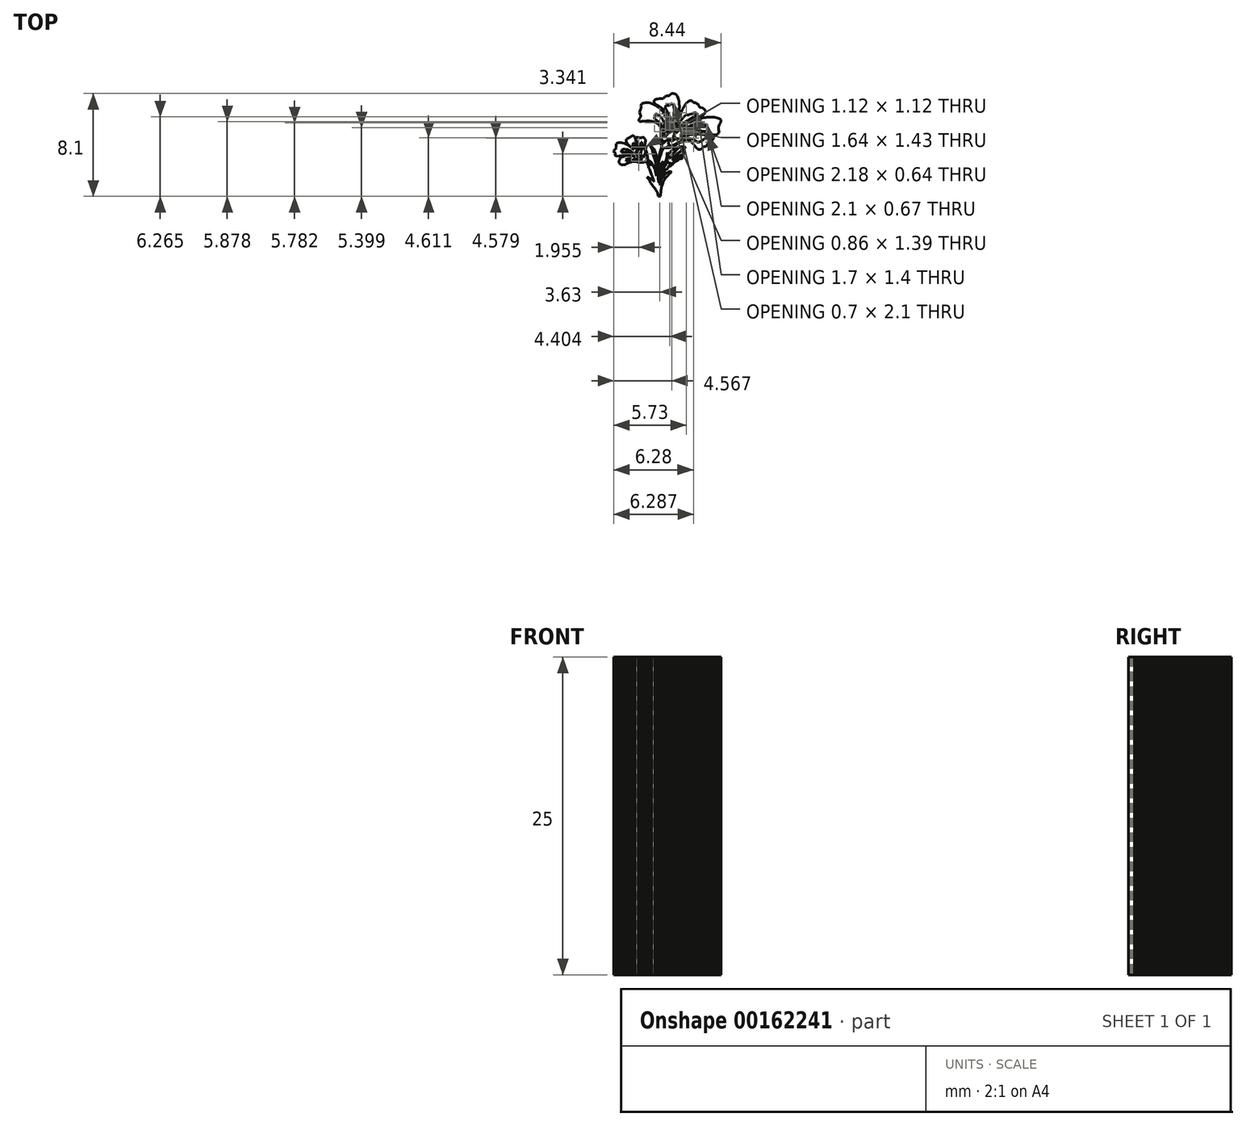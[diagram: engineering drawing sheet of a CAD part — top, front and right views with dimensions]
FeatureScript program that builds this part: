
annotation { "Feature Type Name" : "Feature", "Feature Type Description" : "" }
export const myFeature = defineFeature(function(context is Context, id is Id, definition is map)
    precondition{}
    {
        {
            var Q0;
            Q0=qCreatedBy(makeId("Top.planeOp"),FACE);
            var sketch = newSketch(context, id + "F0", { "sketchPlane" : qUnion([Q0])});
            skLineSegment(sketch, "E0", {"start": v(-2.53, -5.1) * mm, "end": v(-2.55, -5) * mm});
            skLineSegment(sketch, "E1", {"start": v(-2.55, -5) * mm, "end": v(-2.57, -4.93) * mm});
            skLineSegment(sketch, "E2", {"start": v(-2.57, -4.93) * mm, "end": v(-2.6, -4.87) * mm});
            skLineSegment(sketch, "E3", {"start": v(-2.6, -4.87) * mm, "end": v(-2.62, -4.82) * mm});
            skLineSegment(sketch, "E4", {"start": v(-2.62, -4.82) * mm, "end": v(-2.65, -4.76) * mm});
            skLineSegment(sketch, "E5", {"start": v(-2.65, -4.76) * mm, "end": v(-2.7, -4.67) * mm});
            skLineSegment(sketch, "E6", {"start": v(-2.7, -4.67) * mm, "end": v(-2.79, -4.56) * mm});
            skLineSegment(sketch, "E7", {"start": v(-2.79, -4.56) * mm, "end": v(-2.9, -4.42) * mm});
            skLineSegment(sketch, "E8", {"start": v(-2.9, -4.42) * mm, "end": v(-2.98, -4.32) * mm});
            skLineSegment(sketch, "E9", {"start": v(-2.98, -4.32) * mm, "end": v(-3.03, -4.24) * mm});
            skLineSegment(sketch, "E10", {"start": v(-3.03, -4.24) * mm, "end": v(-3.08, -4.18) * mm});
            skLineSegment(sketch, "E11", {"start": v(-3.08, -4.18) * mm, "end": v(-3.12, -4.13) * mm});
            skLineSegment(sketch, "E12", {"start": v(-3.12, -4.13) * mm, "end": v(-3.14, -4.1) * mm});
            skLineSegment(sketch, "E13", {"start": v(-3.14, -4.1) * mm, "end": v(-3.16, -4.06) * mm});
            skLineSegment(sketch, "E14", {"start": v(-3.16, -4.06) * mm, "end": v(-3.16, -4.04) * mm});
            skLineSegment(sketch, "E15", {"start": v(-3.16, -4.04) * mm, "end": v(-3.17, -4.02) * mm});
            skLineSegment(sketch, "E16", {"start": v(-3.17, -4.02) * mm, "end": v(-3.17, -4.01) * mm});
            skLineSegment(sketch, "E17", {"start": v(-3.17, -4.01) * mm, "end": v(-3.18, -4) * mm});
            skLineSegment(sketch, "E18", {"start": v(-3.18, -4) * mm, "end": v(-3.19, -3.97) * mm});
            skLineSegment(sketch, "E19", {"start": v(-3.19, -3.97) * mm, "end": v(-3.2, -3.95) * mm});
            skLineSegment(sketch, "E20", {"start": v(-3.2, -3.95) * mm, "end": v(-3.26, -3.85) * mm});
            skLineSegment(sketch, "E21", {"start": v(-3.26, -3.85) * mm, "end": v(-3.35, -3.76) * mm});
            skLineSegment(sketch, "E22", {"start": v(-3.35, -3.76) * mm, "end": v(-3.4, -3.73) * mm});
            skLineSegment(sketch, "E23", {"start": v(-3.4, -3.73) * mm, "end": v(-3.4, -3.7) * mm});
            skLineSegment(sketch, "E24", {"start": v(-3.4, -3.7) * mm, "end": v(-3.39, -3.69) * mm});
            skLineSegment(sketch, "E25", {"start": v(-3.39, -3.69) * mm, "end": v(-3.37, -3.68) * mm});
            skLineSegment(sketch, "E26", {"start": v(-3.37, -3.68) * mm, "end": v(-3.34, -3.69) * mm});
            skLineSegment(sketch, "E27", {"start": v(-3.34, -3.69) * mm, "end": v(-3.3, -3.7) * mm});
            skLineSegment(sketch, "E28", {"start": v(-3.3, -3.7) * mm, "end": v(-3.26, -3.74) * mm});
            skLineSegment(sketch, "E29", {"start": v(-3.26, -3.74) * mm, "end": v(-3.21, -3.76) * mm});
            skLineSegment(sketch, "E30", {"start": v(-3.21, -3.76) * mm, "end": v(-3.19, -3.77) * mm});
            skLineSegment(sketch, "E31", {"start": v(-3.19, -3.77) * mm, "end": v(-3.16, -3.79) * mm});
            skLineSegment(sketch, "E32", {"start": v(-3.16, -3.79) * mm, "end": v(-3.12, -3.8) * mm});
            skLineSegment(sketch, "E33", {"start": v(-3.12, -3.8) * mm, "end": v(-3.1, -3.82) * mm});
            skLineSegment(sketch, "E34", {"start": v(-3.1, -3.82) * mm, "end": v(-3.06, -3.84) * mm});
            skLineSegment(sketch, "E35", {"start": v(-3.06, -3.84) * mm, "end": v(-3.03, -3.86) * mm});
            skLineSegment(sketch, "E36", {"start": v(-3.03, -3.86) * mm, "end": v(-3.01, -3.88) * mm});
            skLineSegment(sketch, "E37", {"start": v(-3.01, -3.88) * mm, "end": v(-3, -3.9) * mm});
            skLineSegment(sketch, "E38", {"start": v(-3, -3.9) * mm, "end": v(-2.98, -3.91) * mm});
            skLineSegment(sketch, "E39", {"start": v(-2.98, -3.91) * mm, "end": v(-2.96, -3.92) * mm});
            skLineSegment(sketch, "E40", {"start": v(-2.96, -3.92) * mm, "end": v(-2.95, -3.92) * mm});
            skLineSegment(sketch, "E41", {"start": v(-2.95, -3.92) * mm, "end": v(-2.94, -3.93) * mm});
            skLineSegment(sketch, "E42", {"start": v(-2.94, -3.93) * mm, "end": v(-2.92, -3.95) * mm});
            skLineSegment(sketch, "E43", {"start": v(-2.92, -3.95) * mm, "end": v(-2.9, -3.97) * mm});
            skLineSegment(sketch, "E44", {"start": v(-2.9, -3.97) * mm, "end": v(-2.88, -3.98) * mm});
            skLineSegment(sketch, "E45", {"start": v(-2.88, -3.98) * mm, "end": v(-2.87, -4) * mm});
            skLineSegment(sketch, "E46", {"start": v(-2.87, -4) * mm, "end": v(-2.86, -4) * mm});
            skLineSegment(sketch, "E47", {"start": v(-2.86, -4) * mm, "end": v(-2.85, -4) * mm});
            skLineSegment(sketch, "E48", {"start": v(-2.85, -4) * mm, "end": v(-2.85, -3.99) * mm});
            skLineSegment(sketch, "E49", {"start": v(-2.85, -3.99) * mm, "end": v(-2.87, -3.96) * mm});
            skLineSegment(sketch, "E50", {"start": v(-2.87, -3.96) * mm, "end": v(-2.9, -3.85) * mm});
            skLineSegment(sketch, "E51", {"start": v(-2.9, -3.85) * mm, "end": v(-2.96, -3.68) * mm});
            skLineSegment(sketch, "E52", {"start": v(-2.96, -3.68) * mm, "end": v(-2.98, -3.63) * mm});
            skLineSegment(sketch, "E53", {"start": v(-2.98, -3.63) * mm, "end": v(-3, -3.58) * mm});
            skLineSegment(sketch, "E54", {"start": v(-3, -3.58) * mm, "end": v(-3, -3.54) * mm});
            skLineSegment(sketch, "E55", {"start": v(-3, -3.54) * mm, "end": v(-3.02, -3.5) * mm});
            skLineSegment(sketch, "E56", {"start": v(-3.02, -3.5) * mm, "end": v(-3.05, -3.43) * mm});
            skLineSegment(sketch, "E57", {"start": v(-3.05, -3.43) * mm, "end": v(-3.09, -3.35) * mm});
            skLineSegment(sketch, "E58", {"start": v(-3.09, -3.35) * mm, "end": v(-3.13, -3.26) * mm});
            skLineSegment(sketch, "E59", {"start": v(-3.13, -3.26) * mm, "end": v(-3.16, -3.16) * mm});
            skLineSegment(sketch, "E60", {"start": v(-3.16, -3.16) * mm, "end": v(-3.2, -3.06) * mm});
            skLineSegment(sketch, "E61", {"start": v(-3.2, -3.06) * mm, "end": v(-3.24, -2.96) * mm});
            skLineSegment(sketch, "E62", {"start": v(-3.24, -2.96) * mm, "end": v(-3.28, -2.87) * mm});
            skLineSegment(sketch, "E63", {"start": v(-3.28, -2.87) * mm, "end": v(-3.3, -2.79) * mm});
            skLineSegment(sketch, "E64", {"start": v(-3.3, -2.79) * mm, "end": v(-3.34, -2.7) * mm});
            skLineSegment(sketch, "E65", {"start": v(-3.34, -2.7) * mm, "end": v(-3.36, -2.62) * mm});
            skLineSegment(sketch, "E66", {"start": v(-3.36, -2.62) * mm, "end": v(-3.38, -2.57) * mm});
            skLineSegment(sketch, "E67", {"start": v(-3.38, -2.57) * mm, "end": v(-3.4, -2.53) * mm});
            skLineSegment(sketch, "E68", {"start": v(-3.4, -2.53) * mm, "end": v(-3.42, -2.5) * mm});
            skLineSegment(sketch, "E69", {"start": v(-3.42, -2.5) * mm, "end": v(-3.44, -2.5) * mm});
            skLineSegment(sketch, "E70", {"start": v(-3.44, -2.5) * mm, "end": v(-3.46, -2.49) * mm});
            skLineSegment(sketch, "E71", {"start": v(-3.46, -2.49) * mm, "end": v(-3.48, -2.49) * mm});
            skLineSegment(sketch, "E72", {"start": v(-3.48, -2.49) * mm, "end": v(-3.52, -2.48) * mm});
            skLineSegment(sketch, "E73", {"start": v(-3.52, -2.48) * mm, "end": v(-3.56, -2.47) * mm});
            skLineSegment(sketch, "E74", {"start": v(-3.56, -2.47) * mm, "end": v(-3.57, -2.47) * mm});
            skLineSegment(sketch, "E75", {"start": v(-3.57, -2.47) * mm, "end": v(-3.6, -2.47) * mm});
            skLineSegment(sketch, "E76", {"start": v(-3.6, -2.47) * mm, "end": v(-3.62, -2.47) * mm});
            skLineSegment(sketch, "E77", {"start": v(-3.62, -2.47) * mm, "end": v(-3.66, -2.5) * mm});
            skLineSegment(sketch, "E78", {"start": v(-3.66, -2.5) * mm, "end": v(-3.68, -2.5) * mm});
            skLineSegment(sketch, "E79", {"start": v(-3.68, -2.5) * mm, "end": v(-3.7, -2.51) * mm});
            skLineSegment(sketch, "E80", {"start": v(-3.7, -2.51) * mm, "end": v(-3.72, -2.52) * mm});
            skLineSegment(sketch, "E81", {"start": v(-3.72, -2.52) * mm, "end": v(-3.74, -2.52) * mm});
            skLineSegment(sketch, "E82", {"start": v(-3.74, -2.52) * mm, "end": v(-3.76, -2.52) * mm});
            skLineSegment(sketch, "E83", {"start": v(-3.76, -2.52) * mm, "end": v(-3.8, -2.52) * mm});
            skLineSegment(sketch, "E84", {"start": v(-3.8, -2.52) * mm, "end": v(-3.83, -2.53) * mm});
            skLineSegment(sketch, "E85", {"start": v(-3.83, -2.53) * mm, "end": v(-3.87, -2.53) * mm});
            skLineSegment(sketch, "E86", {"start": v(-3.87, -2.53) * mm, "end": v(-3.95, -2.52) * mm});
            skLineSegment(sketch, "E87", {"start": v(-3.95, -2.52) * mm, "end": v(-4.02, -2.52) * mm});
            skLineSegment(sketch, "E88", {"start": v(-4.02, -2.52) * mm, "end": v(-4.1, -2.5) * mm});
            skLineSegment(sketch, "E89", {"start": v(-4.1, -2.5) * mm, "end": v(-4.19, -2.5) * mm});
            skLineSegment(sketch, "E90", {"start": v(-4.19, -2.5) * mm, "end": v(-4.33, -2.46) * mm});
            skLineSegment(sketch, "E91", {"start": v(-4.33, -2.46) * mm, "end": v(-4.43, -2.45) * mm});
            skLineSegment(sketch, "E92", {"start": v(-4.43, -2.45) * mm, "end": v(-4.5, -2.45) * mm});
            skLineSegment(sketch, "E93", {"start": v(-4.5, -2.45) * mm, "end": v(-4.57, -2.46) * mm});
            skLineSegment(sketch, "E94", {"start": v(-4.57, -2.46) * mm, "end": v(-4.62, -2.47) * mm});
            skLineSegment(sketch, "E95", {"start": v(-4.62, -2.47) * mm, "end": v(-4.64, -2.49) * mm});
            skLineSegment(sketch, "E96", {"start": v(-4.64, -2.49) * mm, "end": v(-4.65, -2.5) * mm});
            skLineSegment(sketch, "E97", {"start": v(-4.65, -2.5) * mm, "end": v(-4.67, -2.5) * mm});
            skLineSegment(sketch, "E98", {"start": v(-4.67, -2.5) * mm, "end": v(-4.7, -2.51) * mm});
            skLineSegment(sketch, "E99", {"start": v(-4.7, -2.51) * mm, "end": v(-4.74, -2.53) * mm});
            skLineSegment(sketch, "E100", {"start": v(-4.74, -2.53) * mm, "end": v(-4.92, -2.59) * mm});
            skLineSegment(sketch, "E101", {"start": v(-4.92, -2.59) * mm, "end": v(-5.1, -2.67) * mm});
            skLineSegment(sketch, "E102", {"start": v(-5.1, -2.67) * mm, "end": v(-5.15, -2.7) * mm});
            skLineSegment(sketch, "E103", {"start": v(-5.15, -2.7) * mm, "end": v(-5.2, -2.7) * mm});
            skLineSegment(sketch, "E104", {"start": v(-5.2, -2.7) * mm, "end": v(-5.24, -2.71) * mm});
            skLineSegment(sketch, "E105", {"start": v(-5.24, -2.71) * mm, "end": v(-5.3, -2.71) * mm});
            skLineSegment(sketch, "E106", {"start": v(-5.3, -2.71) * mm, "end": v(-5.38, -2.71) * mm});
            skLineSegment(sketch, "E107", {"start": v(-5.38, -2.71) * mm, "end": v(-5.44, -2.7) * mm});
            skLineSegment(sketch, "E108", {"start": v(-5.44, -2.7) * mm, "end": v(-5.49, -2.67) * mm});
            skLineSegment(sketch, "E109", {"start": v(-5.49, -2.67) * mm, "end": v(-5.55, -2.62) * mm});
            skLineSegment(sketch, "E110", {"start": v(-5.55, -2.62) * mm, "end": v(-5.62, -2.56) * mm});
            skLineSegment(sketch, "E111", {"start": v(-5.62, -2.56) * mm, "end": v(-5.62, -2.5) * mm});
            skLineSegment(sketch, "E112", {"start": v(-5.62, -2.5) * mm, "end": v(-5.6, -2.44) * mm});
            skLineSegment(sketch, "E113", {"start": v(-5.6, -2.44) * mm, "end": v(-5.58, -2.37) * mm});
            skLineSegment(sketch, "E114", {"start": v(-5.58, -2.37) * mm, "end": v(-5.57, -2.35) * mm});
            skLineSegment(sketch, "E115", {"start": v(-5.57, -2.35) * mm, "end": v(-5.56, -2.32) * mm});
            skLineSegment(sketch, "E116", {"start": v(-5.56, -2.32) * mm, "end": v(-5.55, -2.3) * mm});
            skLineSegment(sketch, "E117", {"start": v(-5.55, -2.3) * mm, "end": v(-5.55, -2.28) * mm});
            skLineSegment(sketch, "E118", {"start": v(-5.55, -2.28) * mm, "end": v(-5.54, -2.25) * mm});
            skLineSegment(sketch, "E119", {"start": v(-5.54, -2.25) * mm, "end": v(-5.53, -2.22) * mm});
            skLineSegment(sketch, "E120", {"start": v(-5.53, -2.22) * mm, "end": v(-5.48, -2.17) * mm});
            skLineSegment(sketch, "E121", {"start": v(-5.48, -2.17) * mm, "end": v(-5.38, -2.11) * mm});
            skLineSegment(sketch, "E122", {"start": v(-5.38, -2.11) * mm, "end": v(-5.26, -2.06) * mm});
            skLineSegment(sketch, "E123", {"start": v(-5.26, -2.06) * mm, "end": v(-5.12, -2.02) * mm});
            skLineSegment(sketch, "E124", {"start": v(-5.12, -2.02) * mm, "end": v(-4.83, -2) * mm});
            skLineSegment(sketch, "E125", {"start": v(-4.83, -2) * mm, "end": v(-4.54, -2.02) * mm});
            skLineSegment(sketch, "E126", {"start": v(-4.54, -2.02) * mm, "end": v(-4.49, -2.04) * mm});
            skLineSegment(sketch, "E127", {"start": v(-4.49, -2.04) * mm, "end": v(-4.44, -2.05) * mm});
            skLineSegment(sketch, "E128", {"start": v(-4.44, -2.05) * mm, "end": v(-4.4, -2.06) * mm});
            skLineSegment(sketch, "E129", {"start": v(-4.4, -2.06) * mm, "end": v(-4.4, -2.06) * mm});
            skLineSegment(sketch, "E130", {"start": v(-4.4, -2.06) * mm, "end": v(-4.37, -2.07) * mm});
            skLineSegment(sketch, "E131", {"start": v(-4.37, -2.07) * mm, "end": v(-4.35, -2.08) * mm});
            skLineSegment(sketch, "E132", {"start": v(-4.35, -2.08) * mm, "end": v(-4.34, -2.07) * mm});
            skLineSegment(sketch, "E133", {"start": v(-4.34, -2.07) * mm, "end": v(-4.33, -2.07) * mm});
            skLineSegment(sketch, "E134", {"start": v(-4.33, -2.07) * mm, "end": v(-4.35, -2.06) * mm});
            skLineSegment(sketch, "E135", {"start": v(-4.35, -2.06) * mm, "end": v(-4.38, -2.04) * mm});
            skLineSegment(sketch, "E136", {"start": v(-4.38, -2.04) * mm, "end": v(-4.44, -2.03) * mm});
            skLineSegment(sketch, "E137", {"start": v(-4.44, -2.03) * mm, "end": v(-4.5, -2.01) * mm});
            skLineSegment(sketch, "E138", {"start": v(-4.5, -2.01) * mm, "end": v(-4.58, -2) * mm});
            skLineSegment(sketch, "E139", {"start": v(-4.58, -2) * mm, "end": v(-4.67, -1.98) * mm});
            skLineSegment(sketch, "E140", {"start": v(-4.67, -1.98) * mm, "end": v(-4.75, -1.97) * mm});
            skLineSegment(sketch, "E141", {"start": v(-4.75, -1.97) * mm, "end": v(-4.83, -1.96) * mm});
            skLineSegment(sketch, "E142", {"start": v(-4.83, -1.96) * mm, "end": v(-5.14, -1.96) * mm});
            skLineSegment(sketch, "E143", {"start": v(-5.14, -1.96) * mm, "end": v(-5.42, -2) * mm});
            skLineSegment(sketch, "E144", {"start": v(-5.42, -2) * mm, "end": v(-5.58, -2.02) * mm});
            skLineSegment(sketch, "E145", {"start": v(-5.58, -2.02) * mm, "end": v(-5.71, -2.03) * mm});
            skLineSegment(sketch, "E146", {"start": v(-5.71, -2.03) * mm, "end": v(-5.82, -2.01) * mm});
            skLineSegment(sketch, "E147", {"start": v(-5.82, -2.01) * mm, "end": v(-5.9, -1.97) * mm});
            skLineSegment(sketch, "E148", {"start": v(-5.9, -1.97) * mm, "end": v(-5.92, -1.94) * mm});
            skLineSegment(sketch, "E149", {"start": v(-5.92, -1.94) * mm, "end": v(-5.92, -1.9) * mm});
            skLineSegment(sketch, "E150", {"start": v(-5.92, -1.9) * mm, "end": v(-5.9, -1.86) * mm});
            skLineSegment(sketch, "E151", {"start": v(-5.9, -1.86) * mm, "end": v(-5.87, -1.82) * mm});
            skLineSegment(sketch, "E152", {"start": v(-5.87, -1.82) * mm, "end": v(-5.83, -1.8) * mm});
            skLineSegment(sketch, "E153", {"start": v(-5.83, -1.8) * mm, "end": v(-5.88, -1.78) * mm});
            skLineSegment(sketch, "E154", {"start": v(-5.88, -1.78) * mm, "end": v(-5.98, -1.71) * mm});
            skLineSegment(sketch, "E155", {"start": v(-5.98, -1.71) * mm, "end": v(-6.02, -1.64) * mm});
            skLineSegment(sketch, "E156", {"start": v(-6.02, -1.64) * mm, "end": v(-6, -1.56) * mm});
            skLineSegment(sketch, "E157", {"start": v(-6, -1.56) * mm, "end": v(-5.93, -1.5) * mm});
            skLineSegment(sketch, "E158", {"start": v(-5.93, -1.5) * mm, "end": v(-5.89, -1.46) * mm});
            skLineSegment(sketch, "E159", {"start": v(-5.89, -1.46) * mm, "end": v(-5.85, -1.44) * mm});
            skLineSegment(sketch, "E160", {"start": v(-5.85, -1.44) * mm, "end": v(-5.83, -1.42) * mm});
            skLineSegment(sketch, "E161", {"start": v(-5.83, -1.42) * mm, "end": v(-5.82, -1.4) * mm});
            skLineSegment(sketch, "E162", {"start": v(-5.82, -1.4) * mm, "end": v(-5.81, -1.38) * mm});
            skLineSegment(sketch, "E163", {"start": v(-5.81, -1.38) * mm, "end": v(-5.81, -1.36) * mm});
            skLineSegment(sketch, "E164", {"start": v(-5.81, -1.36) * mm, "end": v(-5.82, -1.33) * mm});
            skLineSegment(sketch, "E165", {"start": v(-5.82, -1.33) * mm, "end": v(-5.83, -1.3) * mm});
            skLineSegment(sketch, "E166", {"start": v(-5.83, -1.3) * mm, "end": v(-5.84, -1.24) * mm});
            skLineSegment(sketch, "E167", {"start": v(-5.84, -1.24) * mm, "end": v(-5.84, -1.18) * mm});
            skLineSegment(sketch, "E168", {"start": v(-5.84, -1.18) * mm, "end": v(-5.84, -1.12) * mm});
            skLineSegment(sketch, "E169", {"start": v(-5.84, -1.12) * mm, "end": v(-5.82, -1.07) * mm});
            skLineSegment(sketch, "E170", {"start": v(-5.82, -1.07) * mm, "end": v(-5.78, -1.02) * mm});
            skLineSegment(sketch, "E171", {"start": v(-5.78, -1.02) * mm, "end": v(-5.72, -0.98) * mm});
            skLineSegment(sketch, "E172", {"start": v(-5.72, -0.98) * mm, "end": v(-5.64, -0.96) * mm});
            skLineSegment(sketch, "E173", {"start": v(-5.64, -0.96) * mm, "end": v(-5.55, -0.95) * mm});
            skLineSegment(sketch, "E174", {"start": v(-5.55, -0.95) * mm, "end": v(-5.43, -0.96) * mm});
            skLineSegment(sketch, "E175", {"start": v(-5.43, -0.96) * mm, "end": v(-5.3, -1) * mm});
            skLineSegment(sketch, "E176", {"start": v(-5.3, -1) * mm, "end": v(-5.18, -1.04) * mm});
            skLineSegment(sketch, "E177", {"start": v(-5.18, -1.04) * mm, "end": v(-5.04, -1.1) * mm});
            skLineSegment(sketch, "E178", {"start": v(-5.04, -1.1) * mm, "end": v(-4.9, -1.16) * mm});
            skLineSegment(sketch, "E179", {"start": v(-4.9, -1.16) * mm, "end": v(-4.78, -1.24) * mm});
            skLineSegment(sketch, "E180", {"start": v(-4.78, -1.24) * mm, "end": v(-4.65, -1.33) * mm});
            skLineSegment(sketch, "E181", {"start": v(-4.65, -1.33) * mm, "end": v(-4.55, -1.42) * mm});
            skLineSegment(sketch, "E182", {"start": v(-4.55, -1.42) * mm, "end": v(-4.5, -1.46) * mm});
            skLineSegment(sketch, "E183", {"start": v(-4.5, -1.46) * mm, "end": v(-4.47, -1.5) * mm});
            skLineSegment(sketch, "E184", {"start": v(-4.47, -1.5) * mm, "end": v(-4.45, -1.5) * mm});
            skLineSegment(sketch, "E185", {"start": v(-4.45, -1.5) * mm, "end": v(-4.45, -1.5) * mm});
            skLineSegment(sketch, "E186", {"start": v(-4.45, -1.5) * mm, "end": v(-4.48, -1.46) * mm});
            skLineSegment(sketch, "E187", {"start": v(-4.48, -1.46) * mm, "end": v(-4.51, -1.43) * mm});
            skLineSegment(sketch, "E188", {"start": v(-4.51, -1.43) * mm, "end": v(-4.56, -1.39) * mm});
            skLineSegment(sketch, "E189", {"start": v(-4.56, -1.39) * mm, "end": v(-4.6, -1.34) * mm});
            skLineSegment(sketch, "E190", {"start": v(-4.6, -1.34) * mm, "end": v(-4.65, -1.3) * mm});
            skLineSegment(sketch, "E191", {"start": v(-4.65, -1.3) * mm, "end": v(-4.7, -1.26) * mm});
            skLineSegment(sketch, "E192", {"start": v(-4.7, -1.26) * mm, "end": v(-4.73, -1.24) * mm});
            skLineSegment(sketch, "E193", {"start": v(-4.73, -1.24) * mm, "end": v(-4.77, -1.21) * mm});
            skLineSegment(sketch, "E194", {"start": v(-4.77, -1.21) * mm, "end": v(-4.8, -1.18) * mm});
            skLineSegment(sketch, "E195", {"start": v(-4.8, -1.18) * mm, "end": v(-4.85, -1.14) * mm});
            skLineSegment(sketch, "E196", {"start": v(-4.85, -1.14) * mm, "end": v(-4.88, -1.1) * mm});
            skLineSegment(sketch, "E197", {"start": v(-4.88, -1.1) * mm, "end": v(-4.98, -0.98) * mm});
            skLineSegment(sketch, "E198", {"start": v(-4.98, -0.98) * mm, "end": v(-5.03, -0.87) * mm});
            skLineSegment(sketch, "E199", {"start": v(-5.03, -0.87) * mm, "end": v(-5.03, -0.77) * mm});
            skLineSegment(sketch, "E200", {"start": v(-5.03, -0.77) * mm, "end": v(-4.99, -0.68) * mm});
            skLineSegment(sketch, "E201", {"start": v(-4.99, -0.68) * mm, "end": v(-4.95, -0.65) * mm});
            skLineSegment(sketch, "E202", {"start": v(-4.95, -0.65) * mm, "end": v(-4.9, -0.61) * mm});
            skLineSegment(sketch, "E203", {"start": v(-4.9, -0.61) * mm, "end": v(-4.82, -0.58) * mm});
            skLineSegment(sketch, "E204", {"start": v(-4.82, -0.58) * mm, "end": v(-4.76, -0.55) * mm});
            skLineSegment(sketch, "E205", {"start": v(-4.76, -0.55) * mm, "end": v(-4.72, -0.53) * mm});
            skLineSegment(sketch, "E206", {"start": v(-4.72, -0.53) * mm, "end": v(-4.7, -0.5) * mm});
            skLineSegment(sketch, "E207", {"start": v(-4.7, -0.5) * mm, "end": v(-4.67, -0.47) * mm});
            skLineSegment(sketch, "E208", {"start": v(-4.67, -0.47) * mm, "end": v(-4.63, -0.45) * mm});
            skLineSegment(sketch, "E209", {"start": v(-4.63, -0.45) * mm, "end": v(-4.6, -0.43) * mm});
            skLineSegment(sketch, "E210", {"start": v(-4.6, -0.43) * mm, "end": v(-4.55, -0.43) * mm});
            skLineSegment(sketch, "E211", {"start": v(-4.55, -0.43) * mm, "end": v(-4.49, -0.44) * mm});
            skLineSegment(sketch, "E212", {"start": v(-4.49, -0.44) * mm, "end": v(-4.43, -0.47) * mm});
            skLineSegment(sketch, "E213", {"start": v(-4.43, -0.47) * mm, "end": v(-4.38, -0.51) * mm});
            skLineSegment(sketch, "E214", {"start": v(-4.38, -0.51) * mm, "end": v(-4.34, -0.58) * mm});
            skLineSegment(sketch, "E215", {"start": v(-4.34, -0.58) * mm, "end": v(-4.3, -0.66) * mm});
            skLineSegment(sketch, "E216", {"start": v(-4.3, -0.66) * mm, "end": v(-4.26, -0.8) * mm});
            skLineSegment(sketch, "E217", {"start": v(-4.26, -0.8) * mm, "end": v(-4.22, -0.97) * mm});
            skLineSegment(sketch, "E218", {"start": v(-4.22, -0.97) * mm, "end": v(-4.18, -1.14) * mm});
            skLineSegment(sketch, "E219", {"start": v(-4.18, -1.14) * mm, "end": v(-4.15, -1.26) * mm});
            skLineSegment(sketch, "E220", {"start": v(-4.15, -1.26) * mm, "end": v(-4.13, -1.34) * mm});
            skLineSegment(sketch, "E221", {"start": v(-4.13, -1.34) * mm, "end": v(-4.11, -1.4) * mm});
            skLineSegment(sketch, "E222", {"start": v(-4.11, -1.4) * mm, "end": v(-4.1, -1.4) * mm});
            skLineSegment(sketch, "E223", {"start": v(-4.1, -1.4) * mm, "end": v(-4.1, -1.4) * mm});
            skLineSegment(sketch, "E224", {"start": v(-4.1, -1.4) * mm, "end": v(-4.1, -1.39) * mm});
            skLineSegment(sketch, "E225", {"start": v(-4.1, -1.39) * mm, "end": v(-4.1, -1.36) * mm});
            skLineSegment(sketch, "E226", {"start": v(-4.1, -1.36) * mm, "end": v(-4.11, -1.32) * mm});
            skLineSegment(sketch, "E227", {"start": v(-4.11, -1.32) * mm, "end": v(-4.13, -1.27) * mm});
            skLineSegment(sketch, "E228", {"start": v(-4.13, -1.27) * mm, "end": v(-4.14, -1.2) * mm});
            skLineSegment(sketch, "E229", {"start": v(-4.14, -1.2) * mm, "end": v(-4.16, -1.14) * mm});
            skLineSegment(sketch, "E230", {"start": v(-4.16, -1.14) * mm, "end": v(-4.17, -1.06) * mm});
            skLineSegment(sketch, "E231", {"start": v(-4.17, -1.06) * mm, "end": v(-4.2, -0.97) * mm});
            skLineSegment(sketch, "E232", {"start": v(-4.2, -0.97) * mm, "end": v(-4.22, -0.87) * mm});
            skLineSegment(sketch, "E233", {"start": v(-4.22, -0.87) * mm, "end": v(-4.24, -0.8) * mm});
            skLineSegment(sketch, "E234", {"start": v(-4.24, -0.8) * mm, "end": v(-4.26, -0.72) * mm});
            skLineSegment(sketch, "E235", {"start": v(-4.26, -0.72) * mm, "end": v(-4.28, -0.66) * mm});
            skLineSegment(sketch, "E236", {"start": v(-4.28, -0.66) * mm, "end": v(-4.29, -0.61) * mm});
            skLineSegment(sketch, "E237", {"start": v(-4.29, -0.61) * mm, "end": v(-4.3, -0.59) * mm});
            skLineSegment(sketch, "E238", {"start": v(-4.3, -0.59) * mm, "end": v(-4.3, -0.57) * mm});
            skLineSegment(sketch, "E239", {"start": v(-4.3, -0.57) * mm, "end": v(-4.28, -0.56) * mm});
            skLineSegment(sketch, "E240", {"start": v(-4.28, -0.56) * mm, "end": v(-4.26, -0.56) * mm});
            skLineSegment(sketch, "E241", {"start": v(-4.26, -0.56) * mm, "end": v(-4.2, -0.56) * mm});
            skLineSegment(sketch, "E242", {"start": v(-4.2, -0.56) * mm, "end": v(-4.1, -0.56) * mm});
            skLineSegment(sketch, "E243", {"start": v(-4.1, -0.56) * mm, "end": v(-4, -0.58) * mm});
            skLineSegment(sketch, "E244", {"start": v(-4, -0.58) * mm, "end": v(-3.95, -0.58) * mm});
            skLineSegment(sketch, "E245", {"start": v(-3.95, -0.58) * mm, "end": v(-3.91, -0.6) * mm});
            skLineSegment(sketch, "E246", {"start": v(-3.91, -0.6) * mm, "end": v(-3.89, -0.6) * mm});
            skLineSegment(sketch, "E247", {"start": v(-3.89, -0.6) * mm, "end": v(-3.86, -0.6) * mm});
            skLineSegment(sketch, "E248", {"start": v(-3.86, -0.6) * mm, "end": v(-3.85, -0.6) * mm});
            skLineSegment(sketch, "E249", {"start": v(-3.85, -0.6) * mm, "end": v(-3.84, -0.6) * mm});
            skLineSegment(sketch, "E250", {"start": v(-3.84, -0.6) * mm, "end": v(-3.82, -0.59) * mm});
            skLineSegment(sketch, "E251", {"start": v(-3.82, -0.59) * mm, "end": v(-3.81, -0.58) * mm});
            skLineSegment(sketch, "E252", {"start": v(-3.81, -0.58) * mm, "end": v(-3.76, -0.56) * mm});
            skLineSegment(sketch, "E253", {"start": v(-3.76, -0.56) * mm, "end": v(-3.7, -0.56) * mm});
            skLineSegment(sketch, "E254", {"start": v(-3.7, -0.56) * mm, "end": v(-3.65, -0.58) * mm});
            skLineSegment(sketch, "E255", {"start": v(-3.65, -0.58) * mm, "end": v(-3.6, -0.63) * mm});
            skLineSegment(sketch, "E256", {"start": v(-3.6, -0.63) * mm, "end": v(-3.56, -0.67) * mm});
            skLineSegment(sketch, "E257", {"start": v(-3.56, -0.67) * mm, "end": v(-3.54, -0.71) * mm});
            skLineSegment(sketch, "E258", {"start": v(-3.54, -0.71) * mm, "end": v(-3.53, -0.77) * mm});
            skLineSegment(sketch, "E259", {"start": v(-3.53, -0.77) * mm, "end": v(-3.52, -0.84) * mm});
            skLineSegment(sketch, "E260", {"start": v(-3.52, -0.84) * mm, "end": v(-3.53, -0.93) * mm});
            skLineSegment(sketch, "E261", {"start": v(-3.53, -0.93) * mm, "end": v(-3.55, -1.02) * mm});
            skLineSegment(sketch, "E262", {"start": v(-3.55, -1.02) * mm, "end": v(-3.58, -1.12) * mm});
            skLineSegment(sketch, "E263", {"start": v(-3.58, -1.12) * mm, "end": v(-3.63, -1.23) * mm});
            skLineSegment(sketch, "E264", {"start": v(-3.63, -1.23) * mm, "end": v(-3.66, -1.3) * mm});
            skLineSegment(sketch, "E265", {"start": v(-3.66, -1.3) * mm, "end": v(-3.6, -1.27) * mm});
            skLineSegment(sketch, "E266", {"start": v(-3.6, -1.27) * mm, "end": v(-3.57, -1.25) * mm});
            skLineSegment(sketch, "E267", {"start": v(-3.57, -1.25) * mm, "end": v(-3.53, -1.24) * mm});
            skLineSegment(sketch, "E268", {"start": v(-3.53, -1.24) * mm, "end": v(-3.5, -1.25) * mm});
            skLineSegment(sketch, "E269", {"start": v(-3.5, -1.25) * mm, "end": v(-3.48, -1.26) * mm});
            skLineSegment(sketch, "E270", {"start": v(-3.48, -1.26) * mm, "end": v(-3.46, -1.27) * mm});
            skLineSegment(sketch, "E271", {"start": v(-3.46, -1.27) * mm, "end": v(-3.45, -1.29) * mm});
            skLineSegment(sketch, "E272", {"start": v(-3.45, -1.29) * mm, "end": v(-3.45, -1.31) * mm});
            skLineSegment(sketch, "E273", {"start": v(-3.45, -1.31) * mm, "end": v(-3.47, -1.34) * mm});
            skLineSegment(sketch, "E274", {"start": v(-3.47, -1.34) * mm, "end": v(-3.5, -1.4) * mm});
            skLineSegment(sketch, "E275", {"start": v(-3.5, -1.4) * mm, "end": v(-3.5, -1.48) * mm});
            skLineSegment(sketch, "E276", {"start": v(-3.5, -1.48) * mm, "end": v(-3.48, -1.6) * mm});
            skLineSegment(sketch, "E277", {"start": v(-3.48, -1.6) * mm, "end": v(-3.43, -1.73) * mm});
            skLineSegment(sketch, "E278", {"start": v(-3.43, -1.73) * mm, "end": v(-3.37, -1.92) * mm});
            skLineSegment(sketch, "E279", {"start": v(-3.37, -1.92) * mm, "end": v(-3.36, -2.1) * mm});
            skLineSegment(sketch, "E280", {"start": v(-3.36, -2.1) * mm, "end": v(-3.36, -2.14) * mm});
            skLineSegment(sketch, "E281", {"start": v(-3.36, -2.14) * mm, "end": v(-3.36, -2.17) * mm});
            skLineSegment(sketch, "E282", {"start": v(-3.36, -2.17) * mm, "end": v(-3.35, -2.2) * mm});
            skLineSegment(sketch, "E283", {"start": v(-3.35, -2.2) * mm, "end": v(-3.35, -2.21) * mm});
            skLineSegment(sketch, "E284", {"start": v(-3.35, -2.21) * mm, "end": v(-3.34, -2.25) * mm});
            skLineSegment(sketch, "E285", {"start": v(-3.34, -2.25) * mm, "end": v(-3.33, -2.29) * mm});
            skLineSegment(sketch, "E286", {"start": v(-3.33, -2.29) * mm, "end": v(-3.33, -2.33) * mm});
            skLineSegment(sketch, "E287", {"start": v(-3.33, -2.33) * mm, "end": v(-3.33, -2.36) * mm});
            skLineSegment(sketch, "E288", {"start": v(-3.33, -2.36) * mm, "end": v(-3.34, -2.38) * mm});
            skLineSegment(sketch, "E289", {"start": v(-3.34, -2.38) * mm, "end": v(-3.33, -2.4) * mm});
            skLineSegment(sketch, "E290", {"start": v(-3.33, -2.4) * mm, "end": v(-3.32, -2.43) * mm});
            skLineSegment(sketch, "E291", {"start": v(-3.32, -2.43) * mm, "end": v(-3.29, -2.48) * mm});
            skLineSegment(sketch, "E292", {"start": v(-3.29, -2.48) * mm, "end": v(-3.27, -2.52) * mm});
            skLineSegment(sketch, "E293", {"start": v(-3.27, -2.52) * mm, "end": v(-3.24, -2.56) * mm});
            skLineSegment(sketch, "E294", {"start": v(-3.24, -2.56) * mm, "end": v(-3.23, -2.6) * mm});
            skLineSegment(sketch, "E295", {"start": v(-3.23, -2.6) * mm, "end": v(-3.21, -2.63) * mm});
            skLineSegment(sketch, "E296", {"start": v(-3.21, -2.63) * mm, "end": v(-3.2, -2.65) * mm});
            skLineSegment(sketch, "E297", {"start": v(-3.2, -2.65) * mm, "end": v(-3.19, -2.69) * mm});
            skLineSegment(sketch, "E298", {"start": v(-3.19, -2.69) * mm, "end": v(-3.17, -2.72) * mm});
            skLineSegment(sketch, "E299", {"start": v(-3.17, -2.72) * mm, "end": v(-3.16, -2.75) * mm});
            skLineSegment(sketch, "E300", {"start": v(-3.16, -2.75) * mm, "end": v(-3.14, -2.8) * mm});
            skLineSegment(sketch, "E301", {"start": v(-3.14, -2.8) * mm, "end": v(-3.13, -2.8) * mm});
            skLineSegment(sketch, "E302", {"start": v(-3.13, -2.8) * mm, "end": v(-3.12, -2.8) * mm});
            skLineSegment(sketch, "E303", {"start": v(-3.12, -2.8) * mm, "end": v(-3.12, -2.79) * mm});
            skLineSegment(sketch, "E304", {"start": v(-3.12, -2.79) * mm, "end": v(-3.13, -2.72) * mm});
            skLineSegment(sketch, "E305", {"start": v(-3.13, -2.72) * mm, "end": v(-3.15, -2.65) * mm});
            skLineSegment(sketch, "E306", {"start": v(-3.15, -2.65) * mm, "end": v(-3.17, -2.58) * mm});
            skLineSegment(sketch, "E307", {"start": v(-3.17, -2.58) * mm, "end": v(-3.2, -2.52) * mm});
            skLineSegment(sketch, "E308", {"start": v(-3.2, -2.52) * mm, "end": v(-3.22, -2.47) * mm});
            skLineSegment(sketch, "E309", {"start": v(-3.22, -2.47) * mm, "end": v(-3.23, -2.44) * mm});
            skLineSegment(sketch, "E310", {"start": v(-3.23, -2.44) * mm, "end": v(-3.23, -2.41) * mm});
            skLineSegment(sketch, "E311", {"start": v(-3.23, -2.41) * mm, "end": v(-3.23, -2.4) * mm});
            skLineSegment(sketch, "E312", {"start": v(-3.23, -2.4) * mm, "end": v(-3.21, -2.39) * mm});
            skLineSegment(sketch, "E313", {"start": v(-3.21, -2.39) * mm, "end": v(-3.2, -2.4) * mm});
            skLineSegment(sketch, "E314", {"start": v(-3.2, -2.4) * mm, "end": v(-3.16, -2.41) * mm});
            skLineSegment(sketch, "E315", {"start": v(-3.16, -2.41) * mm, "end": v(-3.13, -2.44) * mm});
            skLineSegment(sketch, "E316", {"start": v(-3.13, -2.44) * mm, "end": v(-3.04, -2.54) * mm});
            skLineSegment(sketch, "E317", {"start": v(-3.04, -2.54) * mm, "end": v(-2.94, -2.68) * mm});
            skLineSegment(sketch, "E318", {"start": v(-2.94, -2.68) * mm, "end": v(-2.87, -2.83) * mm});
            skLineSegment(sketch, "E319", {"start": v(-2.87, -2.83) * mm, "end": v(-2.8, -2.99) * mm});
            skLineSegment(sketch, "E320", {"start": v(-2.8, -2.99) * mm, "end": v(-2.8, -3.03) * mm});
            skLineSegment(sketch, "E321", {"start": v(-2.8, -3.03) * mm, "end": v(-2.78, -3.07) * mm});
            skLineSegment(sketch, "E322", {"start": v(-2.78, -3.07) * mm, "end": v(-2.77, -3.1) * mm});
            skLineSegment(sketch, "E323", {"start": v(-2.77, -3.1) * mm, "end": v(-2.76, -3.13) * mm});
            skLineSegment(sketch, "E324", {"start": v(-2.76, -3.13) * mm, "end": v(-2.74, -3.2) * mm});
            skLineSegment(sketch, "E325", {"start": v(-2.74, -3.2) * mm, "end": v(-2.7, -3.3) * mm});
            skLineSegment(sketch, "E326", {"start": v(-2.7, -3.3) * mm, "end": v(-2.68, -3.45) * mm});
            skLineSegment(sketch, "E327", {"start": v(-2.68, -3.45) * mm, "end": v(-2.65, -3.6) * mm});
            skLineSegment(sketch, "E328", {"start": v(-2.65, -3.6) * mm, "end": v(-2.64, -3.6) * mm});
            skLineSegment(sketch, "E329", {"start": v(-2.64, -3.6) * mm, "end": v(-2.64, -3.54) * mm});
            skLineSegment(sketch, "E330", {"start": v(-2.64, -3.54) * mm, "end": v(-2.64, -3.43) * mm});
            skLineSegment(sketch, "E331", {"start": v(-2.64, -3.43) * mm, "end": v(-2.64, -3.26) * mm});
            skLineSegment(sketch, "E332", {"start": v(-2.64, -3.26) * mm, "end": v(-2.64, -3.05) * mm});
            skLineSegment(sketch, "E333", {"start": v(-2.64, -3.05) * mm, "end": v(-2.64, -2.92) * mm});
            skLineSegment(sketch, "E334", {"start": v(-2.64, -2.92) * mm, "end": v(-2.65, -2.83) * mm});
            skLineSegment(sketch, "E335", {"start": v(-2.65, -2.83) * mm, "end": v(-2.66, -2.77) * mm});
            skLineSegment(sketch, "E336", {"start": v(-2.66, -2.77) * mm, "end": v(-2.71, -2.54) * mm});
            skLineSegment(sketch, "E337", {"start": v(-2.71, -2.54) * mm, "end": v(-2.8, -2.3) * mm});
            skLineSegment(sketch, "E338", {"start": v(-2.8, -2.3) * mm, "end": v(-2.83, -2.2) * mm});
            skLineSegment(sketch, "E339", {"start": v(-2.83, -2.2) * mm, "end": v(-2.86, -2.11) * mm});
            skLineSegment(sketch, "E340", {"start": v(-2.86, -2.11) * mm, "end": v(-2.88, -2.04) * mm});
            skLineSegment(sketch, "E341", {"start": v(-2.88, -2.04) * mm, "end": v(-2.9, -1.98) * mm});
            skLineSegment(sketch, "E342", {"start": v(-2.9, -1.98) * mm, "end": v(-2.92, -1.92) * mm});
            skLineSegment(sketch, "E343", {"start": v(-2.92, -1.92) * mm, "end": v(-2.93, -1.86) * mm});
            skLineSegment(sketch, "E344", {"start": v(-2.93, -1.86) * mm, "end": v(-2.94, -1.8) * mm});
            skLineSegment(sketch, "E345", {"start": v(-2.94, -1.8) * mm, "end": v(-2.95, -1.74) * mm});
            skLineSegment(sketch, "E346", {"start": v(-2.95, -1.74) * mm, "end": v(-2.98, -1.58) * mm});
            skLineSegment(sketch, "E347", {"start": v(-2.98, -1.58) * mm, "end": v(-3.02, -1.46) * mm});
            skLineSegment(sketch, "E348", {"start": v(-3.02, -1.46) * mm, "end": v(-3.06, -1.37) * mm});
            skLineSegment(sketch, "E349", {"start": v(-3.06, -1.37) * mm, "end": v(-3.12, -1.3) * mm});
            skLineSegment(sketch, "E350", {"start": v(-3.12, -1.3) * mm, "end": v(-3.15, -1.27) * mm});
            skLineSegment(sketch, "E351", {"start": v(-3.15, -1.27) * mm, "end": v(-3.15, -1.25) * mm});
            skLineSegment(sketch, "E352", {"start": v(-3.15, -1.25) * mm, "end": v(-3.14, -1.24) * mm});
            skLineSegment(sketch, "E353", {"start": v(-3.14, -1.24) * mm, "end": v(-3.12, -1.24) * mm});
            skLineSegment(sketch, "E354", {"start": v(-3.12, -1.24) * mm, "end": v(-3.1, -1.26) * mm});
            skLineSegment(sketch, "E355", {"start": v(-3.1, -1.26) * mm, "end": v(-3.06, -1.28) * mm});
            skLineSegment(sketch, "E356", {"start": v(-3.06, -1.28) * mm, "end": v(-3.02, -1.3) * mm});
            skLineSegment(sketch, "E357", {"start": v(-3.02, -1.3) * mm, "end": v(-2.99, -1.34) * mm});
            skLineSegment(sketch, "E358", {"start": v(-2.99, -1.34) * mm, "end": v(-2.87, -1.47) * mm});
            skLineSegment(sketch, "E359", {"start": v(-2.87, -1.47) * mm, "end": v(-2.78, -1.63) * mm});
            skLineSegment(sketch, "E360", {"start": v(-2.78, -1.63) * mm, "end": v(-2.7, -1.8) * mm});
            skLineSegment(sketch, "E361", {"start": v(-2.7, -1.8) * mm, "end": v(-2.66, -2.01) * mm});
            skLineSegment(sketch, "E362", {"start": v(-2.66, -2.01) * mm, "end": v(-2.64, -2.13) * mm});
            skLineSegment(sketch, "E363", {"start": v(-2.64, -2.13) * mm, "end": v(-2.62, -2.28) * mm});
            skLineSegment(sketch, "E364", {"start": v(-2.62, -2.28) * mm, "end": v(-2.6, -2.42) * mm});
            skLineSegment(sketch, "E365", {"start": v(-2.6, -2.42) * mm, "end": v(-2.6, -2.52) * mm});
            skLineSegment(sketch, "E366", {"start": v(-2.6, -2.52) * mm, "end": v(-2.6, -2.56) * mm});
            skLineSegment(sketch, "E367", {"start": v(-2.6, -2.56) * mm, "end": v(-2.6, -2.56) * mm});
            skLineSegment(sketch, "E368", {"start": v(-2.6, -2.56) * mm, "end": v(-2.58, -2.54) * mm});
            skLineSegment(sketch, "E369", {"start": v(-2.58, -2.54) * mm, "end": v(-2.57, -2.5) * mm});
            skLineSegment(sketch, "E370", {"start": v(-2.57, -2.5) * mm, "end": v(-2.56, -2.4) * mm});
            skLineSegment(sketch, "E371", {"start": v(-2.56, -2.4) * mm, "end": v(-2.53, -2.28) * mm});
            skLineSegment(sketch, "E372", {"start": v(-2.53, -2.28) * mm, "end": v(-2.5, -2.16) * mm});
            skLineSegment(sketch, "E373", {"start": v(-2.5, -2.16) * mm, "end": v(-2.48, -2.07) * mm});
            skLineSegment(sketch, "E374", {"start": v(-2.48, -2.07) * mm, "end": v(-2.47, -2.04) * mm});
            skLineSegment(sketch, "E375", {"start": v(-2.47, -2.04) * mm, "end": v(-2.46, -2) * mm});
            skLineSegment(sketch, "E376", {"start": v(-2.46, -2) * mm, "end": v(-2.45, -1.95) * mm});
            skLineSegment(sketch, "E377", {"start": v(-2.45, -1.95) * mm, "end": v(-2.44, -1.9) * mm});
            skLineSegment(sketch, "E378", {"start": v(-2.44, -1.9) * mm, "end": v(-2.4, -1.8) * mm});
            skLineSegment(sketch, "E379", {"start": v(-2.4, -1.8) * mm, "end": v(-2.37, -1.69) * mm});
            skLineSegment(sketch, "E380", {"start": v(-2.37, -1.69) * mm, "end": v(-2.33, -1.57) * mm});
            skLineSegment(sketch, "E381", {"start": v(-2.33, -1.57) * mm, "end": v(-2.3, -1.48) * mm});
            skLineSegment(sketch, "E382", {"start": v(-2.3, -1.48) * mm, "end": v(-2.27, -1.42) * mm});
            skLineSegment(sketch, "E383", {"start": v(-2.27, -1.42) * mm, "end": v(-2.27, -1.36) * mm});
            skLineSegment(sketch, "E384", {"start": v(-2.27, -1.36) * mm, "end": v(-2.26, -1.3) * mm});
            skLineSegment(sketch, "E385", {"start": v(-2.26, -1.3) * mm, "end": v(-2.26, -1.24) * mm});
            skLineSegment(sketch, "E386", {"start": v(-2.26, -1.24) * mm, "end": v(-2.25, -1.21) * mm});
            skLineSegment(sketch, "E387", {"start": v(-2.25, -1.21) * mm, "end": v(-2.25, -1.19) * mm});
            skLineSegment(sketch, "E388", {"start": v(-2.25, -1.19) * mm, "end": v(-2.26, -1.17) * mm});
            skLineSegment(sketch, "E389", {"start": v(-2.26, -1.17) * mm, "end": v(-2.28, -1.15) * mm});
            skLineSegment(sketch, "E390", {"start": v(-2.28, -1.15) * mm, "end": v(-2.31, -1.1) * mm});
            skLineSegment(sketch, "E391", {"start": v(-2.31, -1.1) * mm, "end": v(-2.33, -1.05) * mm});
            skLineSegment(sketch, "E392", {"start": v(-2.33, -1.05) * mm, "end": v(-2.35, -0.97) * mm});
            skLineSegment(sketch, "E393", {"start": v(-2.35, -0.97) * mm, "end": v(-2.35, -0.85) * mm});
            skLineSegment(sketch, "E394", {"start": v(-2.35, -0.85) * mm, "end": v(-2.36, -0.77) * mm});
            skLineSegment(sketch, "E395", {"start": v(-2.36, -0.77) * mm, "end": v(-2.35, -0.7) * mm});
            skLineSegment(sketch, "E396", {"start": v(-2.35, -0.7) * mm, "end": v(-2.35, -0.65) * mm});
            skLineSegment(sketch, "E397", {"start": v(-2.35, -0.65) * mm, "end": v(-2.34, -0.59) * mm});
            skLineSegment(sketch, "E398", {"start": v(-2.34, -0.59) * mm, "end": v(-2.31, -0.49) * mm});
            skLineSegment(sketch, "E399", {"start": v(-2.31, -0.49) * mm, "end": v(-2.3, -0.39) * mm});
            skLineSegment(sketch, "E400", {"start": v(-2.3, -0.39) * mm, "end": v(-2.28, -0.29) * mm});
            skLineSegment(sketch, "E401", {"start": v(-2.28, -0.29) * mm, "end": v(-2.26, -0.19) * mm});
            skLineSegment(sketch, "E402", {"start": v(-2.26, -0.19) * mm, "end": v(-2.24, -0.1) * mm});
            skLineSegment(sketch, "E403", {"start": v(-2.24, -0.1) * mm, "end": v(-2.23, -0.02) * mm});
            skLineSegment(sketch, "E404", {"start": v(-2.23, -0.02) * mm, "end": v(-2.23, 0.04) * mm});
            skLineSegment(sketch, "E405", {"start": v(-2.23, 0.04) * mm, "end": v(-2.22, 0.08) * mm});
            skLineSegment(sketch, "E406", {"start": v(-2.22, 0.08) * mm, "end": v(-2.23, 0.12) * mm});
            skLineSegment(sketch, "E407", {"start": v(-2.23, 0.12) * mm, "end": v(-2.27, 0.18) * mm});
            skLineSegment(sketch, "E408", {"start": v(-2.27, 0.18) * mm, "end": v(-2.33, 0.26) * mm});
            skLineSegment(sketch, "E409", {"start": v(-2.33, 0.26) * mm, "end": v(-2.43, 0.37) * mm});
            skLineSegment(sketch, "E410", {"start": v(-2.43, 0.37) * mm, "end": v(-2.51, 0.46) * mm});
            skLineSegment(sketch, "E411", {"start": v(-2.51, 0.46) * mm, "end": v(-2.58, 0.52) * mm});
            skLineSegment(sketch, "E412", {"start": v(-2.58, 0.52) * mm, "end": v(-2.63, 0.56) * mm});
            skLineSegment(sketch, "E413", {"start": v(-2.63, 0.56) * mm, "end": v(-2.7, 0.6) * mm});
            skLineSegment(sketch, "E414", {"start": v(-2.7, 0.6) * mm, "end": v(-2.78, 0.64) * mm});
            skLineSegment(sketch, "E415", {"start": v(-2.78, 0.64) * mm, "end": v(-2.9, 0.67) * mm});
            skLineSegment(sketch, "E416", {"start": v(-2.9, 0.67) * mm, "end": v(-3.02, 0.7) * mm});
            skLineSegment(sketch, "E417", {"start": v(-3.02, 0.7) * mm, "end": v(-3.14, 0.74) * mm});
            skLineSegment(sketch, "E418", {"start": v(-3.14, 0.74) * mm, "end": v(-3.24, 0.75) * mm});
            skLineSegment(sketch, "E419", {"start": v(-3.24, 0.75) * mm, "end": v(-3.34, 0.76) * mm});
            skLineSegment(sketch, "E420", {"start": v(-3.34, 0.76) * mm, "end": v(-3.46, 0.75) * mm});
            skLineSegment(sketch, "E421", {"start": v(-3.46, 0.75) * mm, "end": v(-3.63, 0.73) * mm});
            skLineSegment(sketch, "E422", {"start": v(-3.63, 0.73) * mm, "end": v(-3.74, 0.72) * mm});
            skLineSegment(sketch, "E423", {"start": v(-3.74, 0.72) * mm, "end": v(-3.83, 0.7) * mm});
            skLineSegment(sketch, "E424", {"start": v(-3.83, 0.7) * mm, "end": v(-3.9, 0.7) * mm});
            skLineSegment(sketch, "E425", {"start": v(-3.9, 0.7) * mm, "end": v(-3.94, 0.7) * mm});
            skLineSegment(sketch, "E426", {"start": v(-3.94, 0.7) * mm, "end": v(-3.98, 0.7) * mm});
            skLineSegment(sketch, "E427", {"start": v(-3.98, 0.7) * mm, "end": v(-4, 0.72) * mm});
            skLineSegment(sketch, "E428", {"start": v(-4, 0.72) * mm, "end": v(-4.02, 0.74) * mm});
            skLineSegment(sketch, "E429", {"start": v(-4.02, 0.74) * mm, "end": v(-4.03, 0.76) * mm});
            skLineSegment(sketch, "E430", {"start": v(-4.03, 0.76) * mm, "end": v(-4.04, 0.8) * mm});
            skLineSegment(sketch, "E431", {"start": v(-4.04, 0.8) * mm, "end": v(-4.04, 0.84) * mm});
            skLineSegment(sketch, "E432", {"start": v(-4.04, 0.84) * mm, "end": v(-4.02, 0.88) * mm});
            skLineSegment(sketch, "E433", {"start": v(-4.02, 0.88) * mm, "end": v(-4, 0.93) * mm});
            skLineSegment(sketch, "E434", {"start": v(-4, 0.93) * mm, "end": v(-3.93, 1.03) * mm});
            skLineSegment(sketch, "E435", {"start": v(-3.93, 1.03) * mm, "end": v(-3.9, 1.1) * mm});
            skLineSegment(sketch, "E436", {"start": v(-3.9, 1.1) * mm, "end": v(-3.9, 1.17) * mm});
            skLineSegment(sketch, "E437", {"start": v(-3.9, 1.17) * mm, "end": v(-3.94, 1.24) * mm});
            skLineSegment(sketch, "E438", {"start": v(-3.94, 1.24) * mm, "end": v(-3.97, 1.32) * mm});
            skLineSegment(sketch, "E439", {"start": v(-3.97, 1.32) * mm, "end": v(-3.98, 1.43) * mm});
            skLineSegment(sketch, "E440", {"start": v(-3.98, 1.43) * mm, "end": v(-3.95, 1.54) * mm});
            skLineSegment(sketch, "E441", {"start": v(-3.95, 1.54) * mm, "end": v(-3.9, 1.66) * mm});
            skLineSegment(sketch, "E442", {"start": v(-3.9, 1.66) * mm, "end": v(-3.89, 1.7) * mm});
            skLineSegment(sketch, "E443", {"start": v(-3.89, 1.7) * mm, "end": v(-3.88, 1.73) * mm});
            skLineSegment(sketch, "E444", {"start": v(-3.88, 1.73) * mm, "end": v(-3.88, 1.78) * mm});
            skLineSegment(sketch, "E445", {"start": v(-3.88, 1.78) * mm, "end": v(-3.88, 1.86) * mm});
            skLineSegment(sketch, "E446", {"start": v(-3.88, 1.86) * mm, "end": v(-3.88, 1.94) * mm});
            skLineSegment(sketch, "E447", {"start": v(-3.88, 1.94) * mm, "end": v(-3.87, 1.98) * mm});
            skLineSegment(sketch, "E448", {"start": v(-3.87, 1.98) * mm, "end": v(-3.87, 2.01) * mm});
            skLineSegment(sketch, "E449", {"start": v(-3.87, 2.01) * mm, "end": v(-3.85, 2.04) * mm});
            skLineSegment(sketch, "E450", {"start": v(-3.85, 2.04) * mm, "end": v(-3.82, 2.07) * mm});
            skLineSegment(sketch, "E451", {"start": v(-3.82, 2.07) * mm, "end": v(-3.76, 2.11) * mm});
            skLineSegment(sketch, "E452", {"start": v(-3.76, 2.11) * mm, "end": v(-3.7, 2.14) * mm});
            skLineSegment(sketch, "E453", {"start": v(-3.7, 2.14) * mm, "end": v(-3.62, 2.16) * mm});
            skLineSegment(sketch, "E454", {"start": v(-3.62, 2.16) * mm, "end": v(-3.52, 2.18) * mm});
            skLineSegment(sketch, "E455", {"start": v(-3.52, 2.18) * mm, "end": v(-3.39, 2.18) * mm});
            skLineSegment(sketch, "E456", {"start": v(-3.39, 2.18) * mm, "end": v(-3.25, 2.17) * mm});
            skLineSegment(sketch, "E457", {"start": v(-3.25, 2.17) * mm, "end": v(-3.13, 2.14) * mm});
            skLineSegment(sketch, "E458", {"start": v(-3.13, 2.14) * mm, "end": v(-2.92, 2.07) * mm});
            skLineSegment(sketch, "E459", {"start": v(-2.92, 2.07) * mm, "end": v(-2.7, 1.95) * mm});
            skLineSegment(sketch, "E460", {"start": v(-2.7, 1.95) * mm, "end": v(-2.66, 1.92) * mm});
            skLineSegment(sketch, "E461", {"start": v(-2.66, 1.92) * mm, "end": v(-2.62, 1.9) * mm});
            skLineSegment(sketch, "E462", {"start": v(-2.62, 1.9) * mm, "end": v(-2.58, 1.87) * mm});
            skLineSegment(sketch, "E463", {"start": v(-2.58, 1.87) * mm, "end": v(-2.55, 1.85) * mm});
            skLineSegment(sketch, "E464", {"start": v(-2.55, 1.85) * mm, "end": v(-2.53, 1.84) * mm});
            skLineSegment(sketch, "E465", {"start": v(-2.53, 1.84) * mm, "end": v(-2.5, 1.81) * mm});
            skLineSegment(sketch, "E466", {"start": v(-2.5, 1.81) * mm, "end": v(-2.47, 1.8) * mm});
            skLineSegment(sketch, "E467", {"start": v(-2.47, 1.8) * mm, "end": v(-2.44, 1.77) * mm});
            skLineSegment(sketch, "E468", {"start": v(-2.44, 1.77) * mm, "end": v(-2.42, 1.75) * mm});
            skLineSegment(sketch, "E469", {"start": v(-2.42, 1.75) * mm, "end": v(-2.4, 1.73) * mm});
            skLineSegment(sketch, "E470", {"start": v(-2.4, 1.73) * mm, "end": v(-2.37, 1.72) * mm});
            skLineSegment(sketch, "E471", {"start": v(-2.37, 1.72) * mm, "end": v(-2.36, 1.7) * mm});
            skLineSegment(sketch, "E472", {"start": v(-2.36, 1.7) * mm, "end": v(-2.32, 1.68) * mm});
            skLineSegment(sketch, "E473", {"start": v(-2.32, 1.68) * mm, "end": v(-2.27, 1.62) * mm});
            skLineSegment(sketch, "E474", {"start": v(-2.27, 1.62) * mm, "end": v(-2.2, 1.55) * mm});
            skLineSegment(sketch, "E475", {"start": v(-2.2, 1.55) * mm, "end": v(-2.16, 1.48) * mm});
            skLineSegment(sketch, "E476", {"start": v(-2.16, 1.48) * mm, "end": v(-2.12, 1.42) * mm});
            skLineSegment(sketch, "E477", {"start": v(-2.12, 1.42) * mm, "end": v(-2.07, 1.33) * mm});
            skLineSegment(sketch, "E478", {"start": v(-2.07, 1.33) * mm, "end": v(-2, 1.19) * mm});
            skLineSegment(sketch, "E479", {"start": v(-2, 1.19) * mm, "end": v(-1.9, 1) * mm});
            skLineSegment(sketch, "E480", {"start": v(-1.9, 1) * mm, "end": v(-1.89, 0.94) * mm});
            skLineSegment(sketch, "E481", {"start": v(-1.89, 0.94) * mm, "end": v(-1.87, 0.88) * mm});
            skLineSegment(sketch, "E482", {"start": v(-1.87, 0.88) * mm, "end": v(-1.85, 0.8) * mm});
            skLineSegment(sketch, "E483", {"start": v(-1.85, 0.8) * mm, "end": v(-1.82, 0.7) * mm});
            skLineSegment(sketch, "E484", {"start": v(-1.82, 0.7) * mm, "end": v(-1.79, 0.46) * mm});
            skLineSegment(sketch, "E485", {"start": v(-1.79, 0.46) * mm, "end": v(-1.78, 0.2) * mm});
            skLineSegment(sketch, "E486", {"start": v(-1.78, 0.2) * mm, "end": v(-1.79, 0.07) * mm});
            skLineSegment(sketch, "E487", {"start": v(-1.79, 0.07) * mm, "end": v(-1.8, -0.04) * mm});
            skLineSegment(sketch, "E488", {"start": v(-1.8, -0.04) * mm, "end": v(-1.8, -0.14) * mm});
            skLineSegment(sketch, "E489", {"start": v(-1.8, -0.14) * mm, "end": v(-1.82, -0.22) * mm});
            skLineSegment(sketch, "E490", {"start": v(-1.82, -0.22) * mm, "end": v(-1.82, -0.23) * mm});
            skLineSegment(sketch, "E491", {"start": v(-1.82, -0.23) * mm, "end": v(-1.82, -0.24) * mm});
            skLineSegment(sketch, "E492", {"start": v(-1.82, -0.24) * mm, "end": v(-1.81, -0.23) * mm});
            skLineSegment(sketch, "E493", {"start": v(-1.81, -0.23) * mm, "end": v(-1.8, -0.21) * mm});
            skLineSegment(sketch, "E494", {"start": v(-1.8, -0.21) * mm, "end": v(-1.79, -0.15) * mm});
            skLineSegment(sketch, "E495", {"start": v(-1.79, -0.15) * mm, "end": v(-1.77, -0.07) * mm});
            skLineSegment(sketch, "E496", {"start": v(-1.77, -0.07) * mm, "end": v(-1.76, 0.04) * mm});
            skLineSegment(sketch, "E497", {"start": v(-1.76, 0.04) * mm, "end": v(-1.75, 0.15) * mm});
            skLineSegment(sketch, "E498", {"start": v(-1.75, 0.15) * mm, "end": v(-1.75, 0.3) * mm});
            skLineSegment(sketch, "E499", {"start": v(-1.75, 0.3) * mm, "end": v(-1.77, 0.47) * mm});
            skLineSegment(sketch, "E500", {"start": v(-1.77, 0.47) * mm, "end": v(-1.8, 0.68) * mm});
            skLineSegment(sketch, "E501", {"start": v(-1.8, 0.68) * mm, "end": v(-1.85, 0.91) * mm});
            skLineSegment(sketch, "E502", {"start": v(-1.85, 0.91) * mm, "end": v(-1.9, 1.1) * mm});
            skLineSegment(sketch, "E503", {"start": v(-1.9, 1.1) * mm, "end": v(-1.95, 1.28) * mm});
            skLineSegment(sketch, "E504", {"start": v(-1.95, 1.28) * mm, "end": v(-2, 1.43) * mm});
            skLineSegment(sketch, "E505", {"start": v(-2, 1.43) * mm, "end": v(-2.06, 1.53) * mm});
            skLineSegment(sketch, "E506", {"start": v(-2.06, 1.53) * mm, "end": v(-2.08, 1.57) * mm});
            skLineSegment(sketch, "E507", {"start": v(-2.08, 1.57) * mm, "end": v(-2.09, 1.6) * mm});
            skLineSegment(sketch, "E508", {"start": v(-2.09, 1.6) * mm, "end": v(-2.1, 1.6) * mm});
            skLineSegment(sketch, "E509", {"start": v(-2.1, 1.6) * mm, "end": v(-2.12, 1.63) * mm});
            skLineSegment(sketch, "E510", {"start": v(-2.12, 1.63) * mm, "end": v(-2.15, 1.66) * mm});
            skLineSegment(sketch, "E511", {"start": v(-2.15, 1.66) * mm, "end": v(-2.19, 1.7) * mm});
            skLineSegment(sketch, "E512", {"start": v(-2.19, 1.7) * mm, "end": v(-2.23, 1.74) * mm});
            skLineSegment(sketch, "E513", {"start": v(-2.23, 1.74) * mm, "end": v(-2.27, 1.78) * mm});
            skLineSegment(sketch, "E514", {"start": v(-2.27, 1.78) * mm, "end": v(-2.3, 1.8) * mm});
            skLineSegment(sketch, "E515", {"start": v(-2.3, 1.8) * mm, "end": v(-2.34, 1.83) * mm});
            skLineSegment(sketch, "E516", {"start": v(-2.34, 1.83) * mm, "end": v(-2.37, 1.85) * mm});
            skLineSegment(sketch, "E517", {"start": v(-2.37, 1.85) * mm, "end": v(-2.41, 1.88) * mm});
            skLineSegment(sketch, "E518", {"start": v(-2.41, 1.88) * mm, "end": v(-2.45, 1.9) * mm});
            skLineSegment(sketch, "E519", {"start": v(-2.45, 1.9) * mm, "end": v(-2.49, 1.92) * mm});
            skLineSegment(sketch, "E520", {"start": v(-2.49, 1.92) * mm, "end": v(-2.6, 1.99) * mm});
            skLineSegment(sketch, "E521", {"start": v(-2.6, 1.99) * mm, "end": v(-2.72, 2.06) * mm});
            skLineSegment(sketch, "E522", {"start": v(-2.72, 2.06) * mm, "end": v(-2.8, 2.13) * mm});
            skLineSegment(sketch, "E523", {"start": v(-2.8, 2.13) * mm, "end": v(-2.85, 2.2) * mm});
            skLineSegment(sketch, "E524", {"start": v(-2.85, 2.2) * mm, "end": v(-2.85, 2.23) * mm});
            skLineSegment(sketch, "E525", {"start": v(-2.85, 2.23) * mm, "end": v(-2.85, 2.27) * mm});
            skLineSegment(sketch, "E526", {"start": v(-2.85, 2.27) * mm, "end": v(-2.84, 2.32) * mm});
            skLineSegment(sketch, "E527", {"start": v(-2.84, 2.32) * mm, "end": v(-2.82, 2.36) * mm});
            skLineSegment(sketch, "E528", {"start": v(-2.82, 2.36) * mm, "end": v(-2.8, 2.39) * mm});
            skLineSegment(sketch, "E529", {"start": v(-2.8, 2.39) * mm, "end": v(-2.8, 2.4) * mm});
            skLineSegment(sketch, "E530", {"start": v(-2.8, 2.4) * mm, "end": v(-2.78, 2.42) * mm});
            skLineSegment(sketch, "E531", {"start": v(-2.78, 2.42) * mm, "end": v(-2.73, 2.44) * mm});
            skLineSegment(sketch, "E532", {"start": v(-2.73, 2.44) * mm, "end": v(-2.65, 2.46) * mm});
            skLineSegment(sketch, "E533", {"start": v(-2.65, 2.46) * mm, "end": v(-2.56, 2.48) * mm});
            skLineSegment(sketch, "E534", {"start": v(-2.56, 2.48) * mm, "end": v(-2.44, 2.5) * mm});
            skLineSegment(sketch, "E535", {"start": v(-2.44, 2.5) * mm, "end": v(-2.28, 2.5) * mm});
            skLineSegment(sketch, "E536", {"start": v(-2.28, 2.5) * mm, "end": v(-2.12, 2.51) * mm});
            skLineSegment(sketch, "E537", {"start": v(-2.12, 2.51) * mm, "end": v(-2.07, 2.56) * mm});
            skLineSegment(sketch, "E538", {"start": v(-2.07, 2.56) * mm, "end": v(-2.03, 2.6) * mm});
            skLineSegment(sketch, "E539", {"start": v(-2.03, 2.6) * mm, "end": v(-1.98, 2.65) * mm});
            skLineSegment(sketch, "E540", {"start": v(-1.98, 2.65) * mm, "end": v(-1.93, 2.69) * mm});
            skLineSegment(sketch, "E541", {"start": v(-1.93, 2.69) * mm, "end": v(-1.88, 2.71) * mm});
            skLineSegment(sketch, "E542", {"start": v(-1.88, 2.71) * mm, "end": v(-1.85, 2.73) * mm});
            skLineSegment(sketch, "E543", {"start": v(-1.85, 2.73) * mm, "end": v(-1.83, 2.73) * mm});
            skLineSegment(sketch, "E544", {"start": v(-1.83, 2.73) * mm, "end": v(-1.81, 2.73) * mm});
            skLineSegment(sketch, "E545", {"start": v(-1.81, 2.73) * mm, "end": v(-1.78, 2.72) * mm});
            skLineSegment(sketch, "E546", {"start": v(-1.78, 2.72) * mm, "end": v(-1.73, 2.72) * mm});
            skLineSegment(sketch, "E547", {"start": v(-1.73, 2.72) * mm, "end": v(-1.69, 2.73) * mm});
            skLineSegment(sketch, "E548", {"start": v(-1.69, 2.73) * mm, "end": v(-1.64, 2.76) * mm});
            skLineSegment(sketch, "E549", {"start": v(-1.64, 2.76) * mm, "end": v(-1.57, 2.8) * mm});
            skLineSegment(sketch, "E550", {"start": v(-1.57, 2.8) * mm, "end": v(-1.49, 2.87) * mm});
            skLineSegment(sketch, "E551", {"start": v(-1.49, 2.87) * mm, "end": v(-1.42, 2.9) * mm});
            skLineSegment(sketch, "E552", {"start": v(-1.42, 2.9) * mm, "end": v(-1.35, 2.9) * mm});
            skLineSegment(sketch, "E553", {"start": v(-1.35, 2.9) * mm, "end": v(-1.25, 2.88) * mm});
            skLineSegment(sketch, "E554", {"start": v(-1.25, 2.88) * mm, "end": v(-1.2, 2.87) * mm});
            skLineSegment(sketch, "E555", {"start": v(-1.2, 2.87) * mm, "end": v(-1.16, 2.86) * mm});
            skLineSegment(sketch, "E556", {"start": v(-1.16, 2.86) * mm, "end": v(-1.13, 2.84) * mm});
            skLineSegment(sketch, "E557", {"start": v(-1.13, 2.84) * mm, "end": v(-1.1, 2.81) * mm});
            skLineSegment(sketch, "E558", {"start": v(-1.1, 2.81) * mm, "end": v(-1.06, 2.75) * mm});
            skLineSegment(sketch, "E559", {"start": v(-1.06, 2.75) * mm, "end": v(-1.02, 2.68) * mm});
            skLineSegment(sketch, "E560", {"start": v(-1.02, 2.68) * mm, "end": v(-0.98, 2.6) * mm});
            skLineSegment(sketch, "E561", {"start": v(-0.98, 2.6) * mm, "end": v(-0.95, 2.5) * mm});
            skLineSegment(sketch, "E562", {"start": v(-0.95, 2.5) * mm, "end": v(-0.93, 2.45) * mm});
            skLineSegment(sketch, "E563", {"start": v(-0.93, 2.45) * mm, "end": v(-0.92, 2.41) * mm});
            skLineSegment(sketch, "E564", {"start": v(-0.92, 2.41) * mm, "end": v(-0.9, 2.38) * mm});
            skLineSegment(sketch, "E565", {"start": v(-0.9, 2.38) * mm, "end": v(-0.9, 2.36) * mm});
            skLineSegment(sketch, "E566", {"start": v(-0.9, 2.36) * mm, "end": v(-0.89, 2.33) * mm});
            skLineSegment(sketch, "E567", {"start": v(-0.89, 2.33) * mm, "end": v(-0.88, 2.26) * mm});
            skLineSegment(sketch, "E568", {"start": v(-0.88, 2.26) * mm, "end": v(-0.87, 2.17) * mm});
            skLineSegment(sketch, "E569", {"start": v(-0.87, 2.17) * mm, "end": v(-0.86, 2.05) * mm});
            skLineSegment(sketch, "E570", {"start": v(-0.86, 2.05) * mm, "end": v(-0.86, 1.93) * mm});
            skLineSegment(sketch, "E571", {"start": v(-0.86, 1.93) * mm, "end": v(-0.86, 1.8) * mm});
            skLineSegment(sketch, "E572", {"start": v(-0.86, 1.8) * mm, "end": v(-0.86, 1.68) * mm});
            skLineSegment(sketch, "E573", {"start": v(-0.86, 1.68) * mm, "end": v(-0.87, 1.56) * mm});
            skLineSegment(sketch, "E574", {"start": v(-0.87, 1.56) * mm, "end": v(-0.87, 1.47) * mm});
            skLineSegment(sketch, "E575", {"start": v(-0.87, 1.47) * mm, "end": v(-0.88, 1.39) * mm});
            skLineSegment(sketch, "E576", {"start": v(-0.88, 1.39) * mm, "end": v(-0.9, 1.31) * mm});
            skLineSegment(sketch, "E577", {"start": v(-0.9, 1.31) * mm, "end": v(-0.92, 1.22) * mm});
            skLineSegment(sketch, "E578", {"start": v(-0.92, 1.22) * mm, "end": v(-0.98, 1.04) * mm});
            skLineSegment(sketch, "E579", {"start": v(-0.98, 1.04) * mm, "end": v(-1.02, 0.9) * mm});
            skLineSegment(sketch, "E580", {"start": v(-1.02, 0.9) * mm, "end": v(-1.06, 0.8) * mm});
            skLineSegment(sketch, "E581", {"start": v(-1.06, 0.8) * mm, "end": v(-1.1, 0.72) * mm});
            skLineSegment(sketch, "E582", {"start": v(-1.1, 0.72) * mm, "end": v(-1.14, 0.62) * mm});
            skLineSegment(sketch, "E583", {"start": v(-1.14, 0.62) * mm, "end": v(-1.19, 0.5) * mm});
            skLineSegment(sketch, "E584", {"start": v(-1.19, 0.5) * mm, "end": v(-1.22, 0.4) * mm});
            skLineSegment(sketch, "E585", {"start": v(-1.22, 0.4) * mm, "end": v(-1.23, 0.33) * mm});
            skLineSegment(sketch, "E586", {"start": v(-1.23, 0.33) * mm, "end": v(-1.23, 0.3) * mm});
            skLineSegment(sketch, "E587", {"start": v(-1.23, 0.3) * mm, "end": v(-1.23, 0.3) * mm});
            skLineSegment(sketch, "E588", {"start": v(-1.23, 0.3) * mm, "end": v(-1.22, 0.3) * mm});
            skLineSegment(sketch, "E589", {"start": v(-1.22, 0.3) * mm, "end": v(-1.2, 0.32) * mm});
            skLineSegment(sketch, "E590", {"start": v(-1.2, 0.32) * mm, "end": v(-1.2, 0.35) * mm});
            skLineSegment(sketch, "E591", {"start": v(-1.2, 0.35) * mm, "end": v(-1.18, 0.38) * mm});
            skLineSegment(sketch, "E592", {"start": v(-1.18, 0.38) * mm, "end": v(-1.16, 0.43) * mm});
            skLineSegment(sketch, "E593", {"start": v(-1.16, 0.43) * mm, "end": v(-1.14, 0.48) * mm});
            skLineSegment(sketch, "E594", {"start": v(-1.14, 0.48) * mm, "end": v(-1.13, 0.53) * mm});
            skLineSegment(sketch, "E595", {"start": v(-1.13, 0.53) * mm, "end": v(-1.1, 0.58) * mm});
            skLineSegment(sketch, "E596", {"start": v(-1.1, 0.58) * mm, "end": v(-1.08, 0.63) * mm});
            skLineSegment(sketch, "E597", {"start": v(-1.08, 0.63) * mm, "end": v(-1.06, 0.68) * mm});
            skLineSegment(sketch, "E598", {"start": v(-1.06, 0.68) * mm, "end": v(-1.04, 0.72) * mm});
            skLineSegment(sketch, "E599", {"start": v(-1.04, 0.72) * mm, "end": v(-1.02, 0.76) * mm});
            skLineSegment(sketch, "E600", {"start": v(-1.02, 0.76) * mm, "end": v(-1, 0.8) * mm});
            skLineSegment(sketch, "E601", {"start": v(-1, 0.8) * mm, "end": v(-1, 0.8) * mm});
            skLineSegment(sketch, "E602", {"start": v(-1, 0.8) * mm, "end": v(-1, 0.82) * mm});
            skLineSegment(sketch, "E603", {"start": v(-1, 0.82) * mm, "end": v(-0.98, 0.85) * mm});
            skLineSegment(sketch, "E604", {"start": v(-0.98, 0.85) * mm, "end": v(-0.96, 0.89) * mm});
            skLineSegment(sketch, "E605", {"start": v(-0.96, 0.89) * mm, "end": v(-0.93, 0.92) * mm});
            skLineSegment(sketch, "E606", {"start": v(-0.93, 0.92) * mm, "end": v(-0.87, 1.04) * mm});
            skLineSegment(sketch, "E607", {"start": v(-0.87, 1.04) * mm, "end": v(-0.8, 1.17) * mm});
            skLineSegment(sketch, "E608", {"start": v(-0.8, 1.17) * mm, "end": v(-0.75, 1.3) * mm});
            skLineSegment(sketch, "E609", {"start": v(-0.75, 1.3) * mm, "end": v(-0.71, 1.42) * mm});
            skLineSegment(sketch, "E610", {"start": v(-0.71, 1.42) * mm, "end": v(-0.7, 1.47) * mm});
            skLineSegment(sketch, "E611", {"start": v(-0.7, 1.47) * mm, "end": v(-0.65, 1.55) * mm});
            skLineSegment(sketch, "E612", {"start": v(-0.65, 1.55) * mm, "end": v(-0.6, 1.64) * mm});
            skLineSegment(sketch, "E613", {"start": v(-0.6, 1.64) * mm, "end": v(-0.55, 1.75) * mm});
            skLineSegment(sketch, "E614", {"start": v(-0.55, 1.75) * mm, "end": v(-0.5, 1.85) * mm});
            skLineSegment(sketch, "E615", {"start": v(-0.5, 1.85) * mm, "end": v(-0.45, 1.94) * mm});
            skLineSegment(sketch, "E616", {"start": v(-0.45, 1.94) * mm, "end": v(-0.4, 2.02) * mm});
            skLineSegment(sketch, "E617", {"start": v(-0.4, 2.02) * mm, "end": v(-0.37, 2.06) * mm});
            skLineSegment(sketch, "E618", {"start": v(-0.37, 2.06) * mm, "end": v(-0.3, 2.13) * mm});
            skLineSegment(sketch, "E619", {"start": v(-0.3, 2.13) * mm, "end": v(-0.22, 2.2) * mm});
            skLineSegment(sketch, "E620", {"start": v(-0.22, 2.2) * mm, "end": v(-0.15, 2.27) * mm});
            skLineSegment(sketch, "E621", {"start": v(-0.15, 2.27) * mm, "end": v(-0.08, 2.31) * mm});
            skLineSegment(sketch, "E622", {"start": v(-0.08, 2.31) * mm, "end": v(0, 2.34) * mm});
            skLineSegment(sketch, "E623", {"start": v(0, 2.34) * mm, "end": v(0.08, 2.33) * mm});
            skLineSegment(sketch, "E624", {"start": v(0.08, 2.33) * mm, "end": v(0.15, 2.3) * mm});
            skLineSegment(sketch, "E625", {"start": v(0.15, 2.3) * mm, "end": v(0.2, 2.23) * mm});
            skLineSegment(sketch, "E626", {"start": v(0.2, 2.23) * mm, "end": v(0.24, 2.18) * mm});
            skLineSegment(sketch, "E627", {"start": v(0.24, 2.18) * mm, "end": v(0.32, 2.17) * mm});
            skLineSegment(sketch, "E628", {"start": v(0.32, 2.17) * mm, "end": v(0.4, 2.17) * mm});
            skLineSegment(sketch, "E629", {"start": v(0.4, 2.17) * mm, "end": v(0.45, 2.15) * mm});
            skLineSegment(sketch, "E630", {"start": v(0.45, 2.15) * mm, "end": v(0.5, 2.13) * mm});
            skLineSegment(sketch, "E631", {"start": v(0.5, 2.13) * mm, "end": v(0.56, 2.1) * mm});
            skLineSegment(sketch, "E632", {"start": v(0.56, 2.1) * mm, "end": v(0.6, 2.07) * mm});
            skLineSegment(sketch, "E633", {"start": v(0.6, 2.07) * mm, "end": v(0.64, 2.03) * mm});
            skLineSegment(sketch, "E634", {"start": v(0.64, 2.03) * mm, "end": v(0.66, 2) * mm});
            skLineSegment(sketch, "E635", {"start": v(0.66, 2) * mm, "end": v(0.67, 1.95) * mm});
            skLineSegment(sketch, "E636", {"start": v(0.67, 1.95) * mm, "end": v(0.67, 1.9) * mm});
            skLineSegment(sketch, "E637", {"start": v(0.67, 1.9) * mm, "end": v(0.7, 1.87) * mm});
            skLineSegment(sketch, "E638", {"start": v(0.7, 1.87) * mm, "end": v(0.75, 1.84) * mm});
            skLineSegment(sketch, "E639", {"start": v(0.75, 1.84) * mm, "end": v(0.82, 1.8) * mm});
            skLineSegment(sketch, "E640", {"start": v(0.82, 1.8) * mm, "end": v(0.96, 1.76) * mm});
            skLineSegment(sketch, "E641", {"start": v(0.96, 1.76) * mm, "end": v(1.05, 1.7) * mm});
            skLineSegment(sketch, "E642", {"start": v(1.05, 1.7) * mm, "end": v(1.12, 1.65) * mm});
            skLineSegment(sketch, "E643", {"start": v(1.12, 1.65) * mm, "end": v(1.18, 1.57) * mm});
            skLineSegment(sketch, "E644", {"start": v(1.18, 1.57) * mm, "end": v(1.2, 1.53) * mm});
            skLineSegment(sketch, "E645", {"start": v(1.2, 1.53) * mm, "end": v(1.2, 1.48) * mm});
            skLineSegment(sketch, "E646", {"start": v(1.2, 1.48) * mm, "end": v(1.2, 1.44) * mm});
            skLineSegment(sketch, "E647", {"start": v(1.2, 1.44) * mm, "end": v(1.18, 1.4) * mm});
            skLineSegment(sketch, "E648", {"start": v(1.18, 1.4) * mm, "end": v(1.14, 1.33) * mm});
            skLineSegment(sketch, "E649", {"start": v(1.14, 1.33) * mm, "end": v(1.07, 1.26) * mm});
            skLineSegment(sketch, "E650", {"start": v(1.07, 1.26) * mm, "end": v(1, 1.19) * mm});
            skLineSegment(sketch, "E651", {"start": v(1, 1.19) * mm, "end": v(0.92, 1.13) * mm});
            skLineSegment(sketch, "E652", {"start": v(0.92, 1.13) * mm, "end": v(0.88, 1.1) * mm});
            skLineSegment(sketch, "E653", {"start": v(0.88, 1.1) * mm, "end": v(0.84, 1.07) * mm});
            skLineSegment(sketch, "E654", {"start": v(0.84, 1.07) * mm, "end": v(0.8, 1.04) * mm});
            skLineSegment(sketch, "E655", {"start": v(0.8, 1.04) * mm, "end": v(0.77, 1.02) * mm});
            skLineSegment(sketch, "E656", {"start": v(0.77, 1.02) * mm, "end": v(0.75, 1) * mm});
            skLineSegment(sketch, "E657", {"start": v(0.75, 1) * mm, "end": v(0.73, 0.98) * mm});
            skLineSegment(sketch, "E658", {"start": v(0.73, 0.98) * mm, "end": v(0.71, 0.97) * mm});
            skLineSegment(sketch, "E659", {"start": v(0.71, 0.97) * mm, "end": v(0.7, 0.96) * mm});
            skLineSegment(sketch, "E660", {"start": v(0.7, 0.96) * mm, "end": v(0.68, 0.96) * mm});
            skLineSegment(sketch, "E661", {"start": v(0.68, 0.96) * mm, "end": v(0.67, 0.95) * mm});
            skLineSegment(sketch, "E662", {"start": v(0.67, 0.95) * mm, "end": v(0.64, 0.95) * mm});
            skLineSegment(sketch, "E663", {"start": v(0.64, 0.95) * mm, "end": v(0.61, 0.94) * mm});
            skLineSegment(sketch, "E664", {"start": v(0.61, 0.94) * mm, "end": v(0.5, 0.9) * mm});
            skLineSegment(sketch, "E665", {"start": v(0.5, 0.9) * mm, "end": v(0.4, 0.87) * mm});
            skLineSegment(sketch, "E666", {"start": v(0.4, 0.87) * mm, "end": v(0.32, 0.84) * mm});
            skLineSegment(sketch, "E667", {"start": v(0.32, 0.84) * mm, "end": v(0.23, 0.8) * mm});
            skLineSegment(sketch, "E668", {"start": v(0.23, 0.8) * mm, "end": v(0.03, 0.72) * mm});
            skLineSegment(sketch, "E669", {"start": v(0.03, 0.72) * mm, "end": v(-0.17, 0.6) * mm});
            skLineSegment(sketch, "E670", {"start": v(-0.17, 0.6) * mm, "end": v(-0.37, 0.49) * mm});
            skLineSegment(sketch, "E671", {"start": v(-0.37, 0.49) * mm, "end": v(-0.55, 0.36) * mm});
            skLineSegment(sketch, "E672", {"start": v(-0.55, 0.36) * mm, "end": v(-0.6, 0.33) * mm});
            skLineSegment(sketch, "E673", {"start": v(-0.6, 0.33) * mm, "end": v(-0.65, 0.28) * mm});
            skLineSegment(sketch, "E674", {"start": v(-0.65, 0.28) * mm, "end": v(-0.71, 0.22) * mm});
            skLineSegment(sketch, "E675", {"start": v(-0.71, 0.22) * mm, "end": v(-0.78, 0.16) * mm});
            skLineSegment(sketch, "E676", {"start": v(-0.78, 0.16) * mm, "end": v(-0.84, 0.1) * mm});
            skLineSegment(sketch, "E677", {"start": v(-0.84, 0.1) * mm, "end": v(-0.9, 0.05) * mm});
            skLineSegment(sketch, "E678", {"start": v(-0.9, 0.05) * mm, "end": v(-0.93, 0.02) * mm});
            skLineSegment(sketch, "E679", {"start": v(-0.93, 0.02) * mm, "end": v(-0.95, 0) * mm});
            skLineSegment(sketch, "E680", {"start": v(-0.95, 0) * mm, "end": v(-0.95, 0) * mm});
            skLineSegment(sketch, "E681", {"start": v(-0.95, 0) * mm, "end": v(-0.97, -0.03) * mm});
            skLineSegment(sketch, "E682", {"start": v(-0.97, -0.03) * mm, "end": v(-1, -0.06) * mm});
            skLineSegment(sketch, "E683", {"start": v(-1, -0.06) * mm, "end": v(-1.03, -0.1) * mm});
            skLineSegment(sketch, "E684", {"start": v(-1.03, -0.1) * mm, "end": v(-1.06, -0.13) * mm});
            skLineSegment(sketch, "E685", {"start": v(-1.06, -0.13) * mm, "end": v(-1.09, -0.16) * mm});
            skLineSegment(sketch, "E686", {"start": v(-1.09, -0.16) * mm, "end": v(-1.1, -0.18) * mm});
            skLineSegment(sketch, "E687", {"start": v(-1.1, -0.18) * mm, "end": v(-1.1, -0.2) * mm});
            skLineSegment(sketch, "E688", {"start": v(-1.1, -0.2) * mm, "end": v(-1.1, -0.2) * mm});
            skLineSegment(sketch, "E689", {"start": v(-1.1, -0.2) * mm, "end": v(-1.08, -0.2) * mm});
            skLineSegment(sketch, "E690", {"start": v(-1.08, -0.2) * mm, "end": v(-1.06, -0.18) * mm});
            skLineSegment(sketch, "E691", {"start": v(-1.06, -0.18) * mm, "end": v(-1.03, -0.14) * mm});
            skLineSegment(sketch, "E692", {"start": v(-1.03, -0.14) * mm, "end": v(-1, -0.1) * mm});
            skLineSegment(sketch, "E693", {"start": v(-1, -0.1) * mm, "end": v(-0.87, 0.03) * mm});
            skLineSegment(sketch, "E694", {"start": v(-0.87, 0.03) * mm, "end": v(-0.73, 0.16) * mm});
            skLineSegment(sketch, "E695", {"start": v(-0.73, 0.16) * mm, "end": v(-0.59, 0.29) * mm});
            skLineSegment(sketch, "E696", {"start": v(-0.59, 0.29) * mm, "end": v(-0.43, 0.4) * mm});
            skLineSegment(sketch, "E697", {"start": v(-0.43, 0.4) * mm, "end": v(-0.27, 0.51) * mm});
            skLineSegment(sketch, "E698", {"start": v(-0.27, 0.51) * mm, "end": v(-0.1, 0.61) * mm});
            skLineSegment(sketch, "E699", {"start": v(-0.1, 0.61) * mm, "end": v(0.06, 0.7) * mm});
            skLineSegment(sketch, "E700", {"start": v(0.06, 0.7) * mm, "end": v(0.23, 0.77) * mm});
            skLineSegment(sketch, "E701", {"start": v(0.23, 0.77) * mm, "end": v(0.3, 0.8) * mm});
            skLineSegment(sketch, "E702", {"start": v(0.3, 0.8) * mm, "end": v(0.38, 0.83) * mm});
            skLineSegment(sketch, "E703", {"start": v(0.38, 0.83) * mm, "end": v(0.46, 0.86) * mm});
            skLineSegment(sketch, "E704", {"start": v(0.46, 0.86) * mm, "end": v(0.53, 0.88) * mm});
            skLineSegment(sketch, "E705", {"start": v(0.53, 0.88) * mm, "end": v(0.6, 0.9) * mm});
            skLineSegment(sketch, "E706", {"start": v(0.6, 0.9) * mm, "end": v(0.65, 0.91) * mm});
            skLineSegment(sketch, "E707", {"start": v(0.65, 0.91) * mm, "end": v(0.7, 0.92) * mm});
            skLineSegment(sketch, "E708", {"start": v(0.7, 0.92) * mm, "end": v(0.7, 0.92) * mm});
            skLineSegment(sketch, "E709", {"start": v(0.7, 0.92) * mm, "end": v(0.71, 0.92) * mm});
            skLineSegment(sketch, "E710", {"start": v(0.71, 0.92) * mm, "end": v(0.73, 0.92) * mm});
            skLineSegment(sketch, "E711", {"start": v(0.73, 0.92) * mm, "end": v(0.76, 0.93) * mm});
            skLineSegment(sketch, "E712", {"start": v(0.76, 0.93) * mm, "end": v(0.79, 0.94) * mm});
            skLineSegment(sketch, "E713", {"start": v(0.79, 0.94) * mm, "end": v(0.87, 0.96) * mm});
            skLineSegment(sketch, "E714", {"start": v(0.87, 0.96) * mm, "end": v(0.97, 0.98) * mm});
            skLineSegment(sketch, "E715", {"start": v(0.97, 0.98) * mm, "end": v(1.08, 1) * mm});
            skLineSegment(sketch, "E716", {"start": v(1.08, 1) * mm, "end": v(1.2, 1.01) * mm});
            skLineSegment(sketch, "E717", {"start": v(1.2, 1.01) * mm, "end": v(1.33, 1.03) * mm});
            skLineSegment(sketch, "E718", {"start": v(1.33, 1.03) * mm, "end": v(1.45, 1.04) * mm});
            skLineSegment(sketch, "E719", {"start": v(1.45, 1.04) * mm, "end": v(1.56, 1.05) * mm});
            skLineSegment(sketch, "E720", {"start": v(1.56, 1.05) * mm, "end": v(1.66, 1.05) * mm});
            skLineSegment(sketch, "E721", {"start": v(1.66, 1.05) * mm, "end": v(1.78, 1.05) * mm});
            skLineSegment(sketch, "E722", {"start": v(1.78, 1.05) * mm, "end": v(1.9, 1.03) * mm});
            skLineSegment(sketch, "E723", {"start": v(1.9, 1.03) * mm, "end": v(2.02, 1.01) * mm});
            skLineSegment(sketch, "E724", {"start": v(2.02, 1.01) * mm, "end": v(2.13, 0.99) * mm});
            skLineSegment(sketch, "E725", {"start": v(2.13, 0.99) * mm, "end": v(2.22, 0.96) * mm});
            skLineSegment(sketch, "E726", {"start": v(2.22, 0.96) * mm, "end": v(2.3, 0.92) * mm});
            skLineSegment(sketch, "E727", {"start": v(2.3, 0.92) * mm, "end": v(2.37, 0.88) * mm});
            skLineSegment(sketch, "E728", {"start": v(2.37, 0.88) * mm, "end": v(2.4, 0.84) * mm});
            skLineSegment(sketch, "E729", {"start": v(2.4, 0.84) * mm, "end": v(2.42, 0.82) * mm});
            skLineSegment(sketch, "E730", {"start": v(2.42, 0.82) * mm, "end": v(2.42, 0.8) * mm});
            skLineSegment(sketch, "E731", {"start": v(2.42, 0.8) * mm, "end": v(2.42, 0.77) * mm});
            skLineSegment(sketch, "E732", {"start": v(2.42, 0.77) * mm, "end": v(2.41, 0.73) * mm});
            skLineSegment(sketch, "E733", {"start": v(2.41, 0.73) * mm, "end": v(2.4, 0.68) * mm});
            skLineSegment(sketch, "E734", {"start": v(2.4, 0.68) * mm, "end": v(2.38, 0.63) * mm});
            skLineSegment(sketch, "E735", {"start": v(2.38, 0.63) * mm, "end": v(2.35, 0.56) * mm});
            skLineSegment(sketch, "E736", {"start": v(2.35, 0.56) * mm, "end": v(2.31, 0.47) * mm});
            skLineSegment(sketch, "E737", {"start": v(2.31, 0.47) * mm, "end": v(2.26, 0.37) * mm});
            skLineSegment(sketch, "E738", {"start": v(2.26, 0.37) * mm, "end": v(2.23, 0.3) * mm});
            skLineSegment(sketch, "E739", {"start": v(2.23, 0.3) * mm, "end": v(2.22, 0.26) * mm});
            skLineSegment(sketch, "E740", {"start": v(2.22, 0.26) * mm, "end": v(2.22, 0.2) * mm});
            skLineSegment(sketch, "E741", {"start": v(2.22, 0.2) * mm, "end": v(2.22, 0.17) * mm});
            skLineSegment(sketch, "E742", {"start": v(2.22, 0.17) * mm, "end": v(2.23, 0.12) * mm});
            skLineSegment(sketch, "E743", {"start": v(2.23, 0.12) * mm, "end": v(2.23, 0.07) * mm});
            skLineSegment(sketch, "E744", {"start": v(2.23, 0.07) * mm, "end": v(2.24, 0.03) * mm});
            skLineSegment(sketch, "E745", {"start": v(2.24, 0.03) * mm, "end": v(2.26, -0.06) * mm});
            skLineSegment(sketch, "E746", {"start": v(2.26, -0.06) * mm, "end": v(2.26, -0.13) * mm});
            skLineSegment(sketch, "E747", {"start": v(2.26, -0.13) * mm, "end": v(2.25, -0.19) * mm});
            skLineSegment(sketch, "E748", {"start": v(2.25, -0.19) * mm, "end": v(2.22, -0.24) * mm});
            skLineSegment(sketch, "E749", {"start": v(2.22, -0.24) * mm, "end": v(2.17, -0.3) * mm});
            skLineSegment(sketch, "E750", {"start": v(2.17, -0.3) * mm, "end": v(2.12, -0.34) * mm});
            skLineSegment(sketch, "E751", {"start": v(2.12, -0.34) * mm, "end": v(2.06, -0.36) * mm});
            skLineSegment(sketch, "E752", {"start": v(2.06, -0.36) * mm, "end": v(1.96, -0.36) * mm});
            skLineSegment(sketch, "E753", {"start": v(1.96, -0.36) * mm, "end": v(1.92, -0.36) * mm});
            skLineSegment(sketch, "E754", {"start": v(1.92, -0.36) * mm, "end": v(1.89, -0.36) * mm});
            skLineSegment(sketch, "E755", {"start": v(1.89, -0.36) * mm, "end": v(1.86, -0.36) * mm});
            skLineSegment(sketch, "E756", {"start": v(1.86, -0.36) * mm, "end": v(1.84, -0.35) * mm});
            skLineSegment(sketch, "E757", {"start": v(1.84, -0.35) * mm, "end": v(1.83, -0.35) * mm});
            skLineSegment(sketch, "E758", {"start": v(1.83, -0.35) * mm, "end": v(1.81, -0.34) * mm});
            skLineSegment(sketch, "E759", {"start": v(1.81, -0.34) * mm, "end": v(1.8, -0.33) * mm});
            skLineSegment(sketch, "E760", {"start": v(1.8, -0.33) * mm, "end": v(1.78, -0.32) * mm});
            skLineSegment(sketch, "E761", {"start": v(1.78, -0.32) * mm, "end": v(1.75, -0.3) * mm});
            skLineSegment(sketch, "E762", {"start": v(1.75, -0.3) * mm, "end": v(1.73, -0.3) * mm});
            skLineSegment(sketch, "E763", {"start": v(1.73, -0.3) * mm, "end": v(1.72, -0.29) * mm});
            skLineSegment(sketch, "E764", {"start": v(1.72, -0.29) * mm, "end": v(1.7, -0.29) * mm});
            skLineSegment(sketch, "E765", {"start": v(1.7, -0.29) * mm, "end": v(1.7, -0.28) * mm});
            skLineSegment(sketch, "E766", {"start": v(1.7, -0.28) * mm, "end": v(1.66, -0.26) * mm});
            skLineSegment(sketch, "E767", {"start": v(1.66, -0.26) * mm, "end": v(1.54, -0.2) * mm});
            skLineSegment(sketch, "E768", {"start": v(1.54, -0.2) * mm, "end": v(1.35, -0.13) * mm});
            skLineSegment(sketch, "E769", {"start": v(1.35, -0.13) * mm, "end": v(1.13, -0.08) * mm});
            skLineSegment(sketch, "E770", {"start": v(1.13, -0.08) * mm, "end": v(0.9, -0.04) * mm});
            skLineSegment(sketch, "E771", {"start": v(0.9, -0.04) * mm, "end": v(0.77, -0.03) * mm});
            skLineSegment(sketch, "E772", {"start": v(0.77, -0.03) * mm, "end": v(0.62, -0.03) * mm});
            skLineSegment(sketch, "E773", {"start": v(0.62, -0.03) * mm, "end": v(0.48, -0.03) * mm});
            skLineSegment(sketch, "E774", {"start": v(0.48, -0.03) * mm, "end": v(0.37, -0.04) * mm});
            skLineSegment(sketch, "E775", {"start": v(0.37, -0.04) * mm, "end": v(0.13, -0.08) * mm});
            skLineSegment(sketch, "E776", {"start": v(0.13, -0.08) * mm, "end": v(-0.1, -0.13) * mm});
            skLineSegment(sketch, "E777", {"start": v(-0.1, -0.13) * mm, "end": v(-0.3, -0.18) * mm});
            skLineSegment(sketch, "E778", {"start": v(-0.3, -0.18) * mm, "end": v(-0.46, -0.24) * mm});
            skLineSegment(sketch, "E779", {"start": v(-0.46, -0.24) * mm, "end": v(-0.59, -0.3) * mm});
            skLineSegment(sketch, "E780", {"start": v(-0.59, -0.3) * mm, "end": v(-0.67, -0.33) * mm});
            skLineSegment(sketch, "E781", {"start": v(-0.67, -0.33) * mm, "end": v(-0.72, -0.36) * mm});
            skLineSegment(sketch, "E782", {"start": v(-0.72, -0.36) * mm, "end": v(-0.73, -0.37) * mm});
            skLineSegment(sketch, "E783", {"start": v(-0.73, -0.37) * mm, "end": v(-0.73, -0.38) * mm});
            skLineSegment(sketch, "E784", {"start": v(-0.73, -0.38) * mm, "end": v(-0.72, -0.38) * mm});
            skLineSegment(sketch, "E785", {"start": v(-0.72, -0.38) * mm, "end": v(-0.7, -0.37) * mm});
            skLineSegment(sketch, "E786", {"start": v(-0.7, -0.37) * mm, "end": v(-0.64, -0.35) * mm});
            skLineSegment(sketch, "E787", {"start": v(-0.64, -0.35) * mm, "end": v(-0.5, -0.3) * mm});
            skLineSegment(sketch, "E788", {"start": v(-0.5, -0.3) * mm, "end": v(-0.4, -0.25) * mm});
            skLineSegment(sketch, "E789", {"start": v(-0.4, -0.25) * mm, "end": v(-0.31, -0.22) * mm});
            skLineSegment(sketch, "E790", {"start": v(-0.31, -0.22) * mm, "end": v(-0.22, -0.2) * mm});
            skLineSegment(sketch, "E791", {"start": v(-0.22, -0.2) * mm, "end": v(0.02, -0.14) * mm});
            skLineSegment(sketch, "E792", {"start": v(0.02, -0.14) * mm, "end": v(0.34, -0.08) * mm});
            skLineSegment(sketch, "E793", {"start": v(0.34, -0.08) * mm, "end": v(0.46, -0.07) * mm});
            skLineSegment(sketch, "E794", {"start": v(0.46, -0.07) * mm, "end": v(0.61, -0.07) * mm});
            skLineSegment(sketch, "E795", {"start": v(0.61, -0.07) * mm, "end": v(0.77, -0.07) * mm});
            skLineSegment(sketch, "E796", {"start": v(0.77, -0.07) * mm, "end": v(0.9, -0.08) * mm});
            skLineSegment(sketch, "E797", {"start": v(0.9, -0.08) * mm, "end": v(1.1, -0.1) * mm});
            skLineSegment(sketch, "E798", {"start": v(1.1, -0.1) * mm, "end": v(1.28, -0.15) * mm});
            skLineSegment(sketch, "E799", {"start": v(1.28, -0.15) * mm, "end": v(1.45, -0.2) * mm});
            skLineSegment(sketch, "E800", {"start": v(1.45, -0.2) * mm, "end": v(1.57, -0.24) * mm});
            skLineSegment(sketch, "E801", {"start": v(1.57, -0.24) * mm, "end": v(1.6, -0.26) * mm});
            skLineSegment(sketch, "E802", {"start": v(1.6, -0.26) * mm, "end": v(1.63, -0.28) * mm});
            skLineSegment(sketch, "E803", {"start": v(1.63, -0.28) * mm, "end": v(1.67, -0.3) * mm});
            skLineSegment(sketch, "E804", {"start": v(1.67, -0.3) * mm, "end": v(1.7, -0.33) * mm});
            skLineSegment(sketch, "E805", {"start": v(1.7, -0.33) * mm, "end": v(1.79, -0.4) * mm});
            skLineSegment(sketch, "E806", {"start": v(1.79, -0.4) * mm, "end": v(1.84, -0.48) * mm});
            skLineSegment(sketch, "E807", {"start": v(1.84, -0.48) * mm, "end": v(1.85, -0.55) * mm});
            skLineSegment(sketch, "E808", {"start": v(1.85, -0.55) * mm, "end": v(1.84, -0.62) * mm});
            skLineSegment(sketch, "E809", {"start": v(1.84, -0.62) * mm, "end": v(1.83, -0.65) * mm});
            skLineSegment(sketch, "E810", {"start": v(1.83, -0.65) * mm, "end": v(1.83, -0.66) * mm});
            skLineSegment(sketch, "E811", {"start": v(1.83, -0.66) * mm, "end": v(1.82, -0.68) * mm});
            skLineSegment(sketch, "E812", {"start": v(1.82, -0.68) * mm, "end": v(1.78, -0.71) * mm});
            skLineSegment(sketch, "E813", {"start": v(1.78, -0.71) * mm, "end": v(1.72, -0.75) * mm});
            skLineSegment(sketch, "E814", {"start": v(1.72, -0.75) * mm, "end": v(1.65, -0.8) * mm});
            skLineSegment(sketch, "E815", {"start": v(1.65, -0.8) * mm, "end": v(1.62, -0.8) * mm});
            skLineSegment(sketch, "E816", {"start": v(1.62, -0.8) * mm, "end": v(1.59, -0.83) * mm});
            skLineSegment(sketch, "E817", {"start": v(1.59, -0.83) * mm, "end": v(1.55, -0.85) * mm});
            skLineSegment(sketch, "E818", {"start": v(1.55, -0.85) * mm, "end": v(1.53, -0.87) * mm});
            skLineSegment(sketch, "E819", {"start": v(1.53, -0.87) * mm, "end": v(1.48, -0.92) * mm});
            skLineSegment(sketch, "E820", {"start": v(1.48, -0.92) * mm, "end": v(1.42, -0.98) * mm});
            skLineSegment(sketch, "E821", {"start": v(1.42, -0.98) * mm, "end": v(1.38, -1.05) * mm});
            skLineSegment(sketch, "E822", {"start": v(1.38, -1.05) * mm, "end": v(1.36, -1.1) * mm});
            skLineSegment(sketch, "E823", {"start": v(1.36, -1.1) * mm, "end": v(1.35, -1.15) * mm});
            skLineSegment(sketch, "E824", {"start": v(1.35, -1.15) * mm, "end": v(1.33, -1.2) * mm});
            skLineSegment(sketch, "E825", {"start": v(1.33, -1.2) * mm, "end": v(1.31, -1.22) * mm});
            skLineSegment(sketch, "E826", {"start": v(1.31, -1.22) * mm, "end": v(1.3, -1.23) * mm});
            skLineSegment(sketch, "E827", {"start": v(1.3, -1.23) * mm, "end": v(1.27, -1.24) * mm});
            skLineSegment(sketch, "E828", {"start": v(1.27, -1.24) * mm, "end": v(1.24, -1.25) * mm});
            skLineSegment(sketch, "E829", {"start": v(1.24, -1.25) * mm, "end": v(1.2, -1.26) * mm});
            skLineSegment(sketch, "E830", {"start": v(1.2, -1.26) * mm, "end": v(1.17, -1.26) * mm});
            skLineSegment(sketch, "E831", {"start": v(1.17, -1.26) * mm, "end": v(1.12, -1.27) * mm});
            skLineSegment(sketch, "E832", {"start": v(1.12, -1.27) * mm, "end": v(1.09, -1.28) * mm});
            skLineSegment(sketch, "E833", {"start": v(1.09, -1.28) * mm, "end": v(1.06, -1.29) * mm});
            skLineSegment(sketch, "E834", {"start": v(1.06, -1.29) * mm, "end": v(1.04, -1.3) * mm});
            skLineSegment(sketch, "E835", {"start": v(1.04, -1.3) * mm, "end": v(1.02, -1.3) * mm});
            skLineSegment(sketch, "E836", {"start": v(1.02, -1.3) * mm, "end": v(1, -1.32) * mm});
            skLineSegment(sketch, "E837", {"start": v(1, -1.32) * mm, "end": v(1, -1.34) * mm});
            skLineSegment(sketch, "E838", {"start": v(1, -1.34) * mm, "end": v(0.98, -1.37) * mm});
            skLineSegment(sketch, "E839", {"start": v(0.98, -1.37) * mm, "end": v(0.96, -1.4) * mm});
            skLineSegment(sketch, "E840", {"start": v(0.96, -1.4) * mm, "end": v(0.94, -1.42) * mm});
            skLineSegment(sketch, "E841", {"start": v(0.94, -1.42) * mm, "end": v(0.92, -1.44) * mm});
            skLineSegment(sketch, "E842", {"start": v(0.92, -1.44) * mm, "end": v(0.9, -1.46) * mm});
            skLineSegment(sketch, "E843", {"start": v(0.9, -1.46) * mm, "end": v(0.83, -1.48) * mm});
            skLineSegment(sketch, "E844", {"start": v(0.83, -1.48) * mm, "end": v(0.77, -1.5) * mm});
            skLineSegment(sketch, "E845", {"start": v(0.77, -1.5) * mm, "end": v(0.72, -1.5) * mm});
            skLineSegment(sketch, "E846", {"start": v(0.72, -1.5) * mm, "end": v(0.68, -1.5) * mm});
            skLineSegment(sketch, "E847", {"start": v(0.68, -1.5) * mm, "end": v(0.66, -1.5) * mm});
            skLineSegment(sketch, "E848", {"start": v(0.66, -1.5) * mm, "end": v(0.64, -1.5) * mm});
            skLineSegment(sketch, "E849", {"start": v(0.64, -1.5) * mm, "end": v(0.62, -1.5) * mm});
            skLineSegment(sketch, "E850", {"start": v(0.62, -1.5) * mm, "end": v(0.61, -1.48) * mm});
            skLineSegment(sketch, "E851", {"start": v(0.61, -1.48) * mm, "end": v(0.6, -1.48) * mm});
            skLineSegment(sketch, "E852", {"start": v(0.6, -1.48) * mm, "end": v(0.6, -1.46) * mm});
            skLineSegment(sketch, "E853", {"start": v(0.6, -1.46) * mm, "end": v(0.57, -1.45) * mm});
            skLineSegment(sketch, "E854", {"start": v(0.57, -1.45) * mm, "end": v(0.55, -1.43) * mm});
            skLineSegment(sketch, "E855", {"start": v(0.55, -1.43) * mm, "end": v(0.44, -1.33) * mm});
            skLineSegment(sketch, "E856", {"start": v(0.44, -1.33) * mm, "end": v(0.32, -1.17) * mm});
            skLineSegment(sketch, "E857", {"start": v(0.32, -1.17) * mm, "end": v(0.23, -1.07) * mm});
            skLineSegment(sketch, "E858", {"start": v(0.23, -1.07) * mm, "end": v(0.13, -0.96) * mm});
            skLineSegment(sketch, "E859", {"start": v(0.13, -0.96) * mm, "end": v(0.02, -0.87) * mm});
            skLineSegment(sketch, "E860", {"start": v(0.02, -0.87) * mm, "end": v(-0.06, -0.82) * mm});
            skLineSegment(sketch, "E861", {"start": v(-0.06, -0.82) * mm, "end": v(-0.16, -0.78) * mm});
            skLineSegment(sketch, "E862", {"start": v(-0.16, -0.78) * mm, "end": v(-0.24, -0.75) * mm});
            skLineSegment(sketch, "E863", {"start": v(-0.24, -0.75) * mm, "end": v(-0.32, -0.75) * mm});
            skLineSegment(sketch, "E864", {"start": v(-0.32, -0.75) * mm, "end": v(-0.43, -0.75) * mm});
            skLineSegment(sketch, "E865", {"start": v(-0.43, -0.75) * mm, "end": v(-0.48, -0.76) * mm});
            skLineSegment(sketch, "E866", {"start": v(-0.48, -0.76) * mm, "end": v(-0.52, -0.76) * mm});
            skLineSegment(sketch, "E867", {"start": v(-0.52, -0.76) * mm, "end": v(-0.55, -0.77) * mm});
            skLineSegment(sketch, "E868", {"start": v(-0.55, -0.77) * mm, "end": v(-0.57, -0.77) * mm});
            skLineSegment(sketch, "E869", {"start": v(-0.57, -0.77) * mm, "end": v(-0.56, -0.79) * mm});
            skLineSegment(sketch, "E870", {"start": v(-0.56, -0.79) * mm, "end": v(-0.53, -0.81) * mm});
            skLineSegment(sketch, "E871", {"start": v(-0.53, -0.81) * mm, "end": v(-0.5, -0.83) * mm});
            skLineSegment(sketch, "E872", {"start": v(-0.5, -0.83) * mm, "end": v(-0.5, -0.85) * mm});
            skLineSegment(sketch, "E873", {"start": v(-0.5, -0.85) * mm, "end": v(-0.5, -0.86) * mm});
            skLineSegment(sketch, "E874", {"start": v(-0.5, -0.86) * mm, "end": v(-0.5, -0.87) * mm});
            skLineSegment(sketch, "E875", {"start": v(-0.5, -0.87) * mm, "end": v(-0.52, -0.88) * mm});
            skLineSegment(sketch, "E876", {"start": v(-0.52, -0.88) * mm, "end": v(-0.55, -0.89) * mm});
            skLineSegment(sketch, "E877", {"start": v(-0.55, -0.89) * mm, "end": v(-0.6, -0.9) * mm});
            skLineSegment(sketch, "E878", {"start": v(-0.6, -0.9) * mm, "end": v(-0.7, -0.93) * mm});
            skLineSegment(sketch, "E879", {"start": v(-0.7, -0.93) * mm, "end": v(-0.8, -0.97) * mm});
            skLineSegment(sketch, "E880", {"start": v(-0.8, -0.97) * mm, "end": v(-0.93, -1.03) * mm});
            skLineSegment(sketch, "E881", {"start": v(-0.93, -1.03) * mm, "end": v(-1, -1.07) * mm});
            skLineSegment(sketch, "E882", {"start": v(-1, -1.07) * mm, "end": v(-1.05, -1.1) * mm});
            skLineSegment(sketch, "E883", {"start": v(-1.05, -1.1) * mm, "end": v(-1.1, -1.13) * mm});
            skLineSegment(sketch, "E884", {"start": v(-1.1, -1.13) * mm, "end": v(-1.12, -1.14) * mm});
            skLineSegment(sketch, "E885", {"start": v(-1.12, -1.14) * mm, "end": v(-1.22, -1.2) * mm});
            skLineSegment(sketch, "E886", {"start": v(-1.22, -1.2) * mm, "end": v(-1.34, -1.26) * mm});
            skLineSegment(sketch, "E887", {"start": v(-1.34, -1.26) * mm, "end": v(-1.47, -1.31) * mm});
            skLineSegment(sketch, "E888", {"start": v(-1.47, -1.31) * mm, "end": v(-1.57, -1.35) * mm});
            skLineSegment(sketch, "E889", {"start": v(-1.57, -1.35) * mm, "end": v(-1.66, -1.37) * mm});
            skLineSegment(sketch, "E890", {"start": v(-1.66, -1.37) * mm, "end": v(-1.76, -1.38) * mm});
            skLineSegment(sketch, "E891", {"start": v(-1.76, -1.38) * mm, "end": v(-1.85, -1.38) * mm});
            skLineSegment(sketch, "E892", {"start": v(-1.85, -1.38) * mm, "end": v(-1.92, -1.37) * mm});
            skLineSegment(sketch, "E893", {"start": v(-1.92, -1.37) * mm, "end": v(-1.98, -1.35) * mm});
            skLineSegment(sketch, "E894", {"start": v(-1.98, -1.35) * mm, "end": v(-2, -1.39) * mm});
            skLineSegment(sketch, "E895", {"start": v(-2, -1.39) * mm, "end": v(-2.04, -1.41) * mm});
            skLineSegment(sketch, "E896", {"start": v(-2.04, -1.41) * mm, "end": v(-2.07, -1.43) * mm});
            skLineSegment(sketch, "E897", {"start": v(-2.07, -1.43) * mm, "end": v(-2.1, -1.45) * mm});
            skLineSegment(sketch, "E898", {"start": v(-2.1, -1.45) * mm, "end": v(-2.13, -1.45) * mm});
            skLineSegment(sketch, "E899", {"start": v(-2.13, -1.45) * mm, "end": v(-2.14, -1.46) * mm});
            skLineSegment(sketch, "E900", {"start": v(-2.14, -1.46) * mm, "end": v(-2.15, -1.47) * mm});
            skLineSegment(sketch, "E901", {"start": v(-2.15, -1.47) * mm, "end": v(-2.17, -1.5) * mm});
            skLineSegment(sketch, "E902", {"start": v(-2.17, -1.5) * mm, "end": v(-2.19, -1.53) * mm});
            skLineSegment(sketch, "E903", {"start": v(-2.19, -1.53) * mm, "end": v(-2.21, -1.59) * mm});
            skLineSegment(sketch, "E904", {"start": v(-2.21, -1.59) * mm, "end": v(-2.24, -1.66) * mm});
            skLineSegment(sketch, "E905", {"start": v(-2.24, -1.66) * mm, "end": v(-2.27, -1.76) * mm});
            skLineSegment(sketch, "E906", {"start": v(-2.27, -1.76) * mm, "end": v(-2.31, -1.88) * mm});
            skLineSegment(sketch, "E907", {"start": v(-2.31, -1.88) * mm, "end": v(-2.4, -2.15) * mm});
            skLineSegment(sketch, "E908", {"start": v(-2.4, -2.15) * mm, "end": v(-2.46, -2.39) * mm});
            skLineSegment(sketch, "E909", {"start": v(-2.46, -2.39) * mm, "end": v(-2.5, -2.6) * mm});
            skLineSegment(sketch, "E910", {"start": v(-2.5, -2.6) * mm, "end": v(-2.52, -2.79) * mm});
            skLineSegment(sketch, "E911", {"start": v(-2.52, -2.79) * mm, "end": v(-2.53, -2.9) * mm});
            skLineSegment(sketch, "E912", {"start": v(-2.53, -2.9) * mm, "end": v(-2.53, -3.02) * mm});
            skLineSegment(sketch, "E913", {"start": v(-2.53, -3.02) * mm, "end": v(-2.54, -3.16) * mm});
            skLineSegment(sketch, "E914", {"start": v(-2.54, -3.16) * mm, "end": v(-2.54, -3.3) * mm});
            skLineSegment(sketch, "E915", {"start": v(-2.54, -3.3) * mm, "end": v(-2.54, -3.44) * mm});
            skLineSegment(sketch, "E916", {"start": v(-2.54, -3.44) * mm, "end": v(-2.54, -3.56) * mm});
            skLineSegment(sketch, "E917", {"start": v(-2.54, -3.56) * mm, "end": v(-2.54, -3.65) * mm});
            skLineSegment(sketch, "E918", {"start": v(-2.54, -3.65) * mm, "end": v(-2.53, -3.7) * mm});
            skLineSegment(sketch, "E919", {"start": v(-2.53, -3.7) * mm, "end": v(-2.52, -3.78) * mm});
            skLineSegment(sketch, "E920", {"start": v(-2.52, -3.78) * mm, "end": v(-2.51, -3.86) * mm});
            skLineSegment(sketch, "E921", {"start": v(-2.51, -3.86) * mm, "end": v(-2.5, -3.92) * mm});
            skLineSegment(sketch, "E922", {"start": v(-2.5, -3.92) * mm, "end": v(-2.49, -4) * mm});
            skLineSegment(sketch, "E923", {"start": v(-2.49, -4) * mm, "end": v(-2.47, -4.06) * mm});
            skLineSegment(sketch, "E924", {"start": v(-2.47, -4.06) * mm, "end": v(-2.46, -4.12) * mm});
            skLineSegment(sketch, "E925", {"start": v(-2.46, -4.12) * mm, "end": v(-2.46, -4.13) * mm});
            skLineSegment(sketch, "E926", {"start": v(-2.46, -4.13) * mm, "end": v(-2.45, -4.13) * mm});
            skLineSegment(sketch, "E927", {"start": v(-2.45, -4.13) * mm, "end": v(-2.45, -4.1) * mm});
            skLineSegment(sketch, "E928", {"start": v(-2.45, -4.1) * mm, "end": v(-2.46, -4.06) * mm});
            skLineSegment(sketch, "E929", {"start": v(-2.46, -4.06) * mm, "end": v(-2.46, -4) * mm});
            skLineSegment(sketch, "E930", {"start": v(-2.46, -4) * mm, "end": v(-2.47, -3.9) * mm});
            skLineSegment(sketch, "E931", {"start": v(-2.47, -3.9) * mm, "end": v(-2.47, -3.77) * mm});
            skLineSegment(sketch, "E932", {"start": v(-2.47, -3.77) * mm, "end": v(-2.47, -3.6) * mm});
            skLineSegment(sketch, "E933", {"start": v(-2.47, -3.6) * mm, "end": v(-2.47, -3.38) * mm});
            skLineSegment(sketch, "E934", {"start": v(-2.47, -3.38) * mm, "end": v(-2.47, -3.25) * mm});
            skLineSegment(sketch, "E935", {"start": v(-2.47, -3.25) * mm, "end": v(-2.46, -3.16) * mm});
            skLineSegment(sketch, "E936", {"start": v(-2.46, -3.16) * mm, "end": v(-2.45, -3.1) * mm});
            skLineSegment(sketch, "E937", {"start": v(-2.45, -3.1) * mm, "end": v(-2.41, -2.92) * mm});
            skLineSegment(sketch, "E938", {"start": v(-2.41, -2.92) * mm, "end": v(-2.35, -2.76) * mm});
            skLineSegment(sketch, "E939", {"start": v(-2.35, -2.76) * mm, "end": v(-2.29, -2.62) * mm});
            skLineSegment(sketch, "E940", {"start": v(-2.29, -2.62) * mm, "end": v(-2.21, -2.52) * mm});
            skLineSegment(sketch, "E941", {"start": v(-2.21, -2.52) * mm, "end": v(-2.18, -2.49) * mm});
            skLineSegment(sketch, "E942", {"start": v(-2.18, -2.49) * mm, "end": v(-2.16, -2.47) * mm});
            skLineSegment(sketch, "E943", {"start": v(-2.16, -2.47) * mm, "end": v(-2.15, -2.47) * mm});
            skLineSegment(sketch, "E944", {"start": v(-2.15, -2.47) * mm, "end": v(-2.14, -2.48) * mm});
            skLineSegment(sketch, "E945", {"start": v(-2.14, -2.48) * mm, "end": v(-2.13, -2.49) * mm});
            skLineSegment(sketch, "E946", {"start": v(-2.13, -2.49) * mm, "end": v(-2.13, -2.5) * mm});
            skLineSegment(sketch, "E947", {"start": v(-2.13, -2.5) * mm, "end": v(-2.13, -2.53) * mm});
            skLineSegment(sketch, "E948", {"start": v(-2.13, -2.53) * mm, "end": v(-2.15, -2.57) * mm});
            skLineSegment(sketch, "E949", {"start": v(-2.15, -2.57) * mm, "end": v(-2.16, -2.6) * mm});
            skLineSegment(sketch, "E950", {"start": v(-2.16, -2.6) * mm, "end": v(-2.17, -2.63) * mm});
            skLineSegment(sketch, "E951", {"start": v(-2.17, -2.63) * mm, "end": v(-2.18, -2.67) * mm});
            skLineSegment(sketch, "E952", {"start": v(-2.18, -2.67) * mm, "end": v(-2.18, -2.7) * mm});
            skLineSegment(sketch, "E953", {"start": v(-2.18, -2.7) * mm, "end": v(-2.2, -2.8) * mm});
            skLineSegment(sketch, "E954", {"start": v(-2.2, -2.8) * mm, "end": v(-2.23, -2.9) * mm});
            skLineSegment(sketch, "E955", {"start": v(-2.23, -2.9) * mm, "end": v(-2.26, -3.04) * mm});
            skLineSegment(sketch, "E956", {"start": v(-2.26, -3.04) * mm, "end": v(-2.3, -3.17) * mm});
            skLineSegment(sketch, "E957", {"start": v(-2.3, -3.17) * mm, "end": v(-2.34, -3.3) * mm});
            skLineSegment(sketch, "E958", {"start": v(-2.34, -3.3) * mm, "end": v(-2.36, -3.4) * mm});
            skLineSegment(sketch, "E959", {"start": v(-2.36, -3.4) * mm, "end": v(-2.38, -3.5) * mm});
            skLineSegment(sketch, "E960", {"start": v(-2.38, -3.5) * mm, "end": v(-2.39, -3.62) * mm});
            skLineSegment(sketch, "E961", {"start": v(-2.39, -3.62) * mm, "end": v(-2.4, -3.69) * mm});
            skLineSegment(sketch, "E962", {"start": v(-2.4, -3.69) * mm, "end": v(-2.4, -3.78) * mm});
            skLineSegment(sketch, "E963", {"start": v(-2.4, -3.78) * mm, "end": v(-2.4, -3.9) * mm});
            skLineSegment(sketch, "E964", {"start": v(-2.4, -3.9) * mm, "end": v(-2.4, -4) * mm});
            skLineSegment(sketch, "E965", {"start": v(-2.4, -4) * mm, "end": v(-2.39, -4.11) * mm});
            skLineSegment(sketch, "E966", {"start": v(-2.39, -4.11) * mm, "end": v(-2.38, -4.2) * mm});
            skLineSegment(sketch, "E967", {"start": v(-2.38, -4.2) * mm, "end": v(-2.38, -4.27) * mm});
            skLineSegment(sketch, "E968", {"start": v(-2.38, -4.27) * mm, "end": v(-2.37, -4.3) * mm});
            skLineSegment(sketch, "E969", {"start": v(-2.37, -4.3) * mm, "end": v(-2.36, -4.31) * mm});
            skLineSegment(sketch, "E970", {"start": v(-2.36, -4.31) * mm, "end": v(-2.36, -4.3) * mm});
            skLineSegment(sketch, "E971", {"start": v(-2.36, -4.3) * mm, "end": v(-2.35, -4.27) * mm});
            skLineSegment(sketch, "E972", {"start": v(-2.35, -4.27) * mm, "end": v(-2.34, -4.2) * mm});
            skLineSegment(sketch, "E973", {"start": v(-2.34, -4.2) * mm, "end": v(-2.31, -4.08) * mm});
            skLineSegment(sketch, "E974", {"start": v(-2.31, -4.08) * mm, "end": v(-2.3, -3.98) * mm});
            skLineSegment(sketch, "E975", {"start": v(-2.3, -3.98) * mm, "end": v(-2.29, -3.93) * mm});
            skLineSegment(sketch, "E976", {"start": v(-2.29, -3.93) * mm, "end": v(-2.28, -3.88) * mm});
            skLineSegment(sketch, "E977", {"start": v(-2.28, -3.88) * mm, "end": v(-2.27, -3.83) * mm});
            skLineSegment(sketch, "E978", {"start": v(-2.27, -3.83) * mm, "end": v(-2.26, -3.78) * mm});
            skLineSegment(sketch, "E979", {"start": v(-2.26, -3.78) * mm, "end": v(-2.24, -3.68) * mm});
            skLineSegment(sketch, "E980", {"start": v(-2.24, -3.68) * mm, "end": v(-2.21, -3.56) * mm});
            skLineSegment(sketch, "E981", {"start": v(-2.21, -3.56) * mm, "end": v(-2.18, -3.44) * mm});
            skLineSegment(sketch, "E982", {"start": v(-2.18, -3.44) * mm, "end": v(-2.15, -3.33) * mm});
            skLineSegment(sketch, "E983", {"start": v(-2.15, -3.33) * mm, "end": v(-2.13, -3.28) * mm});
            skLineSegment(sketch, "E984", {"start": v(-2.13, -3.28) * mm, "end": v(-2.12, -3.24) * mm});
            skLineSegment(sketch, "E985", {"start": v(-2.12, -3.24) * mm, "end": v(-2.1, -3.2) * mm});
            skLineSegment(sketch, "E986", {"start": v(-2.1, -3.2) * mm, "end": v(-2.1, -3.18) * mm});
            skLineSegment(sketch, "E987", {"start": v(-2.1, -3.18) * mm, "end": v(-2.08, -3.13) * mm});
            skLineSegment(sketch, "E988", {"start": v(-2.08, -3.13) * mm, "end": v(-2.06, -3.09) * mm});
            skLineSegment(sketch, "E989", {"start": v(-2.06, -3.09) * mm, "end": v(-2.05, -3.06) * mm});
            skLineSegment(sketch, "E990", {"start": v(-2.05, -3.06) * mm, "end": v(-2.04, -3.04) * mm});
            skLineSegment(sketch, "E991", {"start": v(-2.04, -3.04) * mm, "end": v(-2.04, -3.01) * mm});
            skLineSegment(sketch, "E992", {"start": v(-2.04, -3.01) * mm, "end": v(-2.04, -2.97) * mm});
            skLineSegment(sketch, "E993", {"start": v(-2.04, -2.97) * mm, "end": v(-2.04, -2.92) * mm});
            skLineSegment(sketch, "E994", {"start": v(-2.04, -2.92) * mm, "end": v(-2.04, -2.9) * mm});
            skLineSegment(sketch, "E995", {"start": v(-2.04, -2.9) * mm, "end": v(-2.03, -2.87) * mm});
            skLineSegment(sketch, "E996", {"start": v(-2.03, -2.87) * mm, "end": v(-2.02, -2.85) * mm});
            skLineSegment(sketch, "E997", {"start": v(-2.02, -2.85) * mm, "end": v(-2, -2.82) * mm});
            skLineSegment(sketch, "E998", {"start": v(-2, -2.82) * mm, "end": v(-2, -2.8) * mm});
            skLineSegment(sketch, "E999", {"start": v(-2, -2.8) * mm, "end": v(-2, -2.78) * mm});
            skLineSegment(sketch, "E1000", {"start": v(-2, -2.78) * mm, "end": v(-2, -2.75) * mm});
            skLineSegment(sketch, "E1001", {"start": v(-2, -2.75) * mm, "end": v(-2, -2.72) * mm});
            skLineSegment(sketch, "E1002", {"start": v(-2, -2.72) * mm, "end": v(-2.01, -2.69) * mm});
            skLineSegment(sketch, "E1003", {"start": v(-2.01, -2.69) * mm, "end": v(-2, -2.65) * mm});
            skLineSegment(sketch, "E1004", {"start": v(-2, -2.65) * mm, "end": v(-2, -2.6) * mm});
            skLineSegment(sketch, "E1005", {"start": v(-2, -2.6) * mm, "end": v(-1.98, -2.54) * mm});
            skLineSegment(sketch, "E1006", {"start": v(-1.98, -2.54) * mm, "end": v(-1.96, -2.47) * mm});
            skLineSegment(sketch, "E1007", {"start": v(-1.96, -2.47) * mm, "end": v(-1.93, -2.4) * mm});
            skLineSegment(sketch, "E1008", {"start": v(-1.93, -2.4) * mm, "end": v(-1.9, -2.32) * mm});
            skLineSegment(sketch, "E1009", {"start": v(-1.9, -2.32) * mm, "end": v(-1.85, -2.19) * mm});
            skLineSegment(sketch, "E1010", {"start": v(-1.85, -2.19) * mm, "end": v(-1.83, -2.08) * mm});
            skLineSegment(sketch, "E1011", {"start": v(-1.83, -2.08) * mm, "end": v(-1.81, -1.98) * mm});
            skLineSegment(sketch, "E1012", {"start": v(-1.81, -1.98) * mm, "end": v(-1.82, -1.87) * mm});
            skLineSegment(sketch, "E1013", {"start": v(-1.82, -1.87) * mm, "end": v(-1.82, -1.82) * mm});
            skLineSegment(sketch, "E1014", {"start": v(-1.82, -1.82) * mm, "end": v(-1.82, -1.79) * mm});
            skLineSegment(sketch, "E1015", {"start": v(-1.82, -1.79) * mm, "end": v(-1.81, -1.77) * mm});
            skLineSegment(sketch, "E1016", {"start": v(-1.81, -1.77) * mm, "end": v(-1.8, -1.77) * mm});
            skLineSegment(sketch, "E1017", {"start": v(-1.8, -1.77) * mm, "end": v(-1.79, -1.77) * mm});
            skLineSegment(sketch, "E1018", {"start": v(-1.79, -1.77) * mm, "end": v(-1.77, -1.78) * mm});
            skLineSegment(sketch, "E1019", {"start": v(-1.77, -1.78) * mm, "end": v(-1.76, -1.8) * mm});
            skLineSegment(sketch, "E1020", {"start": v(-1.76, -1.8) * mm, "end": v(-1.73, -1.85) * mm});
            skLineSegment(sketch, "E1021", {"start": v(-1.73, -1.85) * mm, "end": v(-1.7, -1.9) * mm});
            skLineSegment(sketch, "E1022", {"start": v(-1.7, -1.9) * mm, "end": v(-1.66, -1.82) * mm});
            skLineSegment(sketch, "E1023", {"start": v(-1.66, -1.82) * mm, "end": v(-1.63, -1.77) * mm});
            skLineSegment(sketch, "E1024", {"start": v(-1.63, -1.77) * mm, "end": v(-1.6, -1.73) * mm});
            skLineSegment(sketch, "E1025", {"start": v(-1.6, -1.73) * mm, "end": v(-1.55, -1.68) * mm});
            skLineSegment(sketch, "E1026", {"start": v(-1.55, -1.68) * mm, "end": v(-1.48, -1.6) * mm});
            skLineSegment(sketch, "E1027", {"start": v(-1.48, -1.6) * mm, "end": v(-1.42, -1.55) * mm});
            skLineSegment(sketch, "E1028", {"start": v(-1.42, -1.55) * mm, "end": v(-1.36, -1.5) * mm});
            skLineSegment(sketch, "E1029", {"start": v(-1.36, -1.5) * mm, "end": v(-1.32, -1.47) * mm});
            skLineSegment(sketch, "E1030", {"start": v(-1.32, -1.47) * mm, "end": v(-1.27, -1.44) * mm});
            skLineSegment(sketch, "E1031", {"start": v(-1.27, -1.44) * mm, "end": v(-1.12, -1.38) * mm});
            skLineSegment(sketch, "E1032", {"start": v(-1.12, -1.38) * mm, "end": v(-0.99, -1.35) * mm});
            skLineSegment(sketch, "E1033", {"start": v(-0.99, -1.35) * mm, "end": v(-0.92, -1.34) * mm});
            skLineSegment(sketch, "E1034", {"start": v(-0.92, -1.34) * mm, "end": v(-1.01, -1.43) * mm});
            skLineSegment(sketch, "E1035", {"start": v(-1.01, -1.43) * mm, "end": v(-1.05, -1.47) * mm});
            skLineSegment(sketch, "E1036", {"start": v(-1.05, -1.47) * mm, "end": v(-1.1, -1.52) * mm});
            skLineSegment(sketch, "E1037", {"start": v(-1.1, -1.52) * mm, "end": v(-1.14, -1.57) * mm});
            skLineSegment(sketch, "E1038", {"start": v(-1.14, -1.57) * mm, "end": v(-1.17, -1.6) * mm});
            skLineSegment(sketch, "E1039", {"start": v(-1.17, -1.6) * mm, "end": v(-1.2, -1.64) * mm});
            skLineSegment(sketch, "E1040", {"start": v(-1.2, -1.64) * mm, "end": v(-1.23, -1.67) * mm});
            skLineSegment(sketch, "E1041", {"start": v(-1.23, -1.67) * mm, "end": v(-1.24, -1.7) * mm});
            skLineSegment(sketch, "E1042", {"start": v(-1.24, -1.7) * mm, "end": v(-1.26, -1.7) * mm});
            skLineSegment(sketch, "E1043", {"start": v(-1.26, -1.7) * mm, "end": v(-1.27, -1.72) * mm});
            skLineSegment(sketch, "E1044", {"start": v(-1.27, -1.72) * mm, "end": v(-1.28, -1.74) * mm});
            skLineSegment(sketch, "E1045", {"start": v(-1.28, -1.74) * mm, "end": v(-1.3, -1.77) * mm});
            skLineSegment(sketch, "E1046", {"start": v(-1.3, -1.77) * mm, "end": v(-1.33, -1.8) * mm});
            skLineSegment(sketch, "E1047", {"start": v(-1.33, -1.8) * mm, "end": v(-1.35, -1.84) * mm});
            skLineSegment(sketch, "E1048", {"start": v(-1.35, -1.84) * mm, "end": v(-1.38, -1.87) * mm});
            skLineSegment(sketch, "E1049", {"start": v(-1.38, -1.87) * mm, "end": v(-1.4, -1.9) * mm});
            skLineSegment(sketch, "E1050", {"start": v(-1.4, -1.9) * mm, "end": v(-1.42, -1.93) * mm});
            skLineSegment(sketch, "E1051", {"start": v(-1.42, -1.93) * mm, "end": v(-1.43, -1.95) * mm});
            skLineSegment(sketch, "E1052", {"start": v(-1.43, -1.95) * mm, "end": v(-1.45, -1.97) * mm});
            skLineSegment(sketch, "E1053", {"start": v(-1.45, -1.97) * mm, "end": v(-1.45, -1.98) * mm});
            skLineSegment(sketch, "E1054", {"start": v(-1.45, -1.98) * mm, "end": v(-1.46, -2) * mm});
            skLineSegment(sketch, "E1055", {"start": v(-1.46, -2) * mm, "end": v(-1.45, -2) * mm});
            skLineSegment(sketch, "E1056", {"start": v(-1.45, -2) * mm, "end": v(-1.45, -1.99) * mm});
            skLineSegment(sketch, "E1057", {"start": v(-1.45, -1.99) * mm, "end": v(-1.44, -1.98) * mm});
            skLineSegment(sketch, "E1058", {"start": v(-1.44, -1.98) * mm, "end": v(-1.42, -1.96) * mm});
            skLineSegment(sketch, "E1059", {"start": v(-1.42, -1.96) * mm, "end": v(-1.4, -1.93) * mm});
            skLineSegment(sketch, "E1060", {"start": v(-1.4, -1.93) * mm, "end": v(-1.37, -1.9) * mm});
            skLineSegment(sketch, "E1061", {"start": v(-1.37, -1.9) * mm, "end": v(-1.33, -1.85) * mm});
            skLineSegment(sketch, "E1062", {"start": v(-1.33, -1.85) * mm, "end": v(-1.3, -1.8) * mm});
            skLineSegment(sketch, "E1063", {"start": v(-1.3, -1.8) * mm, "end": v(-1.2, -1.7) * mm});
            skLineSegment(sketch, "E1064", {"start": v(-1.2, -1.7) * mm, "end": v(-1.13, -1.6) * mm});
            skLineSegment(sketch, "E1065", {"start": v(-1.13, -1.6) * mm, "end": v(-1.06, -1.52) * mm});
            skLineSegment(sketch, "E1066", {"start": v(-1.06, -1.52) * mm, "end": v(-1, -1.46) * mm});
            skLineSegment(sketch, "E1067", {"start": v(-1, -1.46) * mm, "end": v(-0.96, -1.41) * mm});
            skLineSegment(sketch, "E1068", {"start": v(-0.96, -1.41) * mm, "end": v(-0.91, -1.37) * mm});
            skLineSegment(sketch, "E1069", {"start": v(-0.91, -1.37) * mm, "end": v(-0.87, -1.34) * mm});
            skLineSegment(sketch, "E1070", {"start": v(-0.87, -1.34) * mm, "end": v(-0.83, -1.32) * mm});
            skLineSegment(sketch, "E1071", {"start": v(-0.83, -1.32) * mm, "end": v(-0.79, -1.3) * mm});
            skLineSegment(sketch, "E1072", {"start": v(-0.79, -1.3) * mm, "end": v(-0.76, -1.3) * mm});
            skLineSegment(sketch, "E1073", {"start": v(-0.76, -1.3) * mm, "end": v(-0.73, -1.29) * mm});
            skLineSegment(sketch, "E1074", {"start": v(-0.73, -1.29) * mm, "end": v(-0.7, -1.3) * mm});
            skLineSegment(sketch, "E1075", {"start": v(-0.7, -1.3) * mm, "end": v(-0.63, -1.3) * mm});
            skLineSegment(sketch, "E1076", {"start": v(-0.63, -1.3) * mm, "end": v(-0.59, -1.28) * mm});
            skLineSegment(sketch, "E1077", {"start": v(-0.59, -1.28) * mm, "end": v(-0.56, -1.27) * mm});
            skLineSegment(sketch, "E1078", {"start": v(-0.56, -1.27) * mm, "end": v(-0.52, -1.27) * mm});
            skLineSegment(sketch, "E1079", {"start": v(-0.52, -1.27) * mm, "end": v(-0.5, -1.27) * mm});
            skLineSegment(sketch, "E1080", {"start": v(-0.5, -1.27) * mm, "end": v(-0.46, -1.28) * mm});
            skLineSegment(sketch, "E1081", {"start": v(-0.46, -1.28) * mm, "end": v(-0.43, -1.3) * mm});
            skLineSegment(sketch, "E1082", {"start": v(-0.43, -1.3) * mm, "end": v(-0.4, -1.31) * mm});
            skLineSegment(sketch, "E1083", {"start": v(-0.4, -1.31) * mm, "end": v(-0.4, -1.33) * mm});
            skLineSegment(sketch, "E1084", {"start": v(-0.4, -1.33) * mm, "end": v(-0.39, -1.35) * mm});
            skLineSegment(sketch, "E1085", {"start": v(-0.39, -1.35) * mm, "end": v(-0.41, -1.4) * mm});
            skLineSegment(sketch, "E1086", {"start": v(-0.41, -1.4) * mm, "end": v(-0.47, -1.43) * mm});
            skLineSegment(sketch, "E1087", {"start": v(-0.47, -1.43) * mm, "end": v(-0.5, -1.45) * mm});
            skLineSegment(sketch, "E1088", {"start": v(-0.5, -1.45) * mm, "end": v(-0.54, -1.47) * mm});
            skLineSegment(sketch, "E1089", {"start": v(-0.54, -1.47) * mm, "end": v(-0.59, -1.5) * mm});
            skLineSegment(sketch, "E1090", {"start": v(-0.59, -1.5) * mm, "end": v(-0.65, -1.54) * mm});
            skLineSegment(sketch, "E1091", {"start": v(-0.65, -1.54) * mm, "end": v(-0.71, -1.6) * mm});
            skLineSegment(sketch, "E1092", {"start": v(-0.71, -1.6) * mm, "end": v(-0.8, -1.66) * mm});
            skLineSegment(sketch, "E1093", {"start": v(-0.8, -1.66) * mm, "end": v(-0.89, -1.73) * mm});
            skLineSegment(sketch, "E1094", {"start": v(-0.89, -1.73) * mm, "end": v(-1, -1.82) * mm});
            skLineSegment(sketch, "E1095", {"start": v(-1, -1.82) * mm, "end": v(-1.04, -1.86) * mm});
            skLineSegment(sketch, "E1096", {"start": v(-1.04, -1.86) * mm, "end": v(-1.1, -1.9) * mm});
            skLineSegment(sketch, "E1097", {"start": v(-1.1, -1.9) * mm, "end": v(-1.14, -1.94) * mm});
            skLineSegment(sketch, "E1098", {"start": v(-1.14, -1.94) * mm, "end": v(-1.17, -1.96) * mm});
            skLineSegment(sketch, "E1099", {"start": v(-1.17, -1.96) * mm, "end": v(-1.2, -1.98) * mm});
            skLineSegment(sketch, "E1100", {"start": v(-1.2, -1.98) * mm, "end": v(-1.2, -1.99) * mm});
            skLineSegment(sketch, "E1101", {"start": v(-1.2, -1.99) * mm, "end": v(-1.2, -2) * mm});
            skLineSegment(sketch, "E1102", {"start": v(-1.2, -2) * mm, "end": v(-1.2, -2) * mm});
            skLineSegment(sketch, "E1103", {"start": v(-1.2, -2) * mm, "end": v(-1.17, -1.98) * mm});
            skLineSegment(sketch, "E1104", {"start": v(-1.17, -1.98) * mm, "end": v(-1.12, -1.94) * mm});
            skLineSegment(sketch, "E1105", {"start": v(-1.12, -1.94) * mm, "end": v(-1.06, -1.9) * mm});
            skLineSegment(sketch, "E1106", {"start": v(-1.06, -1.9) * mm, "end": v(-0.98, -1.84) * mm});
            skLineSegment(sketch, "E1107", {"start": v(-0.98, -1.84) * mm, "end": v(-0.9, -1.78) * mm});
            skLineSegment(sketch, "E1108", {"start": v(-0.9, -1.78) * mm, "end": v(-0.82, -1.71) * mm});
            skLineSegment(sketch, "E1109", {"start": v(-0.82, -1.71) * mm, "end": v(-0.74, -1.65) * mm});
            skLineSegment(sketch, "E1110", {"start": v(-0.74, -1.65) * mm, "end": v(-0.67, -1.58) * mm});
            skLineSegment(sketch, "E1111", {"start": v(-0.67, -1.58) * mm, "end": v(-0.64, -1.55) * mm});
            skLineSegment(sketch, "E1112", {"start": v(-0.64, -1.55) * mm, "end": v(-0.6, -1.59) * mm});
            skLineSegment(sketch, "E1113", {"start": v(-0.6, -1.59) * mm, "end": v(-0.58, -1.61) * mm});
            skLineSegment(sketch, "E1114", {"start": v(-0.58, -1.61) * mm, "end": v(-0.57, -1.64) * mm});
            skLineSegment(sketch, "E1115", {"start": v(-0.57, -1.64) * mm, "end": v(-0.57, -1.68) * mm});
            skLineSegment(sketch, "E1116", {"start": v(-0.57, -1.68) * mm, "end": v(-0.58, -1.7) * mm});
            skLineSegment(sketch, "E1117", {"start": v(-0.58, -1.7) * mm, "end": v(-0.58, -1.73) * mm});
            skLineSegment(sketch, "E1118", {"start": v(-0.58, -1.73) * mm, "end": v(-0.55, -1.75) * mm});
            skLineSegment(sketch, "E1119", {"start": v(-0.55, -1.75) * mm, "end": v(-0.52, -1.77) * mm});
            skLineSegment(sketch, "E1120", {"start": v(-0.52, -1.77) * mm, "end": v(-0.5, -1.8) * mm});
            skLineSegment(sketch, "E1121", {"start": v(-0.5, -1.8) * mm, "end": v(-0.48, -1.83) * mm});
            skLineSegment(sketch, "E1122", {"start": v(-0.48, -1.83) * mm, "end": v(-0.48, -1.86) * mm});
            skLineSegment(sketch, "E1123", {"start": v(-0.48, -1.86) * mm, "end": v(-0.48, -1.88) * mm});
            skLineSegment(sketch, "E1124", {"start": v(-0.48, -1.88) * mm, "end": v(-0.5, -1.9) * mm});
            skLineSegment(sketch, "E1125", {"start": v(-0.5, -1.9) * mm, "end": v(-0.52, -1.9) * mm});
            skLineSegment(sketch, "E1126", {"start": v(-0.52, -1.9) * mm, "end": v(-0.57, -1.91) * mm});
            skLineSegment(sketch, "E1127", {"start": v(-0.57, -1.91) * mm, "end": v(-0.6, -1.92) * mm});
            skLineSegment(sketch, "E1128", {"start": v(-0.6, -1.92) * mm, "end": v(-0.64, -1.93) * mm});
            skLineSegment(sketch, "E1129", {"start": v(-0.64, -1.93) * mm, "end": v(-0.68, -1.94) * mm});
            skLineSegment(sketch, "E1130", {"start": v(-0.68, -1.94) * mm, "end": v(-0.72, -1.96) * mm});
            skLineSegment(sketch, "E1131", {"start": v(-0.72, -1.96) * mm, "end": v(-0.8, -1.98) * mm});
            skLineSegment(sketch, "E1132", {"start": v(-0.8, -1.98) * mm, "end": v(-0.88, -2.02) * mm});
            skLineSegment(sketch, "E1133", {"start": v(-0.88, -2.02) * mm, "end": v(-0.97, -2.07) * mm});
            skLineSegment(sketch, "E1134", {"start": v(-0.97, -2.07) * mm, "end": v(-1.07, -2.12) * mm});
            skLineSegment(sketch, "E1135", {"start": v(-1.07, -2.12) * mm, "end": v(-1.15, -2.17) * mm});
            skLineSegment(sketch, "E1136", {"start": v(-1.15, -2.17) * mm, "end": v(-1.22, -2.21) * mm});
            skLineSegment(sketch, "E1137", {"start": v(-1.22, -2.21) * mm, "end": v(-1.27, -2.25) * mm});
            skLineSegment(sketch, "E1138", {"start": v(-1.27, -2.25) * mm, "end": v(-1.29, -2.27) * mm});
            skLineSegment(sketch, "E1139", {"start": v(-1.29, -2.27) * mm, "end": v(-1.28, -2.27) * mm});
            skLineSegment(sketch, "E1140", {"start": v(-1.28, -2.27) * mm, "end": v(-1.26, -2.26) * mm});
            skLineSegment(sketch, "E1141", {"start": v(-1.26, -2.26) * mm, "end": v(-1.25, -2.25) * mm});
            skLineSegment(sketch, "E1142", {"start": v(-1.25, -2.25) * mm, "end": v(-1.23, -2.24) * mm});
            skLineSegment(sketch, "E1143", {"start": v(-1.23, -2.24) * mm, "end": v(-1.2, -2.22) * mm});
            skLineSegment(sketch, "E1144", {"start": v(-1.2, -2.22) * mm, "end": v(-1.18, -2.2) * mm});
            skLineSegment(sketch, "E1145", {"start": v(-1.18, -2.2) * mm, "end": v(-1.13, -2.18) * mm});
            skLineSegment(sketch, "E1146", {"start": v(-1.13, -2.18) * mm, "end": v(-1.08, -2.15) * mm});
            skLineSegment(sketch, "E1147", {"start": v(-1.08, -2.15) * mm, "end": v(-1, -2.11) * mm});
            skLineSegment(sketch, "E1148", {"start": v(-1, -2.11) * mm, "end": v(-0.92, -2.06) * mm});
            skLineSegment(sketch, "E1149", {"start": v(-0.92, -2.06) * mm, "end": v(-0.87, -2.04) * mm});
            skLineSegment(sketch, "E1150", {"start": v(-0.87, -2.04) * mm, "end": v(-0.83, -2.01) * mm});
            skLineSegment(sketch, "E1151", {"start": v(-0.83, -2.01) * mm, "end": v(-0.8, -2) * mm});
            skLineSegment(sketch, "E1152", {"start": v(-0.8, -2) * mm, "end": v(-0.77, -1.99) * mm});
            skLineSegment(sketch, "E1153", {"start": v(-0.77, -1.99) * mm, "end": v(-0.74, -1.98) * mm});
            skLineSegment(sketch, "E1154", {"start": v(-0.74, -1.98) * mm, "end": v(-0.73, -1.98) * mm});
            skLineSegment(sketch, "E1155", {"start": v(-0.73, -1.98) * mm, "end": v(-0.71, -1.98) * mm});
            skLineSegment(sketch, "E1156", {"start": v(-0.71, -1.98) * mm, "end": v(-0.7, -2) * mm});
            skLineSegment(sketch, "E1157", {"start": v(-0.7, -2) * mm, "end": v(-0.68, -2.03) * mm});
            skLineSegment(sketch, "E1158", {"start": v(-0.68, -2.03) * mm, "end": v(-0.67, -2.05) * mm});
            skLineSegment(sketch, "E1159", {"start": v(-0.67, -2.05) * mm, "end": v(-0.66, -2.08) * mm});
            skLineSegment(sketch, "E1160", {"start": v(-0.66, -2.08) * mm, "end": v(-0.64, -2.11) * mm});
            skLineSegment(sketch, "E1161", {"start": v(-0.64, -2.11) * mm, "end": v(-0.62, -2.14) * mm});
            skLineSegment(sketch, "E1162", {"start": v(-0.62, -2.14) * mm, "end": v(-0.62, -2.17) * mm});
            skLineSegment(sketch, "E1163", {"start": v(-0.62, -2.17) * mm, "end": v(-0.63, -2.2) * mm});
            skLineSegment(sketch, "E1164", {"start": v(-0.63, -2.2) * mm, "end": v(-0.64, -2.22) * mm});
            skLineSegment(sketch, "E1165", {"start": v(-0.64, -2.22) * mm, "end": v(-0.67, -2.23) * mm});
            skLineSegment(sketch, "E1166", {"start": v(-0.67, -2.23) * mm, "end": v(-0.71, -2.23) * mm});
            skLineSegment(sketch, "E1167", {"start": v(-0.71, -2.23) * mm, "end": v(-0.75, -2.23) * mm});
            skLineSegment(sketch, "E1168", {"start": v(-0.75, -2.23) * mm, "end": v(-0.8, -2.24) * mm});
            skLineSegment(sketch, "E1169", {"start": v(-0.8, -2.24) * mm, "end": v(-0.86, -2.25) * mm});
            skLineSegment(sketch, "E1170", {"start": v(-0.86, -2.25) * mm, "end": v(-0.91, -2.26) * mm});
            skLineSegment(sketch, "E1171", {"start": v(-0.91, -2.26) * mm, "end": v(-0.97, -2.28) * mm});
            skLineSegment(sketch, "E1172", {"start": v(-0.97, -2.28) * mm, "end": v(-1, -2.29) * mm});
            skLineSegment(sketch, "E1173", {"start": v(-1, -2.29) * mm, "end": v(-1.04, -2.3) * mm});
            skLineSegment(sketch, "E1174", {"start": v(-1.04, -2.3) * mm, "end": v(-1.05, -2.3) * mm});
            skLineSegment(sketch, "E1175", {"start": v(-1.05, -2.3) * mm, "end": v(-1.06, -2.3) * mm});
            skLineSegment(sketch, "E1176", {"start": v(-1.06, -2.3) * mm, "end": v(-1.05, -2.32) * mm});
            skLineSegment(sketch, "E1177", {"start": v(-1.05, -2.32) * mm, "end": v(-1.01, -2.31) * mm});
            skLineSegment(sketch, "E1178", {"start": v(-1.01, -2.31) * mm, "end": v(-0.98, -2.31) * mm});
            skLineSegment(sketch, "E1179", {"start": v(-0.98, -2.31) * mm, "end": v(-0.95, -2.33) * mm});
            skLineSegment(sketch, "E1180", {"start": v(-0.95, -2.33) * mm, "end": v(-0.94, -2.35) * mm});
            skLineSegment(sketch, "E1181", {"start": v(-0.94, -2.35) * mm, "end": v(-0.95, -2.37) * mm});
            skLineSegment(sketch, "E1182", {"start": v(-0.95, -2.37) * mm, "end": v(-0.97, -2.38) * mm});
            skLineSegment(sketch, "E1183", {"start": v(-0.97, -2.38) * mm, "end": v(-1, -2.4) * mm});
            skLineSegment(sketch, "E1184", {"start": v(-1, -2.4) * mm, "end": v(-1.08, -2.42) * mm});
            skLineSegment(sketch, "E1185", {"start": v(-1.08, -2.42) * mm, "end": v(-1.18, -2.48) * mm});
            skLineSegment(sketch, "E1186", {"start": v(-1.18, -2.48) * mm, "end": v(-1.29, -2.56) * mm});
            skLineSegment(sketch, "E1187", {"start": v(-1.29, -2.56) * mm, "end": v(-1.4, -2.67) * mm});
            skLineSegment(sketch, "E1188", {"start": v(-1.4, -2.67) * mm, "end": v(-1.46, -2.73) * mm});
            skLineSegment(sketch, "E1189", {"start": v(-1.46, -2.73) * mm, "end": v(-1.55, -2.8) * mm});
            skLineSegment(sketch, "E1190", {"start": v(-1.55, -2.8) * mm, "end": v(-1.63, -2.84) * mm});
            skLineSegment(sketch, "E1191", {"start": v(-1.63, -2.84) * mm, "end": v(-1.7, -2.88) * mm});
            skLineSegment(sketch, "E1192", {"start": v(-1.7, -2.88) * mm, "end": v(-1.74, -2.9) * mm});
            skLineSegment(sketch, "E1193", {"start": v(-1.74, -2.9) * mm, "end": v(-1.75, -2.9) * mm});
            skLineSegment(sketch, "E1194", {"start": v(-1.75, -2.9) * mm, "end": v(-1.76, -2.94) * mm});
            skLineSegment(sketch, "E1195", {"start": v(-1.76, -2.94) * mm, "end": v(-1.78, -2.98) * mm});
            skLineSegment(sketch, "E1196", {"start": v(-1.78, -2.98) * mm, "end": v(-1.8, -3.02) * mm});
            skLineSegment(sketch, "E1197", {"start": v(-1.8, -3.02) * mm, "end": v(-1.83, -3.05) * mm});
            skLineSegment(sketch, "E1198", {"start": v(-1.83, -3.05) * mm, "end": v(-1.86, -3.07) * mm});
            skLineSegment(sketch, "E1199", {"start": v(-1.86, -3.07) * mm, "end": v(-1.9, -3.08) * mm});
            skLineSegment(sketch, "E1200", {"start": v(-1.9, -3.08) * mm, "end": v(-1.95, -3.09) * mm});
            skLineSegment(sketch, "E1201", {"start": v(-1.95, -3.09) * mm, "end": v(-2.01, -3.22) * mm});
            skLineSegment(sketch, "E1202", {"start": v(-2.01, -3.22) * mm, "end": v(-2.1, -3.43) * mm});
            skLineSegment(sketch, "E1203", {"start": v(-2.1, -3.43) * mm, "end": v(-2.16, -3.7) * mm});
            skLineSegment(sketch, "E1204", {"start": v(-2.16, -3.7) * mm, "end": v(-2.16, -3.7) * mm});
            skLineSegment(sketch, "E1205", {"start": v(-2.16, -3.7) * mm, "end": v(-2.16, -3.72) * mm});
            skLineSegment(sketch, "E1206", {"start": v(-2.16, -3.72) * mm, "end": v(-2.16, -3.71) * mm});
            skLineSegment(sketch, "E1207", {"start": v(-2.16, -3.71) * mm, "end": v(-2.15, -3.7) * mm});
            skLineSegment(sketch, "E1208", {"start": v(-2.15, -3.7) * mm, "end": v(-2.14, -3.69) * mm});
            skLineSegment(sketch, "E1209", {"start": v(-2.14, -3.69) * mm, "end": v(-2.13, -3.68) * mm});
            skLineSegment(sketch, "E1210", {"start": v(-2.13, -3.68) * mm, "end": v(-2.13, -3.67) * mm});
            skLineSegment(sketch, "E1211", {"start": v(-2.13, -3.67) * mm, "end": v(-2.12, -3.65) * mm});
            skLineSegment(sketch, "E1212", {"start": v(-2.12, -3.65) * mm, "end": v(-2.1, -3.63) * mm});
            skLineSegment(sketch, "E1213", {"start": v(-2.1, -3.63) * mm, "end": v(-2.1, -3.61) * mm});
            skLineSegment(sketch, "E1214", {"start": v(-2.1, -3.61) * mm, "end": v(-2.03, -3.5) * mm});
            skLineSegment(sketch, "E1215", {"start": v(-2.03, -3.5) * mm, "end": v(-1.93, -3.4) * mm});
            skLineSegment(sketch, "E1216", {"start": v(-1.93, -3.4) * mm, "end": v(-1.81, -3.32) * mm});
            skLineSegment(sketch, "E1217", {"start": v(-1.81, -3.32) * mm, "end": v(-1.7, -3.26) * mm});
            skLineSegment(sketch, "E1218", {"start": v(-1.7, -3.26) * mm, "end": v(-1.64, -3.25) * mm});
            skLineSegment(sketch, "E1219", {"start": v(-1.64, -3.25) * mm, "end": v(-1.58, -3.24) * mm});
            skLineSegment(sketch, "E1220", {"start": v(-1.58, -3.24) * mm, "end": v(-1.52, -3.24) * mm});
            skLineSegment(sketch, "E1221", {"start": v(-1.52, -3.24) * mm, "end": v(-1.5, -3.25) * mm});
            skLineSegment(sketch, "E1222", {"start": v(-1.5, -3.25) * mm, "end": v(-1.5, -3.27) * mm});
            skLineSegment(sketch, "E1223", {"start": v(-1.5, -3.27) * mm, "end": v(-1.5, -3.3) * mm});
            skLineSegment(sketch, "E1224", {"start": v(-1.5, -3.3) * mm, "end": v(-1.52, -3.32) * mm});
            skLineSegment(sketch, "E1225", {"start": v(-1.52, -3.32) * mm, "end": v(-1.56, -3.34) * mm});
            skLineSegment(sketch, "E1226", {"start": v(-1.56, -3.34) * mm, "end": v(-1.61, -3.39) * mm});
            skLineSegment(sketch, "E1227", {"start": v(-1.61, -3.39) * mm, "end": v(-1.68, -3.45) * mm});
            skLineSegment(sketch, "E1228", {"start": v(-1.68, -3.45) * mm, "end": v(-1.75, -3.52) * mm});
            skLineSegment(sketch, "E1229", {"start": v(-1.75, -3.52) * mm, "end": v(-1.8, -3.58) * mm});
            skLineSegment(sketch, "E1230", {"start": v(-1.8, -3.58) * mm, "end": v(-1.82, -3.62) * mm});
            skLineSegment(sketch, "E1231", {"start": v(-1.82, -3.62) * mm, "end": v(-1.85, -3.65) * mm});
            skLineSegment(sketch, "E1232", {"start": v(-1.85, -3.65) * mm, "end": v(-1.9, -3.72) * mm});
            skLineSegment(sketch, "E1233", {"start": v(-1.9, -3.72) * mm, "end": v(-1.99, -3.82) * mm});
            skLineSegment(sketch, "E1234", {"start": v(-1.99, -3.82) * mm, "end": v(-2.06, -3.92) * mm});
            skLineSegment(sketch, "E1235", {"start": v(-2.06, -3.92) * mm, "end": v(-2.1, -4) * mm});
            skLineSegment(sketch, "E1236", {"start": v(-2.1, -4) * mm, "end": v(-2.11, -4.03) * mm});
            skLineSegment(sketch, "E1237", {"start": v(-2.11, -4.03) * mm, "end": v(-2.12, -4.07) * mm});
            skLineSegment(sketch, "E1238", {"start": v(-2.12, -4.07) * mm, "end": v(-2.14, -4.1) * mm});
            skLineSegment(sketch, "E1239", {"start": v(-2.14, -4.1) * mm, "end": v(-2.15, -4.14) * mm});
            skLineSegment(sketch, "E1240", {"start": v(-2.15, -4.14) * mm, "end": v(-2.2, -4.24) * mm});
            skLineSegment(sketch, "E1241", {"start": v(-2.2, -4.24) * mm, "end": v(-2.22, -4.32) * mm});
            skLineSegment(sketch, "E1242", {"start": v(-2.22, -4.32) * mm, "end": v(-2.25, -4.4) * mm});
            skLineSegment(sketch, "E1243", {"start": v(-2.25, -4.4) * mm, "end": v(-2.27, -4.49) * mm});
            skLineSegment(sketch, "E1244", {"start": v(-2.27, -4.49) * mm, "end": v(-2.28, -4.58) * mm});
            skLineSegment(sketch, "E1245", {"start": v(-2.28, -4.58) * mm, "end": v(-2.3, -4.7) * mm});
            skLineSegment(sketch, "E1246", {"start": v(-2.3, -4.7) * mm, "end": v(-2.32, -4.85) * mm});
            skLineSegment(sketch, "E1247", {"start": v(-2.32, -4.85) * mm, "end": v(-2.34, -5.04) * mm});
            skLineSegment(sketch, "E1248", {"start": v(-2.34, -5.04) * mm, "end": v(-2.35, -5.17) * mm});
            skLineSegment(sketch, "E1249", {"start": v(-2.35, -5.17) * mm, "end": v(-2.4, -5.18) * mm});
            skLineSegment(sketch, "E1250", {"start": v(-2.4, -5.18) * mm, "end": v(-2.43, -5.19) * mm});
            skLineSegment(sketch, "E1251", {"start": v(-2.43, -5.19) * mm, "end": v(-2.48, -5.2) * mm});
            skLineSegment(sketch, "E1252", {"start": v(-2.48, -5.2) * mm, "end": v(-2.52, -5.2) * mm});
            skLineSegment(sketch, "E1253", {"start": v(-2.52, -5.2) * mm, "end": v(-2.53, -5.1) * mm});
            skLineSegment(sketch, "E1254", {"start": v(-1.6, -2.76) * mm, "end": v(-1.56, -2.73) * mm});
            skLineSegment(sketch, "E1255", {"start": v(-1.56, -2.73) * mm, "end": v(-1.5, -2.69) * mm});
            skLineSegment(sketch, "E1256", {"start": v(-1.5, -2.69) * mm, "end": v(-1.45, -2.64) * mm});
            skLineSegment(sketch, "E1257", {"start": v(-1.45, -2.64) * mm, "end": v(-1.4, -2.6) * mm});
            skLineSegment(sketch, "E1258", {"start": v(-1.4, -2.6) * mm, "end": v(-1.31, -2.5) * mm});
            skLineSegment(sketch, "E1259", {"start": v(-1.31, -2.5) * mm, "end": v(-1.23, -2.44) * mm});
            skLineSegment(sketch, "E1260", {"start": v(-1.23, -2.44) * mm, "end": v(-1.17, -2.4) * mm});
            skLineSegment(sketch, "E1261", {"start": v(-1.17, -2.4) * mm, "end": v(-1.11, -2.36) * mm});
            skLineSegment(sketch, "E1262", {"start": v(-1.11, -2.36) * mm, "end": v(-1.1, -2.35) * mm});
            skLineSegment(sketch, "E1263", {"start": v(-1.1, -2.35) * mm, "end": v(-1.1, -2.34) * mm});
            skLineSegment(sketch, "E1264", {"start": v(-1.1, -2.34) * mm, "end": v(-1.12, -2.33) * mm});
            skLineSegment(sketch, "E1265", {"start": v(-1.12, -2.33) * mm, "end": v(-1.16, -2.33) * mm});
            skLineSegment(sketch, "E1266", {"start": v(-1.16, -2.33) * mm, "end": v(-1.22, -2.32) * mm});
            skLineSegment(sketch, "E1267", {"start": v(-1.22, -2.32) * mm, "end": v(-1.28, -2.34) * mm});
            skLineSegment(sketch, "E1268", {"start": v(-1.28, -2.34) * mm, "end": v(-1.31, -2.35) * mm});
            skLineSegment(sketch, "E1269", {"start": v(-1.31, -2.35) * mm, "end": v(-1.34, -2.35) * mm});
            skLineSegment(sketch, "E1270", {"start": v(-1.34, -2.35) * mm, "end": v(-1.35, -2.35) * mm});
            skLineSegment(sketch, "E1271", {"start": v(-1.35, -2.35) * mm, "end": v(-1.36, -2.34) * mm});
            skLineSegment(sketch, "E1272", {"start": v(-1.36, -2.34) * mm, "end": v(-1.37, -2.33) * mm});
            skLineSegment(sketch, "E1273", {"start": v(-1.37, -2.33) * mm, "end": v(-1.38, -2.31) * mm});
            skLineSegment(sketch, "E1274", {"start": v(-1.38, -2.31) * mm, "end": v(-1.37, -2.29) * mm});
            skLineSegment(sketch, "E1275", {"start": v(-1.37, -2.29) * mm, "end": v(-1.36, -2.26) * mm});
            skLineSegment(sketch, "E1276", {"start": v(-1.36, -2.26) * mm, "end": v(-1.34, -2.23) * mm});
            skLineSegment(sketch, "E1277", {"start": v(-1.34, -2.23) * mm, "end": v(-1.32, -2.2) * mm});
            skLineSegment(sketch, "E1278", {"start": v(-1.32, -2.2) * mm, "end": v(-1.3, -2.15) * mm});
            skLineSegment(sketch, "E1279", {"start": v(-1.3, -2.15) * mm, "end": v(-1.3, -2.07) * mm});
            skLineSegment(sketch, "E1280", {"start": v(-1.3, -2.07) * mm, "end": v(-1.29, -2) * mm});
            skLineSegment(sketch, "E1281", {"start": v(-1.29, -2) * mm, "end": v(-1.3, -1.96) * mm});
            skLineSegment(sketch, "E1282", {"start": v(-1.3, -1.96) * mm, "end": v(-1.31, -1.97) * mm});
            skLineSegment(sketch, "E1283", {"start": v(-1.31, -1.97) * mm, "end": v(-1.35, -1.98) * mm});
            skLineSegment(sketch, "E1284", {"start": v(-1.35, -1.98) * mm, "end": v(-1.4, -2) * mm});
            skLineSegment(sketch, "E1285", {"start": v(-1.4, -2) * mm, "end": v(-1.47, -2.05) * mm});
            skLineSegment(sketch, "E1286", {"start": v(-1.47, -2.05) * mm, "end": v(-1.52, -2.1) * mm});
            skLineSegment(sketch, "E1287", {"start": v(-1.52, -2.1) * mm, "end": v(-1.55, -2.14) * mm});
            skLineSegment(sketch, "E1288", {"start": v(-1.55, -2.14) * mm, "end": v(-1.57, -2.17) * mm});
            skLineSegment(sketch, "E1289", {"start": v(-1.57, -2.17) * mm, "end": v(-1.6, -2.19) * mm});
            skLineSegment(sketch, "E1290", {"start": v(-1.6, -2.19) * mm, "end": v(-1.62, -2.2) * mm});
            skLineSegment(sketch, "E1291", {"start": v(-1.62, -2.2) * mm, "end": v(-1.64, -2.19) * mm});
            skLineSegment(sketch, "E1292", {"start": v(-1.64, -2.19) * mm, "end": v(-1.65, -2.17) * mm});
            skLineSegment(sketch, "E1293", {"start": v(-1.65, -2.17) * mm, "end": v(-1.66, -2.12) * mm});
            skLineSegment(sketch, "E1294", {"start": v(-1.66, -2.12) * mm, "end": v(-1.67, -2.08) * mm});
            skLineSegment(sketch, "E1295", {"start": v(-1.67, -2.08) * mm, "end": v(-1.68, -2.04) * mm});
            skLineSegment(sketch, "E1296", {"start": v(-1.68, -2.04) * mm, "end": v(-1.7, -2) * mm});
            skLineSegment(sketch, "E1297", {"start": v(-1.7, -2) * mm, "end": v(-1.74, -1.95) * mm});
            skLineSegment(sketch, "E1298", {"start": v(-1.74, -1.95) * mm, "end": v(-1.75, -1.94) * mm});
            skLineSegment(sketch, "E1299", {"start": v(-1.75, -1.94) * mm, "end": v(-1.75, -1.95) * mm});
            skLineSegment(sketch, "E1300", {"start": v(-1.75, -1.95) * mm, "end": v(-1.76, -1.98) * mm});
            skLineSegment(sketch, "E1301", {"start": v(-1.76, -1.98) * mm, "end": v(-1.76, -2.04) * mm});
            skLineSegment(sketch, "E1302", {"start": v(-1.76, -2.04) * mm, "end": v(-1.76, -2.1) * mm});
            skLineSegment(sketch, "E1303", {"start": v(-1.76, -2.1) * mm, "end": v(-1.78, -2.16) * mm});
            skLineSegment(sketch, "E1304", {"start": v(-1.78, -2.16) * mm, "end": v(-1.8, -2.23) * mm});
            skLineSegment(sketch, "E1305", {"start": v(-1.8, -2.23) * mm, "end": v(-1.84, -2.33) * mm});
            skLineSegment(sketch, "E1306", {"start": v(-1.84, -2.33) * mm, "end": v(-1.9, -2.5) * mm});
            skLineSegment(sketch, "E1307", {"start": v(-1.9, -2.5) * mm, "end": v(-1.94, -2.62) * mm});
            skLineSegment(sketch, "E1308", {"start": v(-1.94, -2.62) * mm, "end": v(-1.95, -2.7) * mm});
            skLineSegment(sketch, "E1309", {"start": v(-1.95, -2.7) * mm, "end": v(-1.93, -2.76) * mm});
            skLineSegment(sketch, "E1310", {"start": v(-1.93, -2.76) * mm, "end": v(-1.92, -2.76) * mm});
            skLineSegment(sketch, "E1311", {"start": v(-1.92, -2.76) * mm, "end": v(-1.92, -2.75) * mm});
            skLineSegment(sketch, "E1312", {"start": v(-1.92, -2.75) * mm, "end": v(-1.92, -2.73) * mm});
            skLineSegment(sketch, "E1313", {"start": v(-1.92, -2.73) * mm, "end": v(-1.92, -2.69) * mm});
            skLineSegment(sketch, "E1314", {"start": v(-1.92, -2.69) * mm, "end": v(-1.92, -2.6) * mm});
            skLineSegment(sketch, "E1315", {"start": v(-1.92, -2.6) * mm, "end": v(-1.85, -2.49) * mm});
            skLineSegment(sketch, "E1316", {"start": v(-1.85, -2.49) * mm, "end": v(-1.82, -2.45) * mm});
            skLineSegment(sketch, "E1317", {"start": v(-1.82, -2.45) * mm, "end": v(-1.8, -2.4) * mm});
            skLineSegment(sketch, "E1318", {"start": v(-1.8, -2.4) * mm, "end": v(-1.77, -2.38) * mm});
            skLineSegment(sketch, "E1319", {"start": v(-1.77, -2.38) * mm, "end": v(-1.76, -2.38) * mm});
            skLineSegment(sketch, "E1320", {"start": v(-1.76, -2.38) * mm, "end": v(-1.76, -2.39) * mm});
            skLineSegment(sketch, "E1321", {"start": v(-1.76, -2.39) * mm, "end": v(-1.76, -2.41) * mm});
            skLineSegment(sketch, "E1322", {"start": v(-1.76, -2.41) * mm, "end": v(-1.76, -2.43) * mm});
            skLineSegment(sketch, "E1323", {"start": v(-1.76, -2.43) * mm, "end": v(-1.76, -2.47) * mm});
            skLineSegment(sketch, "E1324", {"start": v(-1.76, -2.47) * mm, "end": v(-1.76, -2.5) * mm});
            skLineSegment(sketch, "E1325", {"start": v(-1.76, -2.5) * mm, "end": v(-1.75, -2.55) * mm});
            skLineSegment(sketch, "E1326", {"start": v(-1.75, -2.55) * mm, "end": v(-1.74, -2.6) * mm});
            skLineSegment(sketch, "E1327", {"start": v(-1.74, -2.6) * mm, "end": v(-1.73, -2.62) * mm});
            skLineSegment(sketch, "E1328", {"start": v(-1.73, -2.62) * mm, "end": v(-1.72, -2.63) * mm});
            skLineSegment(sketch, "E1329", {"start": v(-1.72, -2.63) * mm, "end": v(-1.71, -2.63) * mm});
            skLineSegment(sketch, "E1330", {"start": v(-1.71, -2.63) * mm, "end": v(-1.7, -2.61) * mm});
            skLineSegment(sketch, "E1331", {"start": v(-1.7, -2.61) * mm, "end": v(-1.67, -2.6) * mm});
            skLineSegment(sketch, "E1332", {"start": v(-1.67, -2.6) * mm, "end": v(-1.64, -2.59) * mm});
            skLineSegment(sketch, "E1333", {"start": v(-1.64, -2.59) * mm, "end": v(-1.6, -2.58) * mm});
            skLineSegment(sketch, "E1334", {"start": v(-1.6, -2.58) * mm, "end": v(-1.57, -2.57) * mm});
            skLineSegment(sketch, "E1335", {"start": v(-1.57, -2.57) * mm, "end": v(-1.55, -2.57) * mm});
            skLineSegment(sketch, "E1336", {"start": v(-1.55, -2.57) * mm, "end": v(-1.53, -2.57) * mm});
            skLineSegment(sketch, "E1337", {"start": v(-1.53, -2.57) * mm, "end": v(-1.52, -2.58) * mm});
            skLineSegment(sketch, "E1338", {"start": v(-1.52, -2.58) * mm, "end": v(-1.53, -2.6) * mm});
            skLineSegment(sketch, "E1339", {"start": v(-1.53, -2.6) * mm, "end": v(-1.54, -2.62) * mm});
            skLineSegment(sketch, "E1340", {"start": v(-1.54, -2.62) * mm, "end": v(-1.56, -2.65) * mm});
            skLineSegment(sketch, "E1341", {"start": v(-1.56, -2.65) * mm, "end": v(-1.58, -2.68) * mm});
            skLineSegment(sketch, "E1342", {"start": v(-1.58, -2.68) * mm, "end": v(-1.6, -2.7) * mm});
            skLineSegment(sketch, "E1343", {"start": v(-1.6, -2.7) * mm, "end": v(-1.62, -2.74) * mm});
            skLineSegment(sketch, "E1344", {"start": v(-1.62, -2.74) * mm, "end": v(-1.64, -2.76) * mm});
            skLineSegment(sketch, "E1345", {"start": v(-1.64, -2.76) * mm, "end": v(-1.66, -2.78) * mm});
            skLineSegment(sketch, "E1346", {"start": v(-1.66, -2.78) * mm, "end": v(-1.68, -2.8) * mm});
            skLineSegment(sketch, "E1347", {"start": v(-1.68, -2.8) * mm, "end": v(-1.7, -2.8) * mm});
            skLineSegment(sketch, "E1348", {"start": v(-1.7, -2.8) * mm, "end": v(-1.7, -2.81) * mm});
            skLineSegment(sketch, "E1349", {"start": v(-1.7, -2.81) * mm, "end": v(-1.71, -2.82) * mm});
            skLineSegment(sketch, "E1350", {"start": v(-1.71, -2.82) * mm, "end": v(-1.7, -2.82) * mm});
            skLineSegment(sketch, "E1351", {"start": v(-1.7, -2.82) * mm, "end": v(-1.7, -2.81) * mm});
            skLineSegment(sketch, "E1352", {"start": v(-1.7, -2.81) * mm, "end": v(-1.66, -2.8) * mm});
            skLineSegment(sketch, "E1353", {"start": v(-1.66, -2.8) * mm, "end": v(-1.6, -2.76) * mm});
            skLineSegment(sketch, "E1354", {"start": v(-4.92, -2.4) * mm, "end": v(-4.87, -2.37) * mm});
            skLineSegment(sketch, "E1355", {"start": v(-4.87, -2.37) * mm, "end": v(-4.82, -2.34) * mm});
            skLineSegment(sketch, "E1356", {"start": v(-4.82, -2.34) * mm, "end": v(-4.8, -2.33) * mm});
            skLineSegment(sketch, "E1357", {"start": v(-4.8, -2.33) * mm, "end": v(-4.77, -2.3) * mm});
            skLineSegment(sketch, "E1358", {"start": v(-4.77, -2.3) * mm, "end": v(-4.73, -2.28) * mm});
            skLineSegment(sketch, "E1359", {"start": v(-4.73, -2.28) * mm, "end": v(-4.69, -2.26) * mm});
            skLineSegment(sketch, "E1360", {"start": v(-4.69, -2.26) * mm, "end": v(-4.6, -2.2) * mm});
            skLineSegment(sketch, "E1361", {"start": v(-4.6, -2.2) * mm, "end": v(-4.72, -2.21) * mm});
            skLineSegment(sketch, "E1362", {"start": v(-4.72, -2.21) * mm, "end": v(-4.9, -2.24) * mm});
            skLineSegment(sketch, "E1363", {"start": v(-4.9, -2.24) * mm, "end": v(-5.02, -2.28) * mm});
            skLineSegment(sketch, "E1364", {"start": v(-5.02, -2.28) * mm, "end": v(-5.06, -2.3) * mm});
            skLineSegment(sketch, "E1365", {"start": v(-5.06, -2.3) * mm, "end": v(-5.03, -2.32) * mm});
            skLineSegment(sketch, "E1366", {"start": v(-5.03, -2.32) * mm, "end": v(-5.02, -2.34) * mm});
            skLineSegment(sketch, "E1367", {"start": v(-5.02, -2.34) * mm, "end": v(-5.02, -2.35) * mm});
            skLineSegment(sketch, "E1368", {"start": v(-5.02, -2.35) * mm, "end": v(-5.02, -2.37) * mm});
            skLineSegment(sketch, "E1369", {"start": v(-5.02, -2.37) * mm, "end": v(-5.03, -2.4) * mm});
            skLineSegment(sketch, "E1370", {"start": v(-5.03, -2.4) * mm, "end": v(-5.03, -2.42) * mm});
            skLineSegment(sketch, "E1371", {"start": v(-5.03, -2.42) * mm, "end": v(-5, -2.42) * mm});
            skLineSegment(sketch, "E1372", {"start": v(-5, -2.42) * mm, "end": v(-4.97, -2.41) * mm});
            skLineSegment(sketch, "E1373", {"start": v(-4.97, -2.41) * mm, "end": v(-4.92, -2.4) * mm});
            skLineSegment(sketch, "E1374", {"start": v(-4.05, -2.4) * mm, "end": v(-4, -2.38) * mm});
            skLineSegment(sketch, "E1375", {"start": v(-4, -2.38) * mm, "end": v(-3.95, -2.36) * mm});
            skLineSegment(sketch, "E1376", {"start": v(-3.95, -2.36) * mm, "end": v(-3.9, -2.34) * mm});
            skLineSegment(sketch, "E1377", {"start": v(-3.9, -2.34) * mm, "end": v(-3.83, -2.32) * mm});
            skLineSegment(sketch, "E1378", {"start": v(-3.83, -2.32) * mm, "end": v(-3.79, -2.3) * mm});
            skLineSegment(sketch, "E1379", {"start": v(-3.79, -2.3) * mm, "end": v(-3.77, -2.3) * mm});
            skLineSegment(sketch, "E1380", {"start": v(-3.77, -2.3) * mm, "end": v(-3.77, -2.28) * mm});
            skLineSegment(sketch, "E1381", {"start": v(-3.77, -2.28) * mm, "end": v(-3.78, -2.25) * mm});
            skLineSegment(sketch, "E1382", {"start": v(-3.78, -2.25) * mm, "end": v(-3.8, -2.2) * mm});
            skLineSegment(sketch, "E1383", {"start": v(-3.8, -2.2) * mm, "end": v(-3.83, -2.15) * mm});
            skLineSegment(sketch, "E1384", {"start": v(-3.83, -2.15) * mm, "end": v(-3.85, -2.1) * mm});
            skLineSegment(sketch, "E1385", {"start": v(-3.85, -2.1) * mm, "end": v(-3.87, -2.05) * mm});
            skLineSegment(sketch, "E1386", {"start": v(-3.87, -2.05) * mm, "end": v(-3.9, -2.01) * mm});
            skLineSegment(sketch, "E1387", {"start": v(-3.9, -2.01) * mm, "end": v(-3.9, -1.99) * mm});
            skLineSegment(sketch, "E1388", {"start": v(-3.9, -1.99) * mm, "end": v(-3.88, -1.98) * mm});
            skLineSegment(sketch, "E1389", {"start": v(-3.88, -1.98) * mm, "end": v(-3.84, -1.98) * mm});
            skLineSegment(sketch, "E1390", {"start": v(-3.84, -1.98) * mm, "end": v(-3.78, -1.99) * mm});
            skLineSegment(sketch, "E1391", {"start": v(-3.78, -1.99) * mm, "end": v(-3.73, -2.01) * mm});
            skLineSegment(sketch, "E1392", {"start": v(-3.73, -2.01) * mm, "end": v(-3.7, -2.04) * mm});
            skLineSegment(sketch, "E1393", {"start": v(-3.7, -2.04) * mm, "end": v(-3.64, -2.07) * mm});
            skLineSegment(sketch, "E1394", {"start": v(-3.64, -2.07) * mm, "end": v(-3.61, -2.08) * mm});
            skLineSegment(sketch, "E1395", {"start": v(-3.61, -2.08) * mm, "end": v(-3.6, -2.1) * mm});
            skLineSegment(sketch, "E1396", {"start": v(-3.6, -2.1) * mm, "end": v(-3.6, -2.09) * mm});
            skLineSegment(sketch, "E1397", {"start": v(-3.6, -2.09) * mm, "end": v(-3.6, -2.08) * mm});
            skLineSegment(sketch, "E1398", {"start": v(-3.6, -2.08) * mm, "end": v(-3.6, -2.03) * mm});
            skLineSegment(sketch, "E1399", {"start": v(-3.6, -2.03) * mm, "end": v(-3.58, -1.94) * mm});
            skLineSegment(sketch, "E1400", {"start": v(-3.58, -1.94) * mm, "end": v(-3.56, -1.85) * mm});
            skLineSegment(sketch, "E1401", {"start": v(-3.56, -1.85) * mm, "end": v(-3.55, -1.8) * mm});
            skLineSegment(sketch, "E1402", {"start": v(-3.55, -1.8) * mm, "end": v(-3.54, -1.78) * mm});
            skLineSegment(sketch, "E1403", {"start": v(-3.54, -1.78) * mm, "end": v(-3.52, -1.76) * mm});
            skLineSegment(sketch, "E1404", {"start": v(-3.52, -1.76) * mm, "end": v(-3.51, -1.74) * mm});
            skLineSegment(sketch, "E1405", {"start": v(-3.51, -1.74) * mm, "end": v(-3.5, -1.73) * mm});
            skLineSegment(sketch, "E1406", {"start": v(-3.5, -1.73) * mm, "end": v(-3.51, -1.7) * mm});
            skLineSegment(sketch, "E1407", {"start": v(-3.51, -1.7) * mm, "end": v(-3.52, -1.67) * mm});
            skLineSegment(sketch, "E1408", {"start": v(-3.52, -1.67) * mm, "end": v(-3.54, -1.6) * mm});
            skLineSegment(sketch, "E1409", {"start": v(-3.54, -1.6) * mm, "end": v(-3.55, -1.5) * mm});
            skLineSegment(sketch, "E1410", {"start": v(-3.55, -1.5) * mm, "end": v(-3.55, -1.42) * mm});
            skLineSegment(sketch, "E1411", {"start": v(-3.55, -1.42) * mm, "end": v(-3.54, -1.35) * mm});
            skLineSegment(sketch, "E1412", {"start": v(-3.54, -1.35) * mm, "end": v(-3.53, -1.32) * mm});
            skLineSegment(sketch, "E1413", {"start": v(-3.53, -1.32) * mm, "end": v(-3.53, -1.3) * mm});
            skLineSegment(sketch, "E1414", {"start": v(-3.53, -1.3) * mm, "end": v(-3.53, -1.3) * mm});
            skLineSegment(sketch, "E1415", {"start": v(-3.53, -1.3) * mm, "end": v(-3.55, -1.3) * mm});
            skLineSegment(sketch, "E1416", {"start": v(-3.55, -1.3) * mm, "end": v(-3.57, -1.31) * mm});
            skLineSegment(sketch, "E1417", {"start": v(-3.57, -1.31) * mm, "end": v(-3.59, -1.33) * mm});
            skLineSegment(sketch, "E1418", {"start": v(-3.59, -1.33) * mm, "end": v(-3.6, -1.34) * mm});
            skLineSegment(sketch, "E1419", {"start": v(-3.6, -1.34) * mm, "end": v(-3.63, -1.35) * mm});
            skLineSegment(sketch, "E1420", {"start": v(-3.63, -1.35) * mm, "end": v(-3.65, -1.36) * mm});
            skLineSegment(sketch, "E1421", {"start": v(-3.65, -1.36) * mm, "end": v(-3.66, -1.37) * mm});
            skLineSegment(sketch, "E1422", {"start": v(-3.66, -1.37) * mm, "end": v(-3.68, -1.4) * mm});
            skLineSegment(sketch, "E1423", {"start": v(-3.68, -1.4) * mm, "end": v(-3.7, -1.42) * mm});
            skLineSegment(sketch, "E1424", {"start": v(-3.7, -1.42) * mm, "end": v(-3.73, -1.45) * mm});
            skLineSegment(sketch, "E1425", {"start": v(-3.73, -1.45) * mm, "end": v(-3.76, -1.48) * mm});
            skLineSegment(sketch, "E1426", {"start": v(-3.76, -1.48) * mm, "end": v(-3.79, -1.51) * mm});
            skLineSegment(sketch, "E1427", {"start": v(-3.79, -1.51) * mm, "end": v(-3.8, -1.54) * mm});
            skLineSegment(sketch, "E1428", {"start": v(-3.8, -1.54) * mm, "end": v(-3.83, -1.57) * mm});
            skLineSegment(sketch, "E1429", {"start": v(-3.83, -1.57) * mm, "end": v(-3.84, -1.59) * mm});
            skLineSegment(sketch, "E1430", {"start": v(-3.84, -1.59) * mm, "end": v(-3.86, -1.63) * mm});
            skLineSegment(sketch, "E1431", {"start": v(-3.86, -1.63) * mm, "end": v(-3.87, -1.7) * mm});
            skLineSegment(sketch, "E1432", {"start": v(-3.87, -1.7) * mm, "end": v(-3.88, -1.77) * mm});
            skLineSegment(sketch, "E1433", {"start": v(-3.88, -1.77) * mm, "end": v(-3.89, -1.84) * mm});
            skLineSegment(sketch, "E1434", {"start": v(-3.89, -1.84) * mm, "end": v(-3.9, -1.88) * mm});
            skLineSegment(sketch, "E1435", {"start": v(-3.9, -1.88) * mm, "end": v(-3.9, -1.9) * mm});
            skLineSegment(sketch, "E1436", {"start": v(-3.9, -1.9) * mm, "end": v(-3.9, -1.9) * mm});
            skLineSegment(sketch, "E1437", {"start": v(-3.9, -1.9) * mm, "end": v(-3.92, -1.9) * mm});
            skLineSegment(sketch, "E1438", {"start": v(-3.92, -1.9) * mm, "end": v(-3.94, -1.9) * mm});
            skLineSegment(sketch, "E1439", {"start": v(-3.94, -1.9) * mm, "end": v(-3.96, -1.88) * mm});
            skLineSegment(sketch, "E1440", {"start": v(-3.96, -1.88) * mm, "end": v(-3.98, -1.86) * mm});
            skLineSegment(sketch, "E1441", {"start": v(-3.98, -1.86) * mm, "end": v(-4, -1.84) * mm});
            skLineSegment(sketch, "E1442", {"start": v(-4, -1.84) * mm, "end": v(-4.02, -1.82) * mm});
            skLineSegment(sketch, "E1443", {"start": v(-4.02, -1.82) * mm, "end": v(-4.05, -1.8) * mm});
            skLineSegment(sketch, "E1444", {"start": v(-4.05, -1.8) * mm, "end": v(-4.07, -1.79) * mm});
            skLineSegment(sketch, "E1445", {"start": v(-4.07, -1.79) * mm, "end": v(-4.09, -1.78) * mm});
            skLineSegment(sketch, "E1446", {"start": v(-4.09, -1.78) * mm, "end": v(-4.1, -1.77) * mm});
            skLineSegment(sketch, "E1447", {"start": v(-4.1, -1.77) * mm, "end": v(-4.1, -1.77) * mm});
            skLineSegment(sketch, "E1448", {"start": v(-4.1, -1.77) * mm, "end": v(-4.12, -1.77) * mm});
            skLineSegment(sketch, "E1449", {"start": v(-4.12, -1.77) * mm, "end": v(-4.14, -1.76) * mm});
            skLineSegment(sketch, "E1450", {"start": v(-4.14, -1.76) * mm, "end": v(-4.17, -1.73) * mm});
            skLineSegment(sketch, "E1451", {"start": v(-4.17, -1.73) * mm, "end": v(-4.23, -1.71) * mm});
            skLineSegment(sketch, "E1452", {"start": v(-4.23, -1.71) * mm, "end": v(-4.28, -1.7) * mm});
            skLineSegment(sketch, "E1453", {"start": v(-4.28, -1.7) * mm, "end": v(-4.32, -1.69) * mm});
            skLineSegment(sketch, "E1454", {"start": v(-4.32, -1.69) * mm, "end": v(-4.33, -1.69) * mm});
            skLineSegment(sketch, "E1455", {"start": v(-4.33, -1.69) * mm, "end": v(-4.33, -1.7) * mm});
            skLineSegment(sketch, "E1456", {"start": v(-4.33, -1.7) * mm, "end": v(-4.32, -1.72) * mm});
            skLineSegment(sketch, "E1457", {"start": v(-4.32, -1.72) * mm, "end": v(-4.3, -1.76) * mm});
            skLineSegment(sketch, "E1458", {"start": v(-4.3, -1.76) * mm, "end": v(-4.28, -1.79) * mm});
            skLineSegment(sketch, "E1459", {"start": v(-4.28, -1.79) * mm, "end": v(-4.26, -1.83) * mm});
            skLineSegment(sketch, "E1460", {"start": v(-4.26, -1.83) * mm, "end": v(-4.23, -1.87) * mm});
            skLineSegment(sketch, "E1461", {"start": v(-4.23, -1.87) * mm, "end": v(-4.21, -1.9) * mm});
            skLineSegment(sketch, "E1462", {"start": v(-4.21, -1.9) * mm, "end": v(-4.19, -1.95) * mm});
            skLineSegment(sketch, "E1463", {"start": v(-4.19, -1.95) * mm, "end": v(-4.16, -2) * mm});
            skLineSegment(sketch, "E1464", {"start": v(-4.16, -2) * mm, "end": v(-4.13, -2.05) * mm});
            skLineSegment(sketch, "E1465", {"start": v(-4.13, -2.05) * mm, "end": v(-4.1, -2.1) * mm});
            skLineSegment(sketch, "E1466", {"start": v(-4.1, -2.1) * mm, "end": v(-4.07, -2.13) * mm});
            skLineSegment(sketch, "E1467", {"start": v(-4.07, -2.13) * mm, "end": v(-4.06, -2.15) * mm});
            skLineSegment(sketch, "E1468", {"start": v(-4.06, -2.15) * mm, "end": v(-4.05, -2.17) * mm});
            skLineSegment(sketch, "E1469", {"start": v(-4.05, -2.17) * mm, "end": v(-4.04, -2.18) * mm});
            skLineSegment(sketch, "E1470", {"start": v(-4.04, -2.18) * mm, "end": v(-4.04, -2.2) * mm});
            skLineSegment(sketch, "E1471", {"start": v(-4.04, -2.2) * mm, "end": v(-4.04, -2.2) * mm});
            skLineSegment(sketch, "E1472", {"start": v(-4.04, -2.2) * mm, "end": v(-4.05, -2.2) * mm});
            skLineSegment(sketch, "E1473", {"start": v(-4.05, -2.2) * mm, "end": v(-4.07, -2.2) * mm});
            skLineSegment(sketch, "E1474", {"start": v(-4.07, -2.2) * mm, "end": v(-4.12, -2.21) * mm});
            skLineSegment(sketch, "E1475", {"start": v(-4.12, -2.21) * mm, "end": v(-4.18, -2.23) * mm});
            skLineSegment(sketch, "E1476", {"start": v(-4.18, -2.23) * mm, "end": v(-4.25, -2.24) * mm});
            skLineSegment(sketch, "E1477", {"start": v(-4.25, -2.24) * mm, "end": v(-4.32, -2.25) * mm});
            skLineSegment(sketch, "E1478", {"start": v(-4.32, -2.25) * mm, "end": v(-4.38, -2.26) * mm});
            skLineSegment(sketch, "E1479", {"start": v(-4.38, -2.26) * mm, "end": v(-4.44, -2.28) * mm});
            skLineSegment(sketch, "E1480", {"start": v(-4.44, -2.28) * mm, "end": v(-4.47, -2.29) * mm});
            skLineSegment(sketch, "E1481", {"start": v(-4.47, -2.29) * mm, "end": v(-4.5, -2.3) * mm});
            skLineSegment(sketch, "E1482", {"start": v(-4.5, -2.3) * mm, "end": v(-4.53, -2.31) * mm});
            skLineSegment(sketch, "E1483", {"start": v(-4.53, -2.31) * mm, "end": v(-4.56, -2.33) * mm});
            skLineSegment(sketch, "E1484", {"start": v(-4.56, -2.33) * mm, "end": v(-4.58, -2.35) * mm});
            skLineSegment(sketch, "E1485", {"start": v(-4.58, -2.35) * mm, "end": v(-4.6, -2.36) * mm});
            skLineSegment(sketch, "E1486", {"start": v(-4.6, -2.36) * mm, "end": v(-4.62, -2.38) * mm});
            skLineSegment(sketch, "E1487", {"start": v(-4.62, -2.38) * mm, "end": v(-4.62, -2.38) * mm});
            skLineSegment(sketch, "E1488", {"start": v(-4.62, -2.38) * mm, "end": v(-4.61, -2.38) * mm});
            skLineSegment(sketch, "E1489", {"start": v(-4.61, -2.38) * mm, "end": v(-4.55, -2.37) * mm});
            skLineSegment(sketch, "E1490", {"start": v(-4.55, -2.37) * mm, "end": v(-4.46, -2.37) * mm});
            skLineSegment(sketch, "E1491", {"start": v(-4.46, -2.37) * mm, "end": v(-4.35, -2.38) * mm});
            skLineSegment(sketch, "E1492", {"start": v(-4.35, -2.38) * mm, "end": v(-4.26, -2.4) * mm});
            skLineSegment(sketch, "E1493", {"start": v(-4.26, -2.4) * mm, "end": v(-4.21, -2.4) * mm});
            skLineSegment(sketch, "E1494", {"start": v(-4.21, -2.4) * mm, "end": v(-4.18, -2.41) * mm});
            skLineSegment(sketch, "E1495", {"start": v(-4.18, -2.41) * mm, "end": v(-4.15, -2.42) * mm});
            skLineSegment(sketch, "E1496", {"start": v(-4.15, -2.42) * mm, "end": v(-4.13, -2.42) * mm});
            skLineSegment(sketch, "E1497", {"start": v(-4.13, -2.42) * mm, "end": v(-4.11, -2.42) * mm});
            skLineSegment(sketch, "E1498", {"start": v(-4.11, -2.42) * mm, "end": v(-4.1, -2.41) * mm});
            skLineSegment(sketch, "E1499", {"start": v(-4.1, -2.41) * mm, "end": v(-4.08, -2.4) * mm});
            skLineSegment(sketch, "E1500", {"start": v(-4.08, -2.4) * mm, "end": v(-4.05, -2.4) * mm});
            skLineSegment(sketch, "E1501", {"start": v(-4.47, -1.8) * mm, "end": v(-4.47, -1.79) * mm});
            skLineSegment(sketch, "E1502", {"start": v(-4.47, -1.79) * mm, "end": v(-4.5, -1.77) * mm});
            skLineSegment(sketch, "E1503", {"start": v(-4.5, -1.77) * mm, "end": v(-4.52, -1.75) * mm});
            skLineSegment(sketch, "E1504", {"start": v(-4.52, -1.75) * mm, "end": v(-4.55, -1.73) * mm});
            skLineSegment(sketch, "E1505", {"start": v(-4.55, -1.73) * mm, "end": v(-4.58, -1.7) * mm});
            skLineSegment(sketch, "E1506", {"start": v(-4.58, -1.7) * mm, "end": v(-4.62, -1.68) * mm});
            skLineSegment(sketch, "E1507", {"start": v(-4.62, -1.68) * mm, "end": v(-4.65, -1.66) * mm});
            skLineSegment(sketch, "E1508", {"start": v(-4.65, -1.66) * mm, "end": v(-4.68, -1.64) * mm});
            skLineSegment(sketch, "E1509", {"start": v(-4.68, -1.64) * mm, "end": v(-4.8, -1.57) * mm});
            skLineSegment(sketch, "E1510", {"start": v(-4.8, -1.57) * mm, "end": v(-4.94, -1.52) * mm});
            skLineSegment(sketch, "E1511", {"start": v(-4.94, -1.52) * mm, "end": v(-5.08, -1.49) * mm});
            skLineSegment(sketch, "E1512", {"start": v(-5.08, -1.49) * mm, "end": v(-5.2, -1.48) * mm});
            skLineSegment(sketch, "E1513", {"start": v(-5.2, -1.48) * mm, "end": v(-5.24, -1.48) * mm});
            skLineSegment(sketch, "E1514", {"start": v(-5.24, -1.48) * mm, "end": v(-5.28, -1.49) * mm});
            skLineSegment(sketch, "E1515", {"start": v(-5.28, -1.49) * mm, "end": v(-5.31, -1.5) * mm});
            skLineSegment(sketch, "E1516", {"start": v(-5.31, -1.5) * mm, "end": v(-5.34, -1.5) * mm});
            skLineSegment(sketch, "E1517", {"start": v(-5.34, -1.5) * mm, "end": v(-5.36, -1.51) * mm});
            skLineSegment(sketch, "E1518", {"start": v(-5.36, -1.51) * mm, "end": v(-5.37, -1.52) * mm});
            skLineSegment(sketch, "E1519", {"start": v(-5.37, -1.52) * mm, "end": v(-5.38, -1.54) * mm});
            skLineSegment(sketch, "E1520", {"start": v(-5.38, -1.54) * mm, "end": v(-5.38, -1.56) * mm});
            skLineSegment(sketch, "E1521", {"start": v(-5.38, -1.56) * mm, "end": v(-5.39, -1.6) * mm});
            skLineSegment(sketch, "E1522", {"start": v(-5.39, -1.6) * mm, "end": v(-5.4, -1.65) * mm});
            skLineSegment(sketch, "E1523", {"start": v(-5.4, -1.65) * mm, "end": v(-5.42, -1.67) * mm});
            skLineSegment(sketch, "E1524", {"start": v(-5.42, -1.67) * mm, "end": v(-5.43, -1.7) * mm});
            skLineSegment(sketch, "E1525", {"start": v(-5.43, -1.7) * mm, "end": v(-5.43, -1.7) * mm});
            skLineSegment(sketch, "E1526", {"start": v(-5.43, -1.7) * mm, "end": v(-5.42, -1.71) * mm});
            skLineSegment(sketch, "E1527", {"start": v(-5.42, -1.71) * mm, "end": v(-5.4, -1.72) * mm});
            skLineSegment(sketch, "E1528", {"start": v(-5.4, -1.72) * mm, "end": v(-5.34, -1.72) * mm});
            skLineSegment(sketch, "E1529", {"start": v(-5.34, -1.72) * mm, "end": v(-5.24, -1.72) * mm});
            skLineSegment(sketch, "E1530", {"start": v(-5.24, -1.72) * mm, "end": v(-5.1, -1.72) * mm});
            skLineSegment(sketch, "E1531", {"start": v(-5.1, -1.72) * mm, "end": v(-4.98, -1.72) * mm});
            skLineSegment(sketch, "E1532", {"start": v(-4.98, -1.72) * mm, "end": v(-4.89, -1.72) * mm});
            skLineSegment(sketch, "E1533", {"start": v(-4.89, -1.72) * mm, "end": v(-4.8, -1.72) * mm});
            skLineSegment(sketch, "E1534", {"start": v(-4.8, -1.72) * mm, "end": v(-4.75, -1.73) * mm});
            skLineSegment(sketch, "E1535", {"start": v(-4.75, -1.73) * mm, "end": v(-4.7, -1.74) * mm});
            skLineSegment(sketch, "E1536", {"start": v(-4.7, -1.74) * mm, "end": v(-4.64, -1.74) * mm});
            skLineSegment(sketch, "E1537", {"start": v(-4.64, -1.74) * mm, "end": v(-4.6, -1.76) * mm});
            skLineSegment(sketch, "E1538", {"start": v(-4.6, -1.76) * mm, "end": v(-4.55, -1.77) * mm});
            skLineSegment(sketch, "E1539", {"start": v(-4.55, -1.77) * mm, "end": v(-4.5, -1.79) * mm});
            skLineSegment(sketch, "E1540", {"start": v(-4.5, -1.79) * mm, "end": v(-4.48, -1.8) * mm});
            skLineSegment(sketch, "E1541", {"start": v(-4.48, -1.8) * mm, "end": v(-4.47, -1.8) * mm});
            skLineSegment(sketch, "E1542", {"start": v(-4.47, -1.8) * mm, "end": v(-4.47, -1.8) * mm});
            skLineSegment(sketch, "E1543", {"start": v(-4.13, -1.55) * mm, "end": v(-4.16, -1.42) * mm});
            skLineSegment(sketch, "E1544", {"start": v(-4.16, -1.42) * mm, "end": v(-4.22, -1.27) * mm});
            skLineSegment(sketch, "E1545", {"start": v(-4.22, -1.27) * mm, "end": v(-4.3, -1.13) * mm});
            skLineSegment(sketch, "E1546", {"start": v(-4.3, -1.13) * mm, "end": v(-4.36, -1.04) * mm});
            skLineSegment(sketch, "E1547", {"start": v(-4.36, -1.04) * mm, "end": v(-4.39, -1) * mm});
            skLineSegment(sketch, "E1548", {"start": v(-4.39, -1) * mm, "end": v(-4.41, -1) * mm});
            skLineSegment(sketch, "E1549", {"start": v(-4.41, -1) * mm, "end": v(-4.43, -1) * mm});
            skLineSegment(sketch, "E1550", {"start": v(-4.43, -1) * mm, "end": v(-4.46, -1.03) * mm});
            skLineSegment(sketch, "E1551", {"start": v(-4.46, -1.03) * mm, "end": v(-4.49, -1.07) * mm});
            skLineSegment(sketch, "E1552", {"start": v(-4.49, -1.07) * mm, "end": v(-4.51, -1.1) * mm});
            skLineSegment(sketch, "E1553", {"start": v(-4.51, -1.1) * mm, "end": v(-4.54, -1.13) * mm});
            skLineSegment(sketch, "E1554", {"start": v(-4.54, -1.13) * mm, "end": v(-4.55, -1.14) * mm});
            skLineSegment(sketch, "E1555", {"start": v(-4.55, -1.14) * mm, "end": v(-4.54, -1.17) * mm});
            skLineSegment(sketch, "E1556", {"start": v(-4.54, -1.17) * mm, "end": v(-4.52, -1.2) * mm});
            skLineSegment(sketch, "E1557", {"start": v(-4.52, -1.2) * mm, "end": v(-4.48, -1.23) * mm});
            skLineSegment(sketch, "E1558", {"start": v(-4.48, -1.23) * mm, "end": v(-4.43, -1.27) * mm});
            skLineSegment(sketch, "E1559", {"start": v(-4.43, -1.27) * mm, "end": v(-4.35, -1.33) * mm});
            skLineSegment(sketch, "E1560", {"start": v(-4.35, -1.33) * mm, "end": v(-4.27, -1.4) * mm});
            skLineSegment(sketch, "E1561", {"start": v(-4.27, -1.4) * mm, "end": v(-4.2, -1.5) * mm});
            skLineSegment(sketch, "E1562", {"start": v(-4.2, -1.5) * mm, "end": v(-4.15, -1.58) * mm});
            skLineSegment(sketch, "E1563", {"start": v(-4.15, -1.58) * mm, "end": v(-4.14, -1.61) * mm});
            skLineSegment(sketch, "E1564", {"start": v(-4.14, -1.61) * mm, "end": v(-4.13, -1.63) * mm});
            skLineSegment(sketch, "E1565", {"start": v(-4.13, -1.63) * mm, "end": v(-4.12, -1.64) * mm});
            skLineSegment(sketch, "E1566", {"start": v(-4.12, -1.64) * mm, "end": v(-4.11, -1.65) * mm});
            skLineSegment(sketch, "E1567", {"start": v(-4.11, -1.65) * mm, "end": v(-4.11, -1.64) * mm});
            skLineSegment(sketch, "E1568", {"start": v(-4.11, -1.64) * mm, "end": v(-4.12, -1.62) * mm});
            skLineSegment(sketch, "E1569", {"start": v(-4.12, -1.62) * mm, "end": v(-4.12, -1.58) * mm});
            skLineSegment(sketch, "E1570", {"start": v(-4.12, -1.58) * mm, "end": v(-4.13, -1.55) * mm});
            skLineSegment(sketch, "E1571", {"start": v(-3.85, -1.47) * mm, "end": v(-3.83, -1.39) * mm});
            skLineSegment(sketch, "E1572", {"start": v(-3.83, -1.39) * mm, "end": v(-3.8, -1.28) * mm});
            skLineSegment(sketch, "E1573", {"start": v(-3.8, -1.28) * mm, "end": v(-3.8, -1.16) * mm});
            skLineSegment(sketch, "E1574", {"start": v(-3.8, -1.16) * mm, "end": v(-3.78, -1.06) * mm});
            skLineSegment(sketch, "E1575", {"start": v(-3.78, -1.06) * mm, "end": v(-3.78, -1) * mm});
            skLineSegment(sketch, "E1576", {"start": v(-3.78, -1) * mm, "end": v(-3.8, -0.96) * mm});
            skLineSegment(sketch, "E1577", {"start": v(-3.8, -0.96) * mm, "end": v(-3.8, -0.93) * mm});
            skLineSegment(sketch, "E1578", {"start": v(-3.8, -0.93) * mm, "end": v(-3.83, -0.93) * mm});
            skLineSegment(sketch, "E1579", {"start": v(-3.83, -0.93) * mm, "end": v(-3.85, -0.93) * mm});
            skLineSegment(sketch, "E1580", {"start": v(-3.85, -0.93) * mm, "end": v(-3.85, -0.97) * mm});
            skLineSegment(sketch, "E1581", {"start": v(-3.85, -0.97) * mm, "end": v(-3.86, -0.99) * mm});
            skLineSegment(sketch, "E1582", {"start": v(-3.86, -0.99) * mm, "end": v(-3.86, -1) * mm});
            skLineSegment(sketch, "E1583", {"start": v(-3.86, -1) * mm, "end": v(-3.87, -1) * mm});
            skLineSegment(sketch, "E1584", {"start": v(-3.87, -1) * mm, "end": v(-3.89, -1.01) * mm});
            skLineSegment(sketch, "E1585", {"start": v(-3.89, -1.01) * mm, "end": v(-3.92, -1.01) * mm});
            skLineSegment(sketch, "E1586", {"start": v(-3.92, -1.01) * mm, "end": v(-3.92, -1.14) * mm});
            skLineSegment(sketch, "E1587", {"start": v(-3.92, -1.14) * mm, "end": v(-3.91, -1.3) * mm});
            skLineSegment(sketch, "E1588", {"start": v(-3.91, -1.3) * mm, "end": v(-3.91, -1.43) * mm});
            skLineSegment(sketch, "E1589", {"start": v(-3.91, -1.43) * mm, "end": v(-3.9, -1.52) * mm});
            skLineSegment(sketch, "E1590", {"start": v(-3.9, -1.52) * mm, "end": v(-3.9, -1.56) * mm});
            skLineSegment(sketch, "E1591", {"start": v(-3.9, -1.56) * mm, "end": v(-3.88, -1.56) * mm});
            skLineSegment(sketch, "E1592", {"start": v(-3.88, -1.56) * mm, "end": v(-3.87, -1.55) * mm});
            skLineSegment(sketch, "E1593", {"start": v(-3.87, -1.55) * mm, "end": v(-3.86, -1.52) * mm});
            skLineSegment(sketch, "E1594", {"start": v(-3.86, -1.52) * mm, "end": v(-3.85, -1.47) * mm});
            skLineSegment(sketch, "E1595", {"start": v(-1.6, -1.28) * mm, "end": v(-1.5, -1.25) * mm});
            skLineSegment(sketch, "E1596", {"start": v(-1.5, -1.25) * mm, "end": v(-1.38, -1.2) * mm});
            skLineSegment(sketch, "E1597", {"start": v(-1.38, -1.2) * mm, "end": v(-1.26, -1.14) * mm});
            skLineSegment(sketch, "E1598", {"start": v(-1.26, -1.14) * mm, "end": v(-1.16, -1.07) * mm});
            skLineSegment(sketch, "E1599", {"start": v(-1.16, -1.07) * mm, "end": v(-1.12, -1.05) * mm});
            skLineSegment(sketch, "E1600", {"start": v(-1.12, -1.05) * mm, "end": v(-1.07, -1.03) * mm});
            skLineSegment(sketch, "E1601", {"start": v(-1.07, -1.03) * mm, "end": v(-1, -1) * mm});
            skLineSegment(sketch, "E1602", {"start": v(-1, -1) * mm, "end": v(-0.94, -0.96) * mm});
            skLineSegment(sketch, "E1603", {"start": v(-0.94, -0.96) * mm, "end": v(-0.87, -0.92) * mm});
            skLineSegment(sketch, "E1604", {"start": v(-0.87, -0.92) * mm, "end": v(-0.8, -0.9) * mm});
            skLineSegment(sketch, "E1605", {"start": v(-0.8, -0.9) * mm, "end": v(-0.75, -0.87) * mm});
            skLineSegment(sketch, "E1606", {"start": v(-0.75, -0.87) * mm, "end": v(-0.7, -0.85) * mm});
            skLineSegment(sketch, "E1607", {"start": v(-0.7, -0.85) * mm, "end": v(-0.63, -0.83) * mm});
            skLineSegment(sketch, "E1608", {"start": v(-0.63, -0.83) * mm, "end": v(-0.7, -0.77) * mm});
            skLineSegment(sketch, "E1609", {"start": v(-0.7, -0.77) * mm, "end": v(-0.74, -0.73) * mm});
            skLineSegment(sketch, "E1610", {"start": v(-0.74, -0.73) * mm, "end": v(-0.79, -0.7) * mm});
            skLineSegment(sketch, "E1611", {"start": v(-0.79, -0.7) * mm, "end": v(-0.85, -0.67) * mm});
            skLineSegment(sketch, "E1612", {"start": v(-0.85, -0.67) * mm, "end": v(-0.91, -0.65) * mm});
            skLineSegment(sketch, "E1613", {"start": v(-0.91, -0.65) * mm, "end": v(-1, -0.65) * mm});
            skLineSegment(sketch, "E1614", {"start": v(-1, -0.65) * mm, "end": v(-1.1, -0.67) * mm});
            skLineSegment(sketch, "E1615", {"start": v(-1.1, -0.67) * mm, "end": v(-1.23, -0.72) * mm});
            skLineSegment(sketch, "E1616", {"start": v(-1.23, -0.72) * mm, "end": v(-1.37, -0.8) * mm});
            skLineSegment(sketch, "E1617", {"start": v(-1.37, -0.8) * mm, "end": v(-1.44, -0.83) * mm});
            skLineSegment(sketch, "E1618", {"start": v(-1.44, -0.83) * mm, "end": v(-1.49, -0.85) * mm});
            skLineSegment(sketch, "E1619", {"start": v(-1.49, -0.85) * mm, "end": v(-1.51, -0.85) * mm});
            skLineSegment(sketch, "E1620", {"start": v(-1.51, -0.85) * mm, "end": v(-1.53, -0.83) * mm});
            skLineSegment(sketch, "E1621", {"start": v(-1.53, -0.83) * mm, "end": v(-1.53, -0.8) * mm});
            skLineSegment(sketch, "E1622", {"start": v(-1.53, -0.8) * mm, "end": v(-1.52, -0.78) * mm});
            skLineSegment(sketch, "E1623", {"start": v(-1.52, -0.78) * mm, "end": v(-1.49, -0.74) * mm});
            skLineSegment(sketch, "E1624", {"start": v(-1.49, -0.74) * mm, "end": v(-1.44, -0.68) * mm});
            skLineSegment(sketch, "E1625", {"start": v(-1.44, -0.68) * mm, "end": v(-1.38, -0.6) * mm});
            skLineSegment(sketch, "E1626", {"start": v(-1.38, -0.6) * mm, "end": v(-1.32, -0.52) * mm});
            skLineSegment(sketch, "E1627", {"start": v(-1.32, -0.52) * mm, "end": v(-1.28, -0.42) * mm});
            skLineSegment(sketch, "E1628", {"start": v(-1.28, -0.42) * mm, "end": v(-1.26, -0.33) * mm});
            skLineSegment(sketch, "E1629", {"start": v(-1.26, -0.33) * mm, "end": v(-1.25, -0.28) * mm});
            skLineSegment(sketch, "E1630", {"start": v(-1.25, -0.28) * mm, "end": v(-1.25, -0.23) * mm});
            skLineSegment(sketch, "E1631", {"start": v(-1.25, -0.23) * mm, "end": v(-1.24, -0.16) * mm});
            skLineSegment(sketch, "E1632", {"start": v(-1.24, -0.16) * mm, "end": v(-1.24, -0.08) * mm});
            skLineSegment(sketch, "E1633", {"start": v(-1.24, -0.08) * mm, "end": v(-1.24, -0.01) * mm});
            skLineSegment(sketch, "E1634", {"start": v(-1.24, -0.01) * mm, "end": v(-1.24, 0.05) * mm});
            skLineSegment(sketch, "E1635", {"start": v(-1.24, 0.05) * mm, "end": v(-1.24, 0.09) * mm});
            skLineSegment(sketch, "E1636", {"start": v(-1.24, 0.09) * mm, "end": v(-1.25, 0.1) * mm});
            skLineSegment(sketch, "E1637", {"start": v(-1.25, 0.1) * mm, "end": v(-1.27, 0.1) * mm});
            skLineSegment(sketch, "E1638", {"start": v(-1.27, 0.1) * mm, "end": v(-1.31, 0.1) * mm});
            skLineSegment(sketch, "E1639", {"start": v(-1.31, 0.1) * mm, "end": v(-1.37, 0.06) * mm});
            skLineSegment(sketch, "E1640", {"start": v(-1.37, 0.06) * mm, "end": v(-1.44, 0.02) * mm});
            skLineSegment(sketch, "E1641", {"start": v(-1.44, 0.02) * mm, "end": v(-1.53, -0.05) * mm});
            skLineSegment(sketch, "E1642", {"start": v(-1.53, -0.05) * mm, "end": v(-1.65, -0.16) * mm});
            skLineSegment(sketch, "E1643", {"start": v(-1.65, -0.16) * mm, "end": v(-1.77, -0.29) * mm});
            skLineSegment(sketch, "E1644", {"start": v(-1.77, -0.29) * mm, "end": v(-1.87, -0.4) * mm});
            skLineSegment(sketch, "E1645", {"start": v(-1.87, -0.4) * mm, "end": v(-1.92, -0.47) * mm});
            skLineSegment(sketch, "E1646", {"start": v(-1.92, -0.47) * mm, "end": v(-1.95, -0.5) * mm});
            skLineSegment(sketch, "E1647", {"start": v(-1.95, -0.5) * mm, "end": v(-1.97, -0.53) * mm});
            skLineSegment(sketch, "E1648", {"start": v(-1.97, -0.53) * mm, "end": v(-1.98, -0.53) * mm});
            skLineSegment(sketch, "E1649", {"start": v(-1.98, -0.53) * mm, "end": v(-1.99, -0.52) * mm});
            skLineSegment(sketch, "E1650", {"start": v(-1.99, -0.52) * mm, "end": v(-2, -0.53) * mm});
            skLineSegment(sketch, "E1651", {"start": v(-2, -0.53) * mm, "end": v(-2.02, -0.54) * mm});
            skLineSegment(sketch, "E1652", {"start": v(-2.02, -0.54) * mm, "end": v(-2.05, -0.53) * mm});
            skLineSegment(sketch, "E1653", {"start": v(-2.05, -0.53) * mm, "end": v(-2.06, -0.52) * mm});
            skLineSegment(sketch, "E1654", {"start": v(-2.06, -0.52) * mm, "end": v(-2.07, -0.51) * mm});
            skLineSegment(sketch, "E1655", {"start": v(-2.07, -0.51) * mm, "end": v(-2.07, -0.5) * mm});
            skLineSegment(sketch, "E1656", {"start": v(-2.07, -0.5) * mm, "end": v(-2.06, -0.46) * mm});
            skLineSegment(sketch, "E1657", {"start": v(-2.06, -0.46) * mm, "end": v(-2.05, -0.27) * mm});
            skLineSegment(sketch, "E1658", {"start": v(-2.05, -0.27) * mm, "end": v(-2.06, -0.1) * mm});
            skLineSegment(sketch, "E1659", {"start": v(-2.06, -0.1) * mm, "end": v(-2.07, -0.04) * mm});
            skLineSegment(sketch, "E1660", {"start": v(-2.07, -0.04) * mm, "end": v(-2.09, 0.02) * mm});
            skLineSegment(sketch, "E1661", {"start": v(-2.09, 0.02) * mm, "end": v(-2.1, 0.06) * mm});
            skLineSegment(sketch, "E1662", {"start": v(-2.1, 0.06) * mm, "end": v(-2.11, 0.1) * mm});
            skLineSegment(sketch, "E1663", {"start": v(-2.11, 0.1) * mm, "end": v(-2.13, 0.12) * mm});
            skLineSegment(sketch, "E1664", {"start": v(-2.13, 0.12) * mm, "end": v(-2.14, 0.13) * mm});
            skLineSegment(sketch, "E1665", {"start": v(-2.14, 0.13) * mm, "end": v(-2.14, 0.11) * mm});
            skLineSegment(sketch, "E1666", {"start": v(-2.14, 0.11) * mm, "end": v(-2.14, 0.08) * mm});
            skLineSegment(sketch, "E1667", {"start": v(-2.14, 0.08) * mm, "end": v(-2.15, 0) * mm});
            skLineSegment(sketch, "E1668", {"start": v(-2.15, 0) * mm, "end": v(-2.17, -0.14) * mm});
            skLineSegment(sketch, "E1669", {"start": v(-2.17, -0.14) * mm, "end": v(-2.2, -0.33) * mm});
            skLineSegment(sketch, "E1670", {"start": v(-2.2, -0.33) * mm, "end": v(-2.25, -0.55) * mm});
            skLineSegment(sketch, "E1671", {"start": v(-2.25, -0.55) * mm, "end": v(-2.27, -0.67) * mm});
            skLineSegment(sketch, "E1672", {"start": v(-2.27, -0.67) * mm, "end": v(-2.27, -0.82) * mm});
            skLineSegment(sketch, "E1673", {"start": v(-2.27, -0.82) * mm, "end": v(-2.27, -0.95) * mm});
            skLineSegment(sketch, "E1674", {"start": v(-2.27, -0.95) * mm, "end": v(-2.26, -1.03) * mm});
            skLineSegment(sketch, "E1675", {"start": v(-2.26, -1.03) * mm, "end": v(-2.25, -1.06) * mm});
            skLineSegment(sketch, "E1676", {"start": v(-2.25, -1.06) * mm, "end": v(-2.23, -1.1) * mm});
            skLineSegment(sketch, "E1677", {"start": v(-2.23, -1.1) * mm, "end": v(-2.2, -1.11) * mm});
            skLineSegment(sketch, "E1678", {"start": v(-2.2, -1.11) * mm, "end": v(-2.2, -1.12) * mm});
            skLineSegment(sketch, "E1679", {"start": v(-2.2, -1.12) * mm, "end": v(-2.19, -1.11) * mm});
            skLineSegment(sketch, "E1680", {"start": v(-2.19, -1.11) * mm, "end": v(-2.19, -1.08) * mm});
            skLineSegment(sketch, "E1681", {"start": v(-2.19, -1.08) * mm, "end": v(-2.18, -1.05) * mm});
            skLineSegment(sketch, "E1682", {"start": v(-2.18, -1.05) * mm, "end": v(-2.18, -1) * mm});
            skLineSegment(sketch, "E1683", {"start": v(-2.18, -1) * mm, "end": v(-2.18, -0.91) * mm});
            skLineSegment(sketch, "E1684", {"start": v(-2.18, -0.91) * mm, "end": v(-2.17, -0.85) * mm});
            skLineSegment(sketch, "E1685", {"start": v(-2.17, -0.85) * mm, "end": v(-2.15, -0.8) * mm});
            skLineSegment(sketch, "E1686", {"start": v(-2.15, -0.8) * mm, "end": v(-2.13, -0.79) * mm});
            skLineSegment(sketch, "E1687", {"start": v(-2.13, -0.79) * mm, "end": v(-2.12, -0.8) * mm});
            skLineSegment(sketch, "E1688", {"start": v(-2.12, -0.8) * mm, "end": v(-2.1, -0.8) * mm});
            skLineSegment(sketch, "E1689", {"start": v(-2.1, -0.8) * mm, "end": v(-2.1, -0.83) * mm});
            skLineSegment(sketch, "E1690", {"start": v(-2.1, -0.83) * mm, "end": v(-2.07, -0.86) * mm});
            skLineSegment(sketch, "E1691", {"start": v(-2.07, -0.86) * mm, "end": v(-2.05, -0.9) * mm});
            skLineSegment(sketch, "E1692", {"start": v(-2.05, -0.9) * mm, "end": v(-2.04, -0.92) * mm});
            skLineSegment(sketch, "E1693", {"start": v(-2.04, -0.92) * mm, "end": v(-2.03, -0.94) * mm});
            skLineSegment(sketch, "E1694", {"start": v(-2.03, -0.94) * mm, "end": v(-2.02, -0.95) * mm});
            skLineSegment(sketch, "E1695", {"start": v(-2.02, -0.95) * mm, "end": v(-2.02, -0.96) * mm});
            skLineSegment(sketch, "E1696", {"start": v(-2.02, -0.96) * mm, "end": v(-2.01, -0.96) * mm});
            skLineSegment(sketch, "E1697", {"start": v(-2.01, -0.96) * mm, "end": v(-2, -0.95) * mm});
            skLineSegment(sketch, "E1698", {"start": v(-2, -0.95) * mm, "end": v(-1.98, -0.92) * mm});
            skLineSegment(sketch, "E1699", {"start": v(-1.98, -0.92) * mm, "end": v(-1.95, -0.87) * mm});
            skLineSegment(sketch, "E1700", {"start": v(-1.95, -0.87) * mm, "end": v(-1.9, -0.82) * mm});
            skLineSegment(sketch, "E1701", {"start": v(-1.9, -0.82) * mm, "end": v(-1.84, -0.76) * mm});
            skLineSegment(sketch, "E1702", {"start": v(-1.84, -0.76) * mm, "end": v(-1.77, -0.7) * mm});
            skLineSegment(sketch, "E1703", {"start": v(-1.77, -0.7) * mm, "end": v(-1.71, -0.66) * mm});
            skLineSegment(sketch, "E1704", {"start": v(-1.71, -0.66) * mm, "end": v(-1.68, -0.65) * mm});
            skLineSegment(sketch, "E1705", {"start": v(-1.68, -0.65) * mm, "end": v(-1.67, -0.66) * mm});
            skLineSegment(sketch, "E1706", {"start": v(-1.67, -0.66) * mm, "end": v(-1.67, -0.7) * mm});
            skLineSegment(sketch, "E1707", {"start": v(-1.67, -0.7) * mm, "end": v(-1.68, -0.75) * mm});
            skLineSegment(sketch, "E1708", {"start": v(-1.68, -0.75) * mm, "end": v(-1.69, -0.8) * mm});
            skLineSegment(sketch, "E1709", {"start": v(-1.69, -0.8) * mm, "end": v(-1.7, -0.88) * mm});
            skLineSegment(sketch, "E1710", {"start": v(-1.7, -0.88) * mm, "end": v(-1.7, -0.95) * mm});
            skLineSegment(sketch, "E1711", {"start": v(-1.7, -0.95) * mm, "end": v(-1.71, -1.01) * mm});
            skLineSegment(sketch, "E1712", {"start": v(-1.71, -1.01) * mm, "end": v(-1.73, -1.06) * mm});
            skLineSegment(sketch, "E1713", {"start": v(-1.73, -1.06) * mm, "end": v(-1.74, -1.08) * mm});
            skLineSegment(sketch, "E1714", {"start": v(-1.74, -1.08) * mm, "end": v(-1.74, -1.1) * mm});
            skLineSegment(sketch, "E1715", {"start": v(-1.74, -1.1) * mm, "end": v(-1.74, -1.1) * mm});
            skLineSegment(sketch, "E1716", {"start": v(-1.74, -1.1) * mm, "end": v(-1.72, -1.1) * mm});
            skLineSegment(sketch, "E1717", {"start": v(-1.72, -1.1) * mm, "end": v(-1.7, -1.1) * mm});
            skLineSegment(sketch, "E1718", {"start": v(-1.7, -1.1) * mm, "end": v(-1.67, -1.1) * mm});
            skLineSegment(sketch, "E1719", {"start": v(-1.67, -1.1) * mm, "end": v(-1.65, -1.12) * mm});
            skLineSegment(sketch, "E1720", {"start": v(-1.65, -1.12) * mm, "end": v(-1.62, -1.13) * mm});
            skLineSegment(sketch, "E1721", {"start": v(-1.62, -1.13) * mm, "end": v(-1.6, -1.14) * mm});
            skLineSegment(sketch, "E1722", {"start": v(-1.6, -1.14) * mm, "end": v(-1.58, -1.16) * mm});
            skLineSegment(sketch, "E1723", {"start": v(-1.58, -1.16) * mm, "end": v(-1.58, -1.18) * mm});
            skLineSegment(sketch, "E1724", {"start": v(-1.58, -1.18) * mm, "end": v(-1.6, -1.2) * mm});
            skLineSegment(sketch, "E1725", {"start": v(-1.6, -1.2) * mm, "end": v(-1.61, -1.21) * mm});
            skLineSegment(sketch, "E1726", {"start": v(-1.61, -1.21) * mm, "end": v(-1.64, -1.23) * mm});
            skLineSegment(sketch, "E1727", {"start": v(-1.64, -1.23) * mm, "end": v(-1.67, -1.25) * mm});
            skLineSegment(sketch, "E1728", {"start": v(-1.67, -1.25) * mm, "end": v(-1.7, -1.27) * mm});
            skLineSegment(sketch, "E1729", {"start": v(-1.7, -1.27) * mm, "end": v(-1.74, -1.28) * mm});
            skLineSegment(sketch, "E1730", {"start": v(-1.74, -1.28) * mm, "end": v(-1.77, -1.28) * mm});
            skLineSegment(sketch, "E1731", {"start": v(-1.77, -1.28) * mm, "end": v(-1.8, -1.3) * mm});
            skLineSegment(sketch, "E1732", {"start": v(-1.8, -1.3) * mm, "end": v(-1.84, -1.3) * mm});
            skLineSegment(sketch, "E1733", {"start": v(-1.84, -1.3) * mm, "end": v(-1.84, -1.3) * mm});
            skLineSegment(sketch, "E1734", {"start": v(-1.84, -1.3) * mm, "end": v(-1.78, -1.3) * mm});
            skLineSegment(sketch, "E1735", {"start": v(-1.78, -1.3) * mm, "end": v(-1.69, -1.3) * mm});
            skLineSegment(sketch, "E1736", {"start": v(-1.69, -1.3) * mm, "end": v(-1.6, -1.28) * mm});
            skLineSegment(sketch, "E1737", {"start": v(0.73, -0.9) * mm, "end": v(0.8, -0.87) * mm});
            skLineSegment(sketch, "E1738", {"start": v(0.8, -0.87) * mm, "end": v(0.87, -0.86) * mm});
            skLineSegment(sketch, "E1739", {"start": v(0.87, -0.86) * mm, "end": v(0.91, -0.85) * mm});
            skLineSegment(sketch, "E1740", {"start": v(0.91, -0.85) * mm, "end": v(0.94, -0.85) * mm});
            skLineSegment(sketch, "E1741", {"start": v(0.94, -0.85) * mm, "end": v(0.95, -0.84) * mm});
            skLineSegment(sketch, "E1742", {"start": v(0.95, -0.84) * mm, "end": v(0.96, -0.82) * mm});
            skLineSegment(sketch, "E1743", {"start": v(0.96, -0.82) * mm, "end": v(1, -0.78) * mm});
            skLineSegment(sketch, "E1744", {"start": v(1, -0.78) * mm, "end": v(1.04, -0.73) * mm});
            skLineSegment(sketch, "E1745", {"start": v(1.04, -0.73) * mm, "end": v(1.09, -0.69) * mm});
            skLineSegment(sketch, "E1746", {"start": v(1.09, -0.69) * mm, "end": v(1.12, -0.66) * mm});
            skLineSegment(sketch, "E1747", {"start": v(1.12, -0.66) * mm, "end": v(1.14, -0.66) * mm});
            skLineSegment(sketch, "E1748", {"start": v(1.14, -0.66) * mm, "end": v(1.17, -0.64) * mm});
            skLineSegment(sketch, "E1749", {"start": v(1.17, -0.64) * mm, "end": v(1.2, -0.63) * mm});
            skLineSegment(sketch, "E1750", {"start": v(1.2, -0.63) * mm, "end": v(1.24, -0.62) * mm});
            skLineSegment(sketch, "E1751", {"start": v(1.24, -0.62) * mm, "end": v(1.3, -0.6) * mm});
            skLineSegment(sketch, "E1752", {"start": v(1.3, -0.6) * mm, "end": v(1.33, -0.58) * mm});
            skLineSegment(sketch, "E1753", {"start": v(1.33, -0.58) * mm, "end": v(1.35, -0.56) * mm});
            skLineSegment(sketch, "E1754", {"start": v(1.35, -0.56) * mm, "end": v(1.35, -0.54) * mm});
            skLineSegment(sketch, "E1755", {"start": v(1.35, -0.54) * mm, "end": v(1.32, -0.48) * mm});
            skLineSegment(sketch, "E1756", {"start": v(1.32, -0.48) * mm, "end": v(1.23, -0.42) * mm});
            skLineSegment(sketch, "E1757", {"start": v(1.23, -0.42) * mm, "end": v(1.1, -0.37) * mm});
            skLineSegment(sketch, "E1758", {"start": v(1.1, -0.37) * mm, "end": v(0.97, -0.33) * mm});
            skLineSegment(sketch, "E1759", {"start": v(0.97, -0.33) * mm, "end": v(0.8, -0.3) * mm});
            skLineSegment(sketch, "E1760", {"start": v(0.8, -0.3) * mm, "end": v(0.62, -0.3) * mm});
            skLineSegment(sketch, "E1761", {"start": v(0.62, -0.3) * mm, "end": v(0.43, -0.3) * mm});
            skLineSegment(sketch, "E1762", {"start": v(0.43, -0.3) * mm, "end": v(0.24, -0.32) * mm});
            skLineSegment(sketch, "E1763", {"start": v(0.24, -0.32) * mm, "end": v(-0.07, -0.36) * mm});
            skLineSegment(sketch, "E1764", {"start": v(-0.07, -0.36) * mm, "end": v(-0.34, -0.42) * mm});
            skLineSegment(sketch, "E1765", {"start": v(-0.34, -0.42) * mm, "end": v(-0.43, -0.45) * mm});
            skLineSegment(sketch, "E1766", {"start": v(-0.43, -0.45) * mm, "end": v(-0.52, -0.47) * mm});
            skLineSegment(sketch, "E1767", {"start": v(-0.52, -0.47) * mm, "end": v(-0.6, -0.5) * mm});
            skLineSegment(sketch, "E1768", {"start": v(-0.6, -0.5) * mm, "end": v(-0.68, -0.53) * mm});
            skLineSegment(sketch, "E1769", {"start": v(-0.68, -0.53) * mm, "end": v(-0.74, -0.55) * mm});
            skLineSegment(sketch, "E1770", {"start": v(-0.74, -0.55) * mm, "end": v(-0.8, -0.57) * mm});
            skLineSegment(sketch, "E1771", {"start": v(-0.8, -0.57) * mm, "end": v(-0.82, -0.59) * mm});
            skLineSegment(sketch, "E1772", {"start": v(-0.82, -0.59) * mm, "end": v(-0.82, -0.6) * mm});
            skLineSegment(sketch, "E1773", {"start": v(-0.82, -0.6) * mm, "end": v(-0.8, -0.6) * mm});
            skLineSegment(sketch, "E1774", {"start": v(-0.8, -0.6) * mm, "end": v(-0.76, -0.6) * mm});
            skLineSegment(sketch, "E1775", {"start": v(-0.76, -0.6) * mm, "end": v(-0.67, -0.58) * mm});
            skLineSegment(sketch, "E1776", {"start": v(-0.67, -0.58) * mm, "end": v(-0.55, -0.57) * mm});
            skLineSegment(sketch, "E1777", {"start": v(-0.55, -0.57) * mm, "end": v(-0.44, -0.57) * mm});
            skLineSegment(sketch, "E1778", {"start": v(-0.44, -0.57) * mm, "end": v(-0.34, -0.58) * mm});
            skLineSegment(sketch, "E1779", {"start": v(-0.34, -0.58) * mm, "end": v(-0.22, -0.6) * mm});
            skLineSegment(sketch, "E1780", {"start": v(-0.22, -0.6) * mm, "end": v(-0.1, -0.62) * mm});
            skLineSegment(sketch, "E1781", {"start": v(-0.1, -0.62) * mm, "end": v(0.04, -0.65) * mm});
            skLineSegment(sketch, "E1782", {"start": v(0.04, -0.65) * mm, "end": v(0.14, -0.68) * mm});
            skLineSegment(sketch, "E1783", {"start": v(0.14, -0.68) * mm, "end": v(0.23, -0.7) * mm});
            skLineSegment(sketch, "E1784", {"start": v(0.23, -0.7) * mm, "end": v(0.31, -0.75) * mm});
            skLineSegment(sketch, "E1785", {"start": v(0.31, -0.75) * mm, "end": v(0.4, -0.8) * mm});
            skLineSegment(sketch, "E1786", {"start": v(0.4, -0.8) * mm, "end": v(0.46, -0.84) * mm});
            skLineSegment(sketch, "E1787", {"start": v(0.46, -0.84) * mm, "end": v(0.52, -0.89) * mm});
            skLineSegment(sketch, "E1788", {"start": v(0.52, -0.89) * mm, "end": v(0.57, -0.92) * mm});
            skLineSegment(sketch, "E1789", {"start": v(0.57, -0.92) * mm, "end": v(0.6, -0.94) * mm});
            skLineSegment(sketch, "E1790", {"start": v(0.6, -0.94) * mm, "end": v(0.63, -0.94) * mm});
            skLineSegment(sketch, "E1791", {"start": v(0.63, -0.94) * mm, "end": v(0.64, -0.94) * mm});
            skLineSegment(sketch, "E1792", {"start": v(0.64, -0.94) * mm, "end": v(0.67, -0.93) * mm});
            skLineSegment(sketch, "E1793", {"start": v(0.67, -0.93) * mm, "end": v(0.7, -0.92) * mm});
            skLineSegment(sketch, "E1794", {"start": v(0.7, -0.92) * mm, "end": v(0.73, -0.9) * mm});
            skLineSegment(sketch, "E1795", {"start": v(-0.5, 0) * mm, "end": v(-0.36, 0.05) * mm});
            skLineSegment(sketch, "E1796", {"start": v(-0.36, 0.05) * mm, "end": v(-0.22, 0.1) * mm});
            skLineSegment(sketch, "E1797", {"start": v(-0.22, 0.1) * mm, "end": v(-0.16, 0.11) * mm});
            skLineSegment(sketch, "E1798", {"start": v(-0.16, 0.11) * mm, "end": v(-0.1, 0.13) * mm});
            skLineSegment(sketch, "E1799", {"start": v(-0.1, 0.13) * mm, "end": v(-0.05, 0.15) * mm});
            skLineSegment(sketch, "E1800", {"start": v(-0.05, 0.15) * mm, "end": v(-0.02, 0.16) * mm});
            skLineSegment(sketch, "E1801", {"start": v(-0.02, 0.16) * mm, "end": v(0.08, 0.19) * mm});
            skLineSegment(sketch, "E1802", {"start": v(0.08, 0.19) * mm, "end": v(0.21, 0.22) * mm});
            skLineSegment(sketch, "E1803", {"start": v(0.21, 0.22) * mm, "end": v(0.34, 0.24) * mm});
            skLineSegment(sketch, "E1804", {"start": v(0.34, 0.24) * mm, "end": v(0.44, 0.26) * mm});
            skLineSegment(sketch, "E1805", {"start": v(0.44, 0.26) * mm, "end": v(0.5, 0.26) * mm});
            skLineSegment(sketch, "E1806", {"start": v(0.5, 0.26) * mm, "end": v(0.59, 0.27) * mm});
            skLineSegment(sketch, "E1807", {"start": v(0.59, 0.27) * mm, "end": v(0.7, 0.27) * mm});
            skLineSegment(sketch, "E1808", {"start": v(0.7, 0.27) * mm, "end": v(0.81, 0.27) * mm});
            skLineSegment(sketch, "E1809", {"start": v(0.81, 0.27) * mm, "end": v(0.95, 0.28) * mm});
            skLineSegment(sketch, "E1810", {"start": v(0.95, 0.28) * mm, "end": v(1.05, 0.28) * mm});
            skLineSegment(sketch, "E1811", {"start": v(1.05, 0.28) * mm, "end": v(1.14, 0.3) * mm});
            skLineSegment(sketch, "E1812", {"start": v(1.14, 0.3) * mm, "end": v(1.2, 0.3) * mm});
            skLineSegment(sketch, "E1813", {"start": v(1.2, 0.3) * mm, "end": v(1.26, 0.3) * mm});
            skLineSegment(sketch, "E1814", {"start": v(1.26, 0.3) * mm, "end": v(1.29, 0.32) * mm});
            skLineSegment(sketch, "E1815", {"start": v(1.29, 0.32) * mm, "end": v(1.3, 0.34) * mm});
            skLineSegment(sketch, "E1816", {"start": v(1.3, 0.34) * mm, "end": v(1.31, 0.36) * mm});
            skLineSegment(sketch, "E1817", {"start": v(1.31, 0.36) * mm, "end": v(1.3, 0.4) * mm});
            skLineSegment(sketch, "E1818", {"start": v(1.3, 0.4) * mm, "end": v(1.27, 0.43) * mm});
            skLineSegment(sketch, "E1819", {"start": v(1.27, 0.43) * mm, "end": v(1.2, 0.47) * mm});
            skLineSegment(sketch, "E1820", {"start": v(1.2, 0.47) * mm, "end": v(1.12, 0.5) * mm});
            skLineSegment(sketch, "E1821", {"start": v(1.12, 0.5) * mm, "end": v(0.98, 0.53) * mm});
            skLineSegment(sketch, "E1822", {"start": v(0.98, 0.53) * mm, "end": v(0.8, 0.53) * mm});
            skLineSegment(sketch, "E1823", {"start": v(0.8, 0.53) * mm, "end": v(0.6, 0.52) * mm});
            skLineSegment(sketch, "E1824", {"start": v(0.6, 0.52) * mm, "end": v(0.4, 0.5) * mm});
            skLineSegment(sketch, "E1825", {"start": v(0.4, 0.5) * mm, "end": v(0.2, 0.43) * mm});
            skLineSegment(sketch, "E1826", {"start": v(0.2, 0.43) * mm, "end": v(-0.02, 0.35) * mm});
            skLineSegment(sketch, "E1827", {"start": v(-0.02, 0.35) * mm, "end": v(-0.24, 0.24) * mm});
            skLineSegment(sketch, "E1828", {"start": v(-0.24, 0.24) * mm, "end": v(-0.45, 0.11) * mm});
            skLineSegment(sketch, "E1829", {"start": v(-0.45, 0.11) * mm, "end": v(-0.5, 0.08) * mm});
            skLineSegment(sketch, "E1830", {"start": v(-0.5, 0.08) * mm, "end": v(-0.56, 0.04) * mm});
            skLineSegment(sketch, "E1831", {"start": v(-0.56, 0.04) * mm, "end": v(-0.62, 0) * mm});
            skLineSegment(sketch, "E1832", {"start": v(-0.62, 0) * mm, "end": v(-0.67, -0.04) * mm});
            skLineSegment(sketch, "E1833", {"start": v(-0.67, -0.04) * mm, "end": v(-0.72, -0.08) * mm});
            skLineSegment(sketch, "E1834", {"start": v(-0.72, -0.08) * mm, "end": v(-0.76, -0.1) * mm});
            skLineSegment(sketch, "E1835", {"start": v(-0.76, -0.1) * mm, "end": v(-0.78, -0.13) * mm});
            skLineSegment(sketch, "E1836", {"start": v(-0.78, -0.13) * mm, "end": v(-0.79, -0.14) * mm});
            skLineSegment(sketch, "E1837", {"start": v(-0.79, -0.14) * mm, "end": v(-0.78, -0.13) * mm});
            skLineSegment(sketch, "E1838", {"start": v(-0.78, -0.13) * mm, "end": v(-0.77, -0.13) * mm});
            skLineSegment(sketch, "E1839", {"start": v(-0.77, -0.13) * mm, "end": v(-0.74, -0.11) * mm});
            skLineSegment(sketch, "E1840", {"start": v(-0.74, -0.11) * mm, "end": v(-0.7, -0.1) * mm});
            skLineSegment(sketch, "E1841", {"start": v(-0.7, -0.1) * mm, "end": v(-0.67, -0.08) * mm});
            skLineSegment(sketch, "E1842", {"start": v(-0.67, -0.08) * mm, "end": v(-0.61, -0.05) * mm});
            skLineSegment(sketch, "E1843", {"start": v(-0.61, -0.05) * mm, "end": v(-0.55, -0.02) * mm});
            skLineSegment(sketch, "E1844", {"start": v(-0.55, -0.02) * mm, "end": v(-0.5, 0) * mm});
            skLineSegment(sketch, "E1845", {"start": v(-1.96, 0.12) * mm, "end": v(-2, 0.4) * mm});
            skLineSegment(sketch, "E1846", {"start": v(-2, 0.4) * mm, "end": v(-2.05, 0.6) * mm});
            skLineSegment(sketch, "E1847", {"start": v(-2.05, 0.6) * mm, "end": v(-2.1, 0.7) * mm});
            skLineSegment(sketch, "E1848", {"start": v(-2.1, 0.7) * mm, "end": v(-2.14, 0.8) * mm});
            skLineSegment(sketch, "E1849", {"start": v(-2.14, 0.8) * mm, "end": v(-2.2, 0.9) * mm});
            skLineSegment(sketch, "E1850", {"start": v(-2.2, 0.9) * mm, "end": v(-2.24, 0.97) * mm});
            skLineSegment(sketch, "E1851", {"start": v(-2.24, 0.97) * mm, "end": v(-2.34, 1.08) * mm});
            skLineSegment(sketch, "E1852", {"start": v(-2.34, 1.08) * mm, "end": v(-2.46, 1.18) * mm});
            skLineSegment(sketch, "E1853", {"start": v(-2.46, 1.18) * mm, "end": v(-2.58, 1.25) * mm});
            skLineSegment(sketch, "E1854", {"start": v(-2.58, 1.25) * mm, "end": v(-2.69, 1.28) * mm});
            skLineSegment(sketch, "E1855", {"start": v(-2.69, 1.28) * mm, "end": v(-2.71, 1.28) * mm});
            skLineSegment(sketch, "E1856", {"start": v(-2.71, 1.28) * mm, "end": v(-2.73, 1.28) * mm});
            skLineSegment(sketch, "E1857", {"start": v(-2.73, 1.28) * mm, "end": v(-2.74, 1.28) * mm});
            skLineSegment(sketch, "E1858", {"start": v(-2.74, 1.28) * mm, "end": v(-2.75, 1.27) * mm});
            skLineSegment(sketch, "E1859", {"start": v(-2.75, 1.27) * mm, "end": v(-2.76, 1.26) * mm});
            skLineSegment(sketch, "E1860", {"start": v(-2.76, 1.26) * mm, "end": v(-2.77, 1.24) * mm});
            skLineSegment(sketch, "E1861", {"start": v(-2.77, 1.24) * mm, "end": v(-2.77, 1.22) * mm});
            skLineSegment(sketch, "E1862", {"start": v(-2.77, 1.22) * mm, "end": v(-2.77, 1.19) * mm});
            skLineSegment(sketch, "E1863", {"start": v(-2.77, 1.19) * mm, "end": v(-2.77, 1.15) * mm});
            skLineSegment(sketch, "E1864", {"start": v(-2.77, 1.15) * mm, "end": v(-2.77, 1.12) * mm});
            skLineSegment(sketch, "E1865", {"start": v(-2.77, 1.12) * mm, "end": v(-2.78, 1.1) * mm});
            skLineSegment(sketch, "E1866", {"start": v(-2.78, 1.1) * mm, "end": v(-2.8, 1.07) * mm});
            skLineSegment(sketch, "E1867", {"start": v(-2.8, 1.07) * mm, "end": v(-2.82, 1) * mm});
            skLineSegment(sketch, "E1868", {"start": v(-2.82, 1) * mm, "end": v(-2.81, 0.95) * mm});
            skLineSegment(sketch, "E1869", {"start": v(-2.81, 0.95) * mm, "end": v(-2.78, 0.9) * mm});
            skLineSegment(sketch, "E1870", {"start": v(-2.78, 0.9) * mm, "end": v(-2.71, 0.84) * mm});
            skLineSegment(sketch, "E1871", {"start": v(-2.71, 0.84) * mm, "end": v(-2.7, 0.82) * mm});
            skLineSegment(sketch, "E1872", {"start": v(-2.7, 0.82) * mm, "end": v(-2.66, 0.8) * mm});
            skLineSegment(sketch, "E1873", {"start": v(-2.66, 0.8) * mm, "end": v(-2.64, 0.79) * mm});
            skLineSegment(sketch, "E1874", {"start": v(-2.64, 0.79) * mm, "end": v(-2.61, 0.77) * mm});
            skLineSegment(sketch, "E1875", {"start": v(-2.61, 0.77) * mm, "end": v(-2.57, 0.74) * mm});
            skLineSegment(sketch, "E1876", {"start": v(-2.57, 0.74) * mm, "end": v(-2.52, 0.7) * mm});
            skLineSegment(sketch, "E1877", {"start": v(-2.52, 0.7) * mm, "end": v(-2.47, 0.64) * mm});
            skLineSegment(sketch, "E1878", {"start": v(-2.47, 0.64) * mm, "end": v(-2.4, 0.59) * mm});
            skLineSegment(sketch, "E1879", {"start": v(-2.4, 0.59) * mm, "end": v(-2.35, 0.53) * mm});
            skLineSegment(sketch, "E1880", {"start": v(-2.35, 0.53) * mm, "end": v(-2.3, 0.47) * mm});
            skLineSegment(sketch, "E1881", {"start": v(-2.3, 0.47) * mm, "end": v(-2.26, 0.42) * mm});
            skLineSegment(sketch, "E1882", {"start": v(-2.26, 0.42) * mm, "end": v(-2.23, 0.39) * mm});
            skLineSegment(sketch, "E1883", {"start": v(-2.23, 0.39) * mm, "end": v(-2.21, 0.36) * mm});
            skLineSegment(sketch, "E1884", {"start": v(-2.21, 0.36) * mm, "end": v(-2.2, 0.34) * mm});
            skLineSegment(sketch, "E1885", {"start": v(-2.2, 0.34) * mm, "end": v(-2.18, 0.33) * mm});
            skLineSegment(sketch, "E1886", {"start": v(-2.18, 0.33) * mm, "end": v(-2.17, 0.32) * mm});
            skLineSegment(sketch, "E1887", {"start": v(-2.17, 0.32) * mm, "end": v(-2.15, 0.31) * mm});
            skLineSegment(sketch, "E1888", {"start": v(-2.15, 0.31) * mm, "end": v(-2.13, 0.29) * mm});
            skLineSegment(sketch, "E1889", {"start": v(-2.13, 0.29) * mm, "end": v(-2.1, 0.25) * mm});
            skLineSegment(sketch, "E1890", {"start": v(-2.1, 0.25) * mm, "end": v(-2.08, 0.22) * mm});
            skLineSegment(sketch, "E1891", {"start": v(-2.08, 0.22) * mm, "end": v(-2.06, 0.17) * mm});
            skLineSegment(sketch, "E1892", {"start": v(-2.06, 0.17) * mm, "end": v(-2.03, 0.08) * mm});
            skLineSegment(sketch, "E1893", {"start": v(-2.03, 0.08) * mm, "end": v(-2, -0.01) * mm});
            skLineSegment(sketch, "E1894", {"start": v(-2, -0.01) * mm, "end": v(-1.98, -0.08) * mm});
            skLineSegment(sketch, "E1895", {"start": v(-1.98, -0.08) * mm, "end": v(-1.97, -0.11) * mm});
            skLineSegment(sketch, "E1896", {"start": v(-1.97, -0.11) * mm, "end": v(-1.97, -0.08) * mm});
            skLineSegment(sketch, "E1897", {"start": v(-1.97, -0.08) * mm, "end": v(-1.96, -0.05) * mm});
            skLineSegment(sketch, "E1898", {"start": v(-1.96, -0.05) * mm, "end": v(-1.96, 0) * mm});
            skLineSegment(sketch, "E1899", {"start": v(-1.96, 0) * mm, "end": v(-1.96, 0.06) * mm});
            skLineSegment(sketch, "E1900", {"start": v(-1.96, 0.06) * mm, "end": v(-1.96, 0.12) * mm});
            skLineSegment(sketch, "E1901", {"start": v(-0.81, 0.31) * mm, "end": v(-0.75, 0.37) * mm});
            skLineSegment(sketch, "E1902", {"start": v(-0.75, 0.37) * mm, "end": v(-0.68, 0.43) * mm});
            skLineSegment(sketch, "E1903", {"start": v(-0.68, 0.43) * mm, "end": v(-0.6, 0.5) * mm});
            skLineSegment(sketch, "E1904", {"start": v(-0.6, 0.5) * mm, "end": v(-0.52, 0.57) * mm});
            skLineSegment(sketch, "E1905", {"start": v(-0.52, 0.57) * mm, "end": v(-0.44, 0.63) * mm});
            skLineSegment(sketch, "E1906", {"start": v(-0.44, 0.63) * mm, "end": v(-0.37, 0.68) * mm});
            skLineSegment(sketch, "E1907", {"start": v(-0.37, 0.68) * mm, "end": v(-0.3, 0.72) * mm});
            skLineSegment(sketch, "E1908", {"start": v(-0.3, 0.72) * mm, "end": v(-0.25, 0.75) * mm});
            skLineSegment(sketch, "E1909", {"start": v(-0.25, 0.75) * mm, "end": v(-0.23, 0.77) * mm});
            skLineSegment(sketch, "E1910", {"start": v(-0.23, 0.77) * mm, "end": v(-0.2, 0.79) * mm});
            skLineSegment(sketch, "E1911", {"start": v(-0.2, 0.79) * mm, "end": v(-0.16, 0.8) * mm});
            skLineSegment(sketch, "E1912", {"start": v(-0.16, 0.8) * mm, "end": v(-0.12, 0.83) * mm});
            skLineSegment(sketch, "E1913", {"start": v(-0.12, 0.83) * mm, "end": v(-0.09, 0.85) * mm});
            skLineSegment(sketch, "E1914", {"start": v(-0.09, 0.85) * mm, "end": v(-0.03, 0.89) * mm});
            skLineSegment(sketch, "E1915", {"start": v(-0.03, 0.89) * mm, "end": v(0.02, 0.92) * mm});
            skLineSegment(sketch, "E1916", {"start": v(0.02, 0.92) * mm, "end": v(0.08, 0.95) * mm});
            skLineSegment(sketch, "E1917", {"start": v(0.08, 0.95) * mm, "end": v(0.2, 1.02) * mm});
            skLineSegment(sketch, "E1918", {"start": v(0.2, 1.02) * mm, "end": v(0.3, 1.08) * mm});
            skLineSegment(sketch, "E1919", {"start": v(0.3, 1.08) * mm, "end": v(0.37, 1.13) * mm});
            skLineSegment(sketch, "E1920", {"start": v(0.37, 1.13) * mm, "end": v(0.43, 1.17) * mm});
            skLineSegment(sketch, "E1921", {"start": v(0.43, 1.17) * mm, "end": v(0.48, 1.2) * mm});
            skLineSegment(sketch, "E1922", {"start": v(0.48, 1.2) * mm, "end": v(0.51, 1.23) * mm});
            skLineSegment(sketch, "E1923", {"start": v(0.51, 1.23) * mm, "end": v(0.54, 1.26) * mm});
            skLineSegment(sketch, "E1924", {"start": v(0.54, 1.26) * mm, "end": v(0.55, 1.28) * mm});
            skLineSegment(sketch, "E1925", {"start": v(0.55, 1.28) * mm, "end": v(0.56, 1.3) * mm});
            skLineSegment(sketch, "E1926", {"start": v(0.56, 1.3) * mm, "end": v(0.56, 1.3) * mm});
            skLineSegment(sketch, "E1927", {"start": v(0.56, 1.3) * mm, "end": v(0.55, 1.32) * mm});
            skLineSegment(sketch, "E1928", {"start": v(0.55, 1.32) * mm, "end": v(0.53, 1.34) * mm});
            skLineSegment(sketch, "E1929", {"start": v(0.53, 1.34) * mm, "end": v(0.5, 1.36) * mm});
            skLineSegment(sketch, "E1930", {"start": v(0.5, 1.36) * mm, "end": v(0.46, 1.38) * mm});
            skLineSegment(sketch, "E1931", {"start": v(0.46, 1.38) * mm, "end": v(0.37, 1.37) * mm});
            skLineSegment(sketch, "E1932", {"start": v(0.37, 1.37) * mm, "end": v(0.24, 1.35) * mm});
            skLineSegment(sketch, "E1933", {"start": v(0.24, 1.35) * mm, "end": v(0.1, 1.3) * mm});
            skLineSegment(sketch, "E1934", {"start": v(0.1, 1.3) * mm, "end": v(-0.04, 1.25) * mm});
            skLineSegment(sketch, "E1935", {"start": v(-0.04, 1.25) * mm, "end": v(-0.11, 1.22) * mm});
            skLineSegment(sketch, "E1936", {"start": v(-0.11, 1.22) * mm, "end": v(-0.16, 1.2) * mm});
            skLineSegment(sketch, "E1937", {"start": v(-0.16, 1.2) * mm, "end": v(-0.2, 1.2) * mm});
            skLineSegment(sketch, "E1938", {"start": v(-0.2, 1.2) * mm, "end": v(-0.22, 1.22) * mm});
            skLineSegment(sketch, "E1939", {"start": v(-0.22, 1.22) * mm, "end": v(-0.26, 1.24) * mm});
            skLineSegment(sketch, "E1940", {"start": v(-0.26, 1.24) * mm, "end": v(-0.32, 1.22) * mm});
            skLineSegment(sketch, "E1941", {"start": v(-0.32, 1.22) * mm, "end": v(-0.4, 1.17) * mm});
            skLineSegment(sketch, "E1942", {"start": v(-0.4, 1.17) * mm, "end": v(-0.5, 1.08) * mm});
            skLineSegment(sketch, "E1943", {"start": v(-0.5, 1.08) * mm, "end": v(-0.57, 1) * mm});
            skLineSegment(sketch, "E1944", {"start": v(-0.57, 1) * mm, "end": v(-0.64, 0.93) * mm});
            skLineSegment(sketch, "E1945", {"start": v(-0.64, 0.93) * mm, "end": v(-0.7, 0.83) * mm});
            skLineSegment(sketch, "E1946", {"start": v(-0.7, 0.83) * mm, "end": v(-0.8, 0.7) * mm});
            skLineSegment(sketch, "E1947", {"start": v(-0.8, 0.7) * mm, "end": v(-0.9, 0.52) * mm});
            skLineSegment(sketch, "E1948", {"start": v(-0.9, 0.52) * mm, "end": v(-0.99, 0.35) * mm});
            skLineSegment(sketch, "E1949", {"start": v(-0.99, 0.35) * mm, "end": v(-1.06, 0.19) * mm});
            skLineSegment(sketch, "E1950", {"start": v(-1.06, 0.19) * mm, "end": v(-1.11, 0.05) * mm});
            skLineSegment(sketch, "E1951", {"start": v(-1.11, 0.05) * mm, "end": v(-1.13, 0) * mm});
            skLineSegment(sketch, "E1952", {"start": v(-1.13, 0) * mm, "end": v(-1.14, -0.02) * mm});
            skLineSegment(sketch, "E1953", {"start": v(-1.14, -0.02) * mm, "end": v(-1.13, -0.02) * mm});
            skLineSegment(sketch, "E1954", {"start": v(-1.13, -0.02) * mm, "end": v(-1.11, 0) * mm});
            skLineSegment(sketch, "E1955", {"start": v(-1.11, 0) * mm, "end": v(-1.08, 0.04) * mm});
            skLineSegment(sketch, "E1956", {"start": v(-1.08, 0.04) * mm, "end": v(-1.04, 0.09) * mm});
            skLineSegment(sketch, "E1957", {"start": v(-1.04, 0.09) * mm, "end": v(-0.98, 0.14) * mm});
            skLineSegment(sketch, "E1958", {"start": v(-0.98, 0.14) * mm, "end": v(-0.92, 0.2) * mm});
            skLineSegment(sketch, "E1959", {"start": v(-0.92, 0.2) * mm, "end": v(-0.86, 0.26) * mm});
            skLineSegment(sketch, "E1960", {"start": v(-0.86, 0.26) * mm, "end": v(-0.81, 0.31) * mm});
            skLineSegment(sketch, "E1961", {"start": v(-1.48, 0.12) * mm, "end": v(-1.48, 0.17) * mm});
            skLineSegment(sketch, "E1962", {"start": v(-1.48, 0.17) * mm, "end": v(-1.46, 0.22) * mm});
            skLineSegment(sketch, "E1963", {"start": v(-1.46, 0.22) * mm, "end": v(-1.44, 0.27) * mm});
            skLineSegment(sketch, "E1964", {"start": v(-1.44, 0.27) * mm, "end": v(-1.43, 0.34) * mm});
            skLineSegment(sketch, "E1965", {"start": v(-1.43, 0.34) * mm, "end": v(-1.4, 0.42) * mm});
            skLineSegment(sketch, "E1966", {"start": v(-1.4, 0.42) * mm, "end": v(-1.39, 0.52) * mm});
            skLineSegment(sketch, "E1967", {"start": v(-1.39, 0.52) * mm, "end": v(-1.36, 0.63) * mm});
            skLineSegment(sketch, "E1968", {"start": v(-1.36, 0.63) * mm, "end": v(-1.34, 0.73) * mm});
            skLineSegment(sketch, "E1969", {"start": v(-1.34, 0.73) * mm, "end": v(-1.33, 0.82) * mm});
            skLineSegment(sketch, "E1970", {"start": v(-1.33, 0.82) * mm, "end": v(-1.32, 0.9) * mm});
            skLineSegment(sketch, "E1971", {"start": v(-1.32, 0.9) * mm, "end": v(-1.3, 1.04) * mm});
            skLineSegment(sketch, "E1972", {"start": v(-1.3, 1.04) * mm, "end": v(-1.29, 1.19) * mm});
            skLineSegment(sketch, "E1973", {"start": v(-1.29, 1.19) * mm, "end": v(-1.28, 1.33) * mm});
            skLineSegment(sketch, "E1974", {"start": v(-1.28, 1.33) * mm, "end": v(-1.27, 1.47) * mm});
            skLineSegment(sketch, "E1975", {"start": v(-1.27, 1.47) * mm, "end": v(-1.27, 1.6) * mm});
            skLineSegment(sketch, "E1976", {"start": v(-1.27, 1.6) * mm, "end": v(-1.27, 1.7) * mm});
            skLineSegment(sketch, "E1977", {"start": v(-1.27, 1.7) * mm, "end": v(-1.27, 1.78) * mm});
            skLineSegment(sketch, "E1978", {"start": v(-1.27, 1.78) * mm, "end": v(-1.28, 1.84) * mm});
            skLineSegment(sketch, "E1979", {"start": v(-1.28, 1.84) * mm, "end": v(-1.3, 1.88) * mm});
            skLineSegment(sketch, "E1980", {"start": v(-1.3, 1.88) * mm, "end": v(-1.3, 1.9) * mm});
            skLineSegment(sketch, "E1981", {"start": v(-1.3, 1.9) * mm, "end": v(-1.3, 1.91) * mm});
            skLineSegment(sketch, "E1982", {"start": v(-1.3, 1.91) * mm, "end": v(-1.3, 1.94) * mm});
            skLineSegment(sketch, "E1983", {"start": v(-1.3, 1.94) * mm, "end": v(-1.32, 1.98) * mm});
            skLineSegment(sketch, "E1984", {"start": v(-1.32, 1.98) * mm, "end": v(-1.35, 2.01) * mm});
            skLineSegment(sketch, "E1985", {"start": v(-1.35, 2.01) * mm, "end": v(-1.38, 2.05) * mm});
            skLineSegment(sketch, "E1986", {"start": v(-1.38, 2.05) * mm, "end": v(-1.41, 2.08) * mm});
            skLineSegment(sketch, "E1987", {"start": v(-1.41, 2.08) * mm, "end": v(-1.44, 2.1) * mm});
            skLineSegment(sketch, "E1988", {"start": v(-1.44, 2.1) * mm, "end": v(-1.46, 2.11) * mm});
            skLineSegment(sketch, "E1989", {"start": v(-1.46, 2.11) * mm, "end": v(-1.48, 2.1) * mm});
            skLineSegment(sketch, "E1990", {"start": v(-1.48, 2.1) * mm, "end": v(-1.5, 2.1) * mm});
            skLineSegment(sketch, "E1991", {"start": v(-1.5, 2.1) * mm, "end": v(-1.53, 2.07) * mm});
            skLineSegment(sketch, "E1992", {"start": v(-1.53, 2.07) * mm, "end": v(-1.55, 2.05) * mm});
            skLineSegment(sketch, "E1993", {"start": v(-1.55, 2.05) * mm, "end": v(-1.6, 2) * mm});
            skLineSegment(sketch, "E1994", {"start": v(-1.6, 2) * mm, "end": v(-1.65, 1.97) * mm});
            skLineSegment(sketch, "E1995", {"start": v(-1.65, 1.97) * mm, "end": v(-1.7, 1.96) * mm});
            skLineSegment(sketch, "E1996", {"start": v(-1.7, 1.96) * mm, "end": v(-1.79, 1.95) * mm});
            skLineSegment(sketch, "E1997", {"start": v(-1.79, 1.95) * mm, "end": v(-1.86, 1.94) * mm});
            skLineSegment(sketch, "E1998", {"start": v(-1.86, 1.94) * mm, "end": v(-1.9, 1.93) * mm});
            skLineSegment(sketch, "E1999", {"start": v(-1.9, 1.93) * mm, "end": v(-1.93, 1.92) * mm});
            skLineSegment(sketch, "E2000", {"start": v(-1.93, 1.92) * mm, "end": v(-1.95, 1.89) * mm});
            skLineSegment(sketch, "E2001", {"start": v(-1.95, 1.89) * mm, "end": v(-1.97, 1.85) * mm});
            skLineSegment(sketch, "E2002", {"start": v(-1.97, 1.85) * mm, "end": v(-1.97, 1.8) * mm});
            skLineSegment(sketch, "E2003", {"start": v(-1.97, 1.8) * mm, "end": v(-1.95, 1.76) * mm});
            skLineSegment(sketch, "E2004", {"start": v(-1.95, 1.76) * mm, "end": v(-1.93, 1.7) * mm});
            skLineSegment(sketch, "E2005", {"start": v(-1.93, 1.7) * mm, "end": v(-1.83, 1.53) * mm});
            skLineSegment(sketch, "E2006", {"start": v(-1.83, 1.53) * mm, "end": v(-1.75, 1.4) * mm});
            skLineSegment(sketch, "E2007", {"start": v(-1.75, 1.4) * mm, "end": v(-1.74, 1.36) * mm});
            skLineSegment(sketch, "E2008", {"start": v(-1.74, 1.36) * mm, "end": v(-1.72, 1.34) * mm});
            skLineSegment(sketch, "E2009", {"start": v(-1.72, 1.34) * mm, "end": v(-1.72, 1.32) * mm});
            skLineSegment(sketch, "E2010", {"start": v(-1.72, 1.32) * mm, "end": v(-1.71, 1.32) * mm});
            skLineSegment(sketch, "E2011", {"start": v(-1.71, 1.32) * mm, "end": v(-1.7, 1.3) * mm});
            skLineSegment(sketch, "E2012", {"start": v(-1.7, 1.3) * mm, "end": v(-1.7, 1.29) * mm});
            skLineSegment(sketch, "E2013", {"start": v(-1.7, 1.29) * mm, "end": v(-1.69, 1.26) * mm});
            skLineSegment(sketch, "E2014", {"start": v(-1.69, 1.26) * mm, "end": v(-1.67, 1.23) * mm});
            skLineSegment(sketch, "E2015", {"start": v(-1.67, 1.23) * mm, "end": v(-1.63, 1.14) * mm});
            skLineSegment(sketch, "E2016", {"start": v(-1.63, 1.14) * mm, "end": v(-1.6, 1.07) * mm});
            skLineSegment(sketch, "E2017", {"start": v(-1.6, 1.07) * mm, "end": v(-1.59, 1) * mm});
            skLineSegment(sketch, "E2018", {"start": v(-1.59, 1) * mm, "end": v(-1.57, 0.95) * mm});
            skLineSegment(sketch, "E2019", {"start": v(-1.57, 0.95) * mm, "end": v(-1.55, 0.77) * mm});
            skLineSegment(sketch, "E2020", {"start": v(-1.55, 0.77) * mm, "end": v(-1.54, 0.56) * mm});
            skLineSegment(sketch, "E2021", {"start": v(-1.54, 0.56) * mm, "end": v(-1.54, 0.35) * mm});
            skLineSegment(sketch, "E2022", {"start": v(-1.54, 0.35) * mm, "end": v(-1.55, 0.16) * mm});
            skLineSegment(sketch, "E2023", {"start": v(-1.55, 0.16) * mm, "end": v(-1.57, 0.02) * mm});
            skLineSegment(sketch, "E2024", {"start": v(-1.57, 0.02) * mm, "end": v(-1.53, 0.05) * mm});
            skLineSegment(sketch, "E2025", {"start": v(-1.53, 0.05) * mm, "end": v(-1.5, 0.07) * mm});
            skLineSegment(sketch, "E2026", {"start": v(-1.5, 0.07) * mm, "end": v(-1.5, 0.09) * mm});
            skLineSegment(sketch, "E2027", {"start": v(-1.5, 0.09) * mm, "end": v(-1.49, 0.1) * mm});
            skLineSegment(sketch, "E2028", {"start": v(-1.49, 0.1) * mm, "end": v(-1.48, 0.12) * mm});
            skSolve(sketch);
        }
        {
            var Q0;
            Q0=makeQuery(id+"F0.imprint","IMPRINT",FACE,{"disambiguationData":[TD([[makeQuery(id+"F0.imprint","IMPRINT",EDGE,{"derivedFrom":sQuery(id+"F0.wireOp",EDGE,"E0")}),-1.0]])]});
            extrude(context, id + "F1", {"entities" : qUnion([Q0]), "depth" : 25 * mm});
        }
    });
